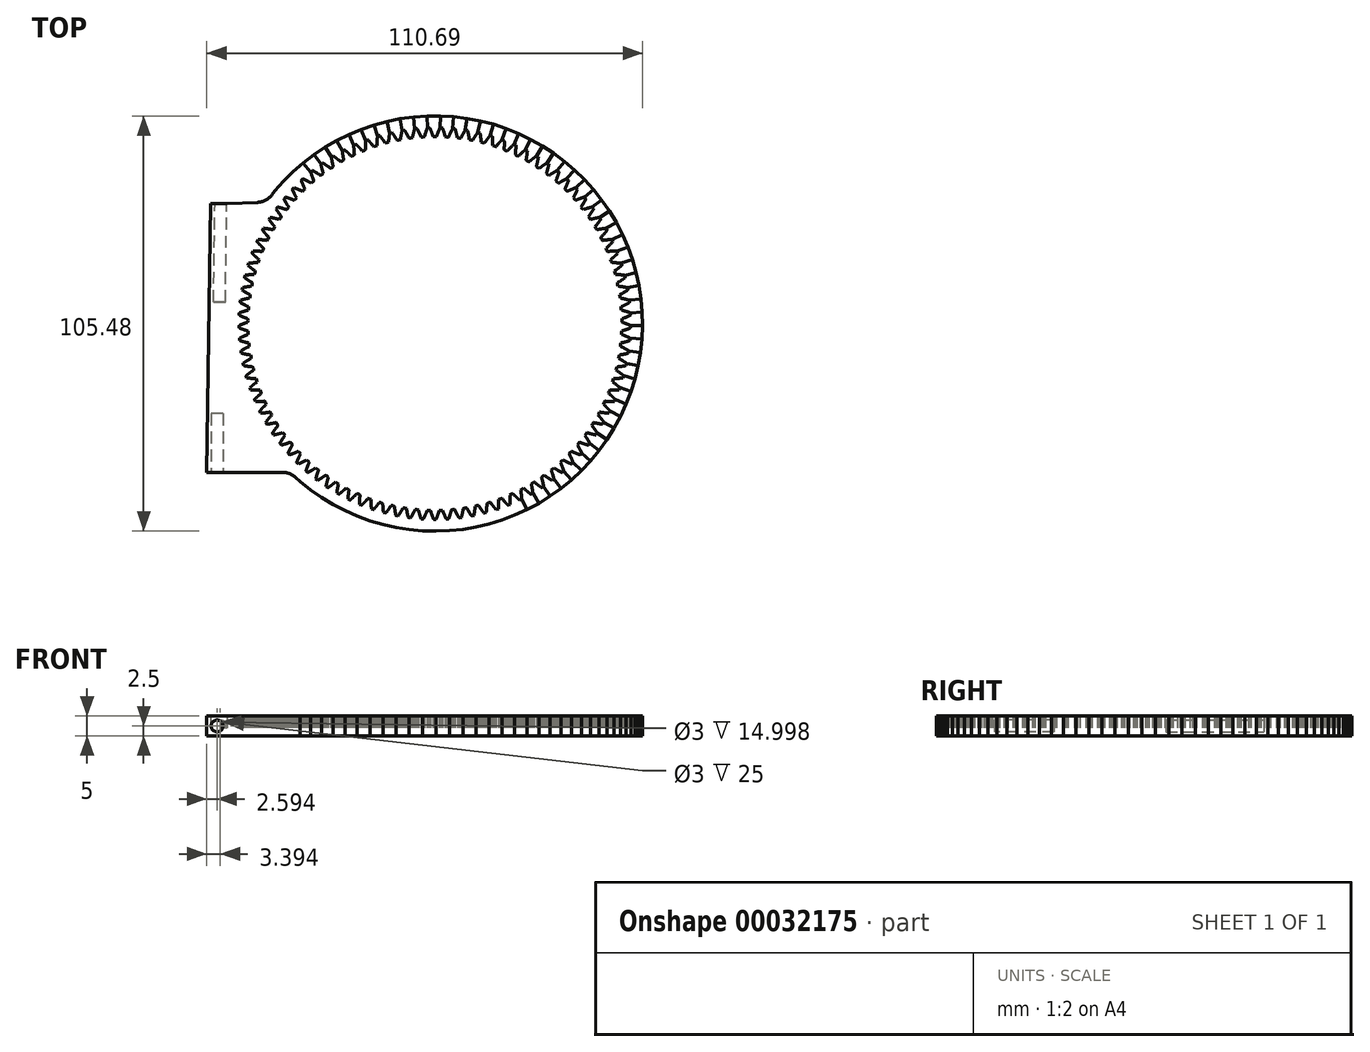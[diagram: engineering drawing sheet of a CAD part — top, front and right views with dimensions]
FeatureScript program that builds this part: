
annotation { "Feature Type Name" : "Feature", "Feature Type Description" : "" }
export const myFeature = defineFeature(function(context is Context, id is Id, definition is map)
    precondition{}
    {
        {
            var Q0;
            Q0=qCreatedBy(makeId("Top.planeOp"),FACE);
            var sketch = newSketch(context, id + "F0", { "sketchPlane" : qUnion([Q0])});
            skCircle(sketch, "E0", {"center": v(0, 0) * mm, "radius": 52.75 * mm});
            skLineSegment(sketch, "E1", {"start": v(1.31, 49.73) * mm, "end": v(1.3, 49.69) * mm});
            skLineSegment(sketch, "E2", {"start": v(1.3, 49.69) * mm, "end": v(1.27, 49.64) * mm});
            skLineSegment(sketch, "E3", {"start": v(1.27, 49.64) * mm, "end": v(1.25, 49.6) * mm});
            skLineSegment(sketch, "E4", {"start": v(1.25, 49.6) * mm, "end": v(1.23, 49.55) * mm});
            skLineSegment(sketch, "E5", {"start": v(1.23, 49.55) * mm, "end": v(1.21, 49.51) * mm});
            skLineSegment(sketch, "E6", {"start": v(1.21, 49.51) * mm, "end": v(1.2, 49.47) * mm});
            skLineSegment(sketch, "E7", {"start": v(1.2, 49.47) * mm, "end": v(1.17, 49.42) * mm});
            skLineSegment(sketch, "E8", {"start": v(1.17, 49.42) * mm, "end": v(1.15, 49.38) * mm});
            skLineSegment(sketch, "E9", {"start": v(1.15, 49.38) * mm, "end": v(1.13, 49.33) * mm});
            skLineSegment(sketch, "E10", {"start": v(1.13, 49.33) * mm, "end": v(1.11, 49.29) * mm});
            skLineSegment(sketch, "E11", {"start": v(1.11, 49.29) * mm, "end": v(1.1, 49.24) * mm});
            skLineSegment(sketch, "E12", {"start": v(1.1, 49.24) * mm, "end": v(1.07, 49.2) * mm});
            skLineSegment(sketch, "E13", {"start": v(1.07, 49.2) * mm, "end": v(1.05, 49.15) * mm});
            skLineSegment(sketch, "E14", {"start": v(1.05, 49.15) * mm, "end": v(1.03, 49.1) * mm});
            skLineSegment(sketch, "E15", {"start": v(1.03, 49.1) * mm, "end": v(1.02, 49.06) * mm});
            skLineSegment(sketch, "E16", {"start": v(1.02, 49.06) * mm, "end": v(1, 49.02) * mm});
            skLineSegment(sketch, "E17", {"start": v(1, 49.02) * mm, "end": v(0.98, 48.98) * mm});
            skLineSegment(sketch, "E18", {"start": v(0.98, 48.98) * mm, "end": v(0.96, 48.93) * mm});
            skLineSegment(sketch, "E19", {"start": v(0.96, 48.93) * mm, "end": v(0.94, 48.89) * mm});
            skLineSegment(sketch, "E20", {"start": v(0.94, 48.89) * mm, "end": v(0.92, 48.84) * mm});
            skLineSegment(sketch, "E21", {"start": v(0.92, 48.84) * mm, "end": v(0.9, 48.8) * mm});
            skLineSegment(sketch, "E22", {"start": v(0.9, 48.8) * mm, "end": v(0.89, 48.75) * mm});
            skLineSegment(sketch, "E23", {"start": v(0.89, 48.75) * mm, "end": v(0.87, 48.7) * mm});
            skLineSegment(sketch, "E24", {"start": v(0.87, 48.7) * mm, "end": v(0.85, 48.66) * mm});
            skLineSegment(sketch, "E25", {"start": v(0.85, 48.66) * mm, "end": v(0.83, 48.62) * mm});
            skLineSegment(sketch, "E26", {"start": v(0.83, 48.62) * mm, "end": v(0.82, 48.57) * mm});
            skLineSegment(sketch, "E27", {"start": v(0.82, 48.57) * mm, "end": v(0.8, 48.53) * mm});
            skLineSegment(sketch, "E28", {"start": v(0.8, 48.53) * mm, "end": v(0.78, 48.48) * mm});
            skLineSegment(sketch, "E29", {"start": v(0.78, 48.48) * mm, "end": v(0.76, 48.44) * mm});
            skLineSegment(sketch, "E30", {"start": v(0.76, 48.44) * mm, "end": v(0.75, 48.4) * mm});
            skLineSegment(sketch, "E31", {"start": v(0.75, 48.4) * mm, "end": v(0.73, 48.35) * mm});
            skLineSegment(sketch, "E32", {"start": v(0.73, 48.35) * mm, "end": v(0.71, 48.3) * mm});
            skLineSegment(sketch, "E33", {"start": v(0.71, 48.3) * mm, "end": v(0.7, 48.26) * mm});
            skLineSegment(sketch, "E34", {"start": v(0.7, 48.26) * mm, "end": v(0.68, 48.22) * mm});
            skLineSegment(sketch, "E35", {"start": v(0.68, 48.22) * mm, "end": v(0.67, 48.17) * mm});
            skLineSegment(sketch, "E36", {"start": v(0.67, 48.17) * mm, "end": v(0.65, 48.13) * mm});
            skLineSegment(sketch, "E37", {"start": v(0.65, 48.13) * mm, "end": v(0.63, 48.08) * mm});
            skLineSegment(sketch, "E38", {"start": v(0.63, 48.08) * mm, "end": v(0.62, 48.04) * mm});
            skLineSegment(sketch, "E39", {"start": v(0.62, 48.04) * mm, "end": v(0.6, 48) * mm});
            skLineSegment(sketch, "E40", {"start": v(0.6, 48) * mm, "end": v(0.58, 47.95) * mm});
            skLineSegment(sketch, "E41", {"start": v(0.58, 47.95) * mm, "end": v(0.57, 47.9) * mm});
            skLineSegment(sketch, "E42", {"start": v(0.57, 47.9) * mm, "end": v(0.55, 47.86) * mm});
            skLineSegment(sketch, "E43", {"start": v(0.55, 47.86) * mm, "end": v(0.53, 47.81) * mm});
            skLineSegment(sketch, "E44", {"start": v(0.53, 47.81) * mm, "end": v(0.52, 47.77) * mm});
            skLineSegment(sketch, "E45", {"start": v(0.52, 47.77) * mm, "end": v(0.5, 47.72) * mm});
            skLineSegment(sketch, "E46", {"start": v(0.5, 47.72) * mm, "end": v(0.49, 47.68) * mm});
            skLineSegment(sketch, "E47", {"start": v(0.49, 47.68) * mm, "end": v(0.47, 47.63) * mm});
            skLineSegment(sketch, "E48", {"start": v(0.47, 47.63) * mm, "end": v(0.45, 47.59) * mm});
            skLineSegment(sketch, "E49", {"start": v(0.45, 47.59) * mm, "end": v(0.44, 47.54) * mm});
            skLineSegment(sketch, "E50", {"start": v(0.44, 47.54) * mm, "end": v(0, 47.5) * mm});
            skLineSegment(sketch, "E51", {"start": v(0, 47.5) * mm, "end": v(-0.44, 47.54) * mm});
            skLineSegment(sketch, "E52", {"start": v(-0.44, 47.54) * mm, "end": v(-0.45, 47.59) * mm});
            skLineSegment(sketch, "E53", {"start": v(-0.45, 47.59) * mm, "end": v(-0.47, 47.63) * mm});
            skLineSegment(sketch, "E54", {"start": v(-0.47, 47.63) * mm, "end": v(-0.49, 47.68) * mm});
            skLineSegment(sketch, "E55", {"start": v(-0.49, 47.68) * mm, "end": v(-0.5, 47.72) * mm});
            skLineSegment(sketch, "E56", {"start": v(-0.5, 47.72) * mm, "end": v(-0.52, 47.77) * mm});
            skLineSegment(sketch, "E57", {"start": v(-0.52, 47.77) * mm, "end": v(-0.53, 47.81) * mm});
            skLineSegment(sketch, "E58", {"start": v(-0.53, 47.81) * mm, "end": v(-0.55, 47.86) * mm});
            skLineSegment(sketch, "E59", {"start": v(-0.55, 47.86) * mm, "end": v(-0.57, 47.9) * mm});
            skLineSegment(sketch, "E60", {"start": v(-0.57, 47.9) * mm, "end": v(-0.58, 47.95) * mm});
            skLineSegment(sketch, "E61", {"start": v(-0.58, 47.95) * mm, "end": v(-0.6, 48) * mm});
            skLineSegment(sketch, "E62", {"start": v(-0.6, 48) * mm, "end": v(-0.62, 48.04) * mm});
            skLineSegment(sketch, "E63", {"start": v(-0.62, 48.04) * mm, "end": v(-0.63, 48.08) * mm});
            skLineSegment(sketch, "E64", {"start": v(-0.63, 48.08) * mm, "end": v(-0.65, 48.13) * mm});
            skLineSegment(sketch, "E65", {"start": v(-0.65, 48.13) * mm, "end": v(-0.67, 48.17) * mm});
            skLineSegment(sketch, "E66", {"start": v(-0.67, 48.17) * mm, "end": v(-0.68, 48.22) * mm});
            skLineSegment(sketch, "E67", {"start": v(-0.68, 48.22) * mm, "end": v(-0.7, 48.26) * mm});
            skLineSegment(sketch, "E68", {"start": v(-0.7, 48.26) * mm, "end": v(-0.71, 48.3) * mm});
            skLineSegment(sketch, "E69", {"start": v(-0.71, 48.3) * mm, "end": v(-0.73, 48.35) * mm});
            skLineSegment(sketch, "E70", {"start": v(-0.73, 48.35) * mm, "end": v(-0.75, 48.4) * mm});
            skLineSegment(sketch, "E71", {"start": v(-0.75, 48.4) * mm, "end": v(-0.76, 48.44) * mm});
            skLineSegment(sketch, "E72", {"start": v(-0.76, 48.44) * mm, "end": v(-0.78, 48.48) * mm});
            skLineSegment(sketch, "E73", {"start": v(-0.78, 48.48) * mm, "end": v(-0.8, 48.53) * mm});
            skLineSegment(sketch, "E74", {"start": v(-0.8, 48.53) * mm, "end": v(-0.82, 48.57) * mm});
            skLineSegment(sketch, "E75", {"start": v(-0.82, 48.57) * mm, "end": v(-0.83, 48.62) * mm});
            skLineSegment(sketch, "E76", {"start": v(-0.83, 48.62) * mm, "end": v(-0.85, 48.66) * mm});
            skLineSegment(sketch, "E77", {"start": v(-0.85, 48.66) * mm, "end": v(-0.87, 48.7) * mm});
            skLineSegment(sketch, "E78", {"start": v(-0.87, 48.7) * mm, "end": v(-0.89, 48.75) * mm});
            skLineSegment(sketch, "E79", {"start": v(-0.89, 48.75) * mm, "end": v(-0.9, 48.8) * mm});
            skLineSegment(sketch, "E80", {"start": v(-0.9, 48.8) * mm, "end": v(-0.92, 48.84) * mm});
            skLineSegment(sketch, "E81", {"start": v(-0.92, 48.84) * mm, "end": v(-0.94, 48.89) * mm});
            skLineSegment(sketch, "E82", {"start": v(-0.94, 48.89) * mm, "end": v(-0.96, 48.93) * mm});
            skLineSegment(sketch, "E83", {"start": v(-0.96, 48.93) * mm, "end": v(-0.98, 48.98) * mm});
            skLineSegment(sketch, "E84", {"start": v(-0.98, 48.98) * mm, "end": v(-1, 49.02) * mm});
            skLineSegment(sketch, "E85", {"start": v(-1, 49.02) * mm, "end": v(-1.02, 49.06) * mm});
            skLineSegment(sketch, "E86", {"start": v(-1.02, 49.06) * mm, "end": v(-1.03, 49.1) * mm});
            skLineSegment(sketch, "E87", {"start": v(-1.03, 49.1) * mm, "end": v(-1.05, 49.15) * mm});
            skLineSegment(sketch, "E88", {"start": v(-1.05, 49.15) * mm, "end": v(-1.07, 49.2) * mm});
            skLineSegment(sketch, "E89", {"start": v(-1.07, 49.2) * mm, "end": v(-1.1, 49.24) * mm});
            skLineSegment(sketch, "E90", {"start": v(-1.1, 49.24) * mm, "end": v(-1.11, 49.29) * mm});
            skLineSegment(sketch, "E91", {"start": v(-1.11, 49.29) * mm, "end": v(-1.13, 49.33) * mm});
            skLineSegment(sketch, "E92", {"start": v(-1.13, 49.33) * mm, "end": v(-1.15, 49.38) * mm});
            skLineSegment(sketch, "E93", {"start": v(-1.15, 49.38) * mm, "end": v(-1.17, 49.42) * mm});
            skLineSegment(sketch, "E94", {"start": v(-1.17, 49.42) * mm, "end": v(-1.2, 49.47) * mm});
            skLineSegment(sketch, "E95", {"start": v(-1.2, 49.47) * mm, "end": v(-1.21, 49.51) * mm});
            skLineSegment(sketch, "E96", {"start": v(-1.21, 49.51) * mm, "end": v(-1.23, 49.55) * mm});
            skLineSegment(sketch, "E97", {"start": v(-1.23, 49.55) * mm, "end": v(-1.25, 49.6) * mm});
            skLineSegment(sketch, "E98", {"start": v(-1.25, 49.6) * mm, "end": v(-1.27, 49.64) * mm});
            skLineSegment(sketch, "E99", {"start": v(-1.27, 49.64) * mm, "end": v(-1.3, 49.69) * mm});
            skLineSegment(sketch, "E100", {"start": v(-1.3, 49.69) * mm, "end": v(-1.31, 49.73) * mm});
            skLineSegment(sketch, "E101", {"start": v(-1.31, 49.73) * mm, "end": v(-1.9, 49.71) * mm});
            skLineSegment(sketch, "E102", {"start": v(0, 0) * mm, "end": v(-2.02, 52.71) * mm});
            skLineSegment(sketch, "E103", {"start": v(0, 0) * mm, "end": v(1.4, 52.73) * mm});
            skLineSegment(sketch, "E104", {"start": v(-2.02, 52.71) * mm, "end": v(1.4, 52.73) * mm});
            skCircle(sketch, "E105", {"center": v(0, 0) * mm, "radius": 0.44 * mm});
            skSolve(sketch);
        }
        {
            var Q0;
            {var subQ3=sQuery(id+"F0.wireOp",EDGE,"E1");Q0=makeQuery(id+"F0.imprint","IMPRINT",FACE,{"disambiguationData":[TD([[makeQuery(id+"F0.imprint","IMPRINT",EDGE,{"derivedFrom":subQ3}),-1.0]])]});}
            var Q1;
            {var subQ1=sQuery(id+"F0.wireOp",EDGE,"E103");var subQ3=sQuery(id+"F0.wireOp",EDGE,"E102");var subQ5=makeQuery(id+"F0.imprint","INTERSECT",VERTEX,{"derivedFrom":[subQ3,subQ1]});Q1=makeQuery(id+"F0.imprint","IMPRINT",FACE,{"disambiguationData":[TD([[makeQuery(id+"F0.imprint","IMPRINT",EDGE,{"disambiguationData":[TD([[subQ5,-1.0]])],"derivedFrom":subQ3}),1.0]])]});}
            var Q2;
            {var subQ0=sQuery(id+"F0.wireOp",EDGE,"E103");var subQ3=sQuery(id+"F0.wireOp",EDGE,"E102");var subQ4=makeQuery(id+"F0.imprint","INTERSECT",VERTEX,{"derivedFrom":[subQ3,subQ0]});Q2=makeQuery(id+"F0.imprint","IMPRINT",FACE,{"disambiguationData":[TD([[makeQuery(id+"F0.imprint","IMPRINT",EDGE,{"disambiguationData":[TD([[subQ4,-1.0]])],"derivedFrom":subQ3}),-1.0]])]});}
            extrude(context, id + "F1", {"entities" : qUnion([Q0, Q1, Q2]), "depth" : 5 * mm});
        }
        {
            var Q0;
            Q0=makeQuery(id+"F1.opExtrude","SWEPT_BODY",BODY,{"disambiguationData":[OSD([sQuery(id+"F0.wireOp",EDGE,"E1"),sQuery(id+"F0.wireOp",EDGE,"E2"),sQuery(id+"F0.wireOp",EDGE,"E3"),sQuery(id+"F0.wireOp",EDGE,"E4"),sQuery(id+"F0.wireOp",EDGE,"E5"),sQuery(id+"F0.wireOp",EDGE,"E6"),sQuery(id+"F0.wireOp",EDGE,"E7"),sQuery(id+"F0.wireOp",EDGE,"E8"),sQuery(id+"F0.wireOp",EDGE,"E9"),sQuery(id+"F0.wireOp",EDGE,"E10"),sQuery(id+"F0.wireOp",EDGE,"E11"),sQuery(id+"F0.wireOp",EDGE,"E12"),sQuery(id+"F0.wireOp",EDGE,"E13"),sQuery(id+"F0.wireOp",EDGE,"E14"),sQuery(id+"F0.wireOp",EDGE,"E15"),sQuery(id+"F0.wireOp",EDGE,"E16"),sQuery(id+"F0.wireOp",EDGE,"E17"),sQuery(id+"F0.wireOp",EDGE,"E18"),sQuery(id+"F0.wireOp",EDGE,"E19"),sQuery(id+"F0.wireOp",EDGE,"E20"),sQuery(id+"F0.wireOp",EDGE,"E21"),sQuery(id+"F0.wireOp",EDGE,"E22"),sQuery(id+"F0.wireOp",EDGE,"E23"),sQuery(id+"F0.wireOp",EDGE,"E24"),sQuery(id+"F0.wireOp",EDGE,"E25"),sQuery(id+"F0.wireOp",EDGE,"E26"),sQuery(id+"F0.wireOp",EDGE,"E27"),sQuery(id+"F0.wireOp",EDGE,"E28"),sQuery(id+"F0.wireOp",EDGE,"E29"),sQuery(id+"F0.wireOp",EDGE,"E30"),sQuery(id+"F0.wireOp",EDGE,"E31"),sQuery(id+"F0.wireOp",EDGE,"E32"),sQuery(id+"F0.wireOp",EDGE,"E33"),sQuery(id+"F0.wireOp",EDGE,"E34"),sQuery(id+"F0.wireOp",EDGE,"E35"),sQuery(id+"F0.wireOp",EDGE,"E36"),sQuery(id+"F0.wireOp",EDGE,"E37"),sQuery(id+"F0.wireOp",EDGE,"E38"),sQuery(id+"F0.wireOp",EDGE,"E39"),sQuery(id+"F0.wireOp",EDGE,"E40"),sQuery(id+"F0.wireOp",EDGE,"E41"),sQuery(id+"F0.wireOp",EDGE,"E42"),sQuery(id+"F0.wireOp",EDGE,"E43"),sQuery(id+"F0.wireOp",EDGE,"E44"),sQuery(id+"F0.wireOp",EDGE,"E45"),sQuery(id+"F0.wireOp",EDGE,"E46"),sQuery(id+"F0.wireOp",EDGE,"E47"),sQuery(id+"F0.wireOp",EDGE,"E48"),sQuery(id+"F0.wireOp",EDGE,"E49"),sQuery(id+"F0.wireOp",EDGE,"E50"),sQuery(id+"F0.wireOp",EDGE,"E51"),sQuery(id+"F0.wireOp",EDGE,"E52"),sQuery(id+"F0.wireOp",EDGE,"E53"),sQuery(id+"F0.wireOp",EDGE,"E54"),sQuery(id+"F0.wireOp",EDGE,"E55"),sQuery(id+"F0.wireOp",EDGE,"E56"),sQuery(id+"F0.wireOp",EDGE,"E57"),sQuery(id+"F0.wireOp",EDGE,"E58"),sQuery(id+"F0.wireOp",EDGE,"E59"),sQuery(id+"F0.wireOp",EDGE,"E60"),sQuery(id+"F0.wireOp",EDGE,"E61"),sQuery(id+"F0.wireOp",EDGE,"E62"),sQuery(id+"F0.wireOp",EDGE,"E63"),sQuery(id+"F0.wireOp",EDGE,"E64"),sQuery(id+"F0.wireOp",EDGE,"E65"),sQuery(id+"F0.wireOp",EDGE,"E66"),sQuery(id+"F0.wireOp",EDGE,"E67"),sQuery(id+"F0.wireOp",EDGE,"E68"),sQuery(id+"F0.wireOp",EDGE,"E69"),sQuery(id+"F0.wireOp",EDGE,"E70"),sQuery(id+"F0.wireOp",EDGE,"E71"),sQuery(id+"F0.wireOp",EDGE,"E72"),sQuery(id+"F0.wireOp",EDGE,"E73"),sQuery(id+"F0.wireOp",EDGE,"E74"),sQuery(id+"F0.wireOp",EDGE,"E75"),sQuery(id+"F0.wireOp",EDGE,"E76"),sQuery(id+"F0.wireOp",EDGE,"E77"),sQuery(id+"F0.wireOp",EDGE,"E78"),sQuery(id+"F0.wireOp",EDGE,"E79"),sQuery(id+"F0.wireOp",EDGE,"E80"),sQuery(id+"F0.wireOp",EDGE,"E81"),sQuery(id+"F0.wireOp",EDGE,"E82"),sQuery(id+"F0.wireOp",EDGE,"E83"),sQuery(id+"F0.wireOp",EDGE,"E84"),sQuery(id+"F0.wireOp",EDGE,"E85"),sQuery(id+"F0.wireOp",EDGE,"E86"),sQuery(id+"F0.wireOp",EDGE,"E87"),sQuery(id+"F0.wireOp",EDGE,"E88"),sQuery(id+"F0.wireOp",EDGE,"E89"),sQuery(id+"F0.wireOp",EDGE,"E90"),sQuery(id+"F0.wireOp",EDGE,"E91"),sQuery(id+"F0.wireOp",EDGE,"E92"),sQuery(id+"F0.wireOp",EDGE,"E93"),sQuery(id+"F0.wireOp",EDGE,"E94"),sQuery(id+"F0.wireOp",EDGE,"E95"),sQuery(id+"F0.wireOp",EDGE,"E96"),sQuery(id+"F0.wireOp",EDGE,"E97"),sQuery(id+"F0.wireOp",EDGE,"E98"),sQuery(id+"F0.wireOp",EDGE,"E99"),sQuery(id+"F0.wireOp",EDGE,"E100"),sQuery(id+"F0.wireOp",EDGE,"E101"),sQuery(id+"F0.wireOp",EDGE,"E102"),sQuery(id+"F0.wireOp",EDGE,"E103"),sQuery(id+"F0.wireOp",EDGE,"E104")])]});
            var Q1;
            Q1=makeQuery(id+"F1.opExtrude","CAP_EDGE",EDGE,{"disambiguationData":[OSD([sQuery(id+"F0.wireOp",EDGE,"E105")])],"isStart":false});
            circularPattern(context, id + "F2", {"entities" : qUnion([Q0]), "axis" : qUnion([Q1]), "angle" : 3.7 * degree, "instanceCount" : 97});
        }
        {
            var Q0;
            Q0=makeQuery(id+"F1.opExtrude","SWEPT_BODY",BODY,{"disambiguationData":[OSD([sQuery(id+"F0.wireOp",EDGE,"E105")])]});
            var Q1;
            Q1=makeQuery(id+"F2.opPattern","COPY",BODY,{"derivedFrom":makeQuery(id+"F1.opExtrude","SWEPT_BODY",BODY,{"disambiguationData":[OSD([sQuery(id+"F0.wireOp",EDGE,"E1"),sQuery(id+"F0.wireOp",EDGE,"E2"),sQuery(id+"F0.wireOp",EDGE,"E3"),sQuery(id+"F0.wireOp",EDGE,"E4"),sQuery(id+"F0.wireOp",EDGE,"E5"),sQuery(id+"F0.wireOp",EDGE,"E6"),sQuery(id+"F0.wireOp",EDGE,"E7"),sQuery(id+"F0.wireOp",EDGE,"E8"),sQuery(id+"F0.wireOp",EDGE,"E9"),sQuery(id+"F0.wireOp",EDGE,"E10"),sQuery(id+"F0.wireOp",EDGE,"E11"),sQuery(id+"F0.wireOp",EDGE,"E12"),sQuery(id+"F0.wireOp",EDGE,"E13"),sQuery(id+"F0.wireOp",EDGE,"E14"),sQuery(id+"F0.wireOp",EDGE,"E15"),sQuery(id+"F0.wireOp",EDGE,"E16"),sQuery(id+"F0.wireOp",EDGE,"E17"),sQuery(id+"F0.wireOp",EDGE,"E18"),sQuery(id+"F0.wireOp",EDGE,"E19"),sQuery(id+"F0.wireOp",EDGE,"E20"),sQuery(id+"F0.wireOp",EDGE,"E21"),sQuery(id+"F0.wireOp",EDGE,"E22"),sQuery(id+"F0.wireOp",EDGE,"E23"),sQuery(id+"F0.wireOp",EDGE,"E24"),sQuery(id+"F0.wireOp",EDGE,"E25"),sQuery(id+"F0.wireOp",EDGE,"E26"),sQuery(id+"F0.wireOp",EDGE,"E27"),sQuery(id+"F0.wireOp",EDGE,"E28"),sQuery(id+"F0.wireOp",EDGE,"E29"),sQuery(id+"F0.wireOp",EDGE,"E30"),sQuery(id+"F0.wireOp",EDGE,"E31"),sQuery(id+"F0.wireOp",EDGE,"E32"),sQuery(id+"F0.wireOp",EDGE,"E33"),sQuery(id+"F0.wireOp",EDGE,"E34"),sQuery(id+"F0.wireOp",EDGE,"E35"),sQuery(id+"F0.wireOp",EDGE,"E36"),sQuery(id+"F0.wireOp",EDGE,"E37"),sQuery(id+"F0.wireOp",EDGE,"E38"),sQuery(id+"F0.wireOp",EDGE,"E39"),sQuery(id+"F0.wireOp",EDGE,"E40"),sQuery(id+"F0.wireOp",EDGE,"E41"),sQuery(id+"F0.wireOp",EDGE,"E42"),sQuery(id+"F0.wireOp",EDGE,"E43"),sQuery(id+"F0.wireOp",EDGE,"E44"),sQuery(id+"F0.wireOp",EDGE,"E45"),sQuery(id+"F0.wireOp",EDGE,"E46"),sQuery(id+"F0.wireOp",EDGE,"E47"),sQuery(id+"F0.wireOp",EDGE,"E48"),sQuery(id+"F0.wireOp",EDGE,"E49"),sQuery(id+"F0.wireOp",EDGE,"E50"),sQuery(id+"F0.wireOp",EDGE,"E51"),sQuery(id+"F0.wireOp",EDGE,"E52"),sQuery(id+"F0.wireOp",EDGE,"E53"),sQuery(id+"F0.wireOp",EDGE,"E54"),sQuery(id+"F0.wireOp",EDGE,"E55"),sQuery(id+"F0.wireOp",EDGE,"E56"),sQuery(id+"F0.wireOp",EDGE,"E57"),sQuery(id+"F0.wireOp",EDGE,"E58"),sQuery(id+"F0.wireOp",EDGE,"E59"),sQuery(id+"F0.wireOp",EDGE,"E60"),sQuery(id+"F0.wireOp",EDGE,"E61"),sQuery(id+"F0.wireOp",EDGE,"E62"),sQuery(id+"F0.wireOp",EDGE,"E63"),sQuery(id+"F0.wireOp",EDGE,"E64"),sQuery(id+"F0.wireOp",EDGE,"E65"),sQuery(id+"F0.wireOp",EDGE,"E66"),sQuery(id+"F0.wireOp",EDGE,"E67"),sQuery(id+"F0.wireOp",EDGE,"E68"),sQuery(id+"F0.wireOp",EDGE,"E69"),sQuery(id+"F0.wireOp",EDGE,"E70"),sQuery(id+"F0.wireOp",EDGE,"E71"),sQuery(id+"F0.wireOp",EDGE,"E72"),sQuery(id+"F0.wireOp",EDGE,"E73"),sQuery(id+"F0.wireOp",EDGE,"E74"),sQuery(id+"F0.wireOp",EDGE,"E75"),sQuery(id+"F0.wireOp",EDGE,"E76"),sQuery(id+"F0.wireOp",EDGE,"E77"),sQuery(id+"F0.wireOp",EDGE,"E78"),sQuery(id+"F0.wireOp",EDGE,"E79"),sQuery(id+"F0.wireOp",EDGE,"E80"),sQuery(id+"F0.wireOp",EDGE,"E81"),sQuery(id+"F0.wireOp",EDGE,"E82"),sQuery(id+"F0.wireOp",EDGE,"E83"),sQuery(id+"F0.wireOp",EDGE,"E84"),sQuery(id+"F0.wireOp",EDGE,"E85"),sQuery(id+"F0.wireOp",EDGE,"E86"),sQuery(id+"F0.wireOp",EDGE,"E87"),sQuery(id+"F0.wireOp",EDGE,"E88"),sQuery(id+"F0.wireOp",EDGE,"E89"),sQuery(id+"F0.wireOp",EDGE,"E90"),sQuery(id+"F0.wireOp",EDGE,"E91"),sQuery(id+"F0.wireOp",EDGE,"E92"),sQuery(id+"F0.wireOp",EDGE,"E93"),sQuery(id+"F0.wireOp",EDGE,"E94"),sQuery(id+"F0.wireOp",EDGE,"E95"),sQuery(id+"F0.wireOp",EDGE,"E96"),sQuery(id+"F0.wireOp",EDGE,"E97"),sQuery(id+"F0.wireOp",EDGE,"E98"),sQuery(id+"F0.wireOp",EDGE,"E99"),sQuery(id+"F0.wireOp",EDGE,"E100"),sQuery(id+"F0.wireOp",EDGE,"E101"),sQuery(id+"F0.wireOp",EDGE,"E102"),sQuery(id+"F0.wireOp",EDGE,"E103"),sQuery(id+"F0.wireOp",EDGE,"E104")])]}),"instanceName":"1"});
            var Q2;
            Q2=makeQuery(id+"F2.opPattern","COPY",BODY,{"derivedFrom":makeQuery(id+"F1.opExtrude","SWEPT_BODY",BODY,{"disambiguationData":[OSD([sQuery(id+"F0.wireOp",EDGE,"E1"),sQuery(id+"F0.wireOp",EDGE,"E2"),sQuery(id+"F0.wireOp",EDGE,"E3"),sQuery(id+"F0.wireOp",EDGE,"E4"),sQuery(id+"F0.wireOp",EDGE,"E5"),sQuery(id+"F0.wireOp",EDGE,"E6"),sQuery(id+"F0.wireOp",EDGE,"E7"),sQuery(id+"F0.wireOp",EDGE,"E8"),sQuery(id+"F0.wireOp",EDGE,"E9"),sQuery(id+"F0.wireOp",EDGE,"E10"),sQuery(id+"F0.wireOp",EDGE,"E11"),sQuery(id+"F0.wireOp",EDGE,"E12"),sQuery(id+"F0.wireOp",EDGE,"E13"),sQuery(id+"F0.wireOp",EDGE,"E14"),sQuery(id+"F0.wireOp",EDGE,"E15"),sQuery(id+"F0.wireOp",EDGE,"E16"),sQuery(id+"F0.wireOp",EDGE,"E17"),sQuery(id+"F0.wireOp",EDGE,"E18"),sQuery(id+"F0.wireOp",EDGE,"E19"),sQuery(id+"F0.wireOp",EDGE,"E20"),sQuery(id+"F0.wireOp",EDGE,"E21"),sQuery(id+"F0.wireOp",EDGE,"E22"),sQuery(id+"F0.wireOp",EDGE,"E23"),sQuery(id+"F0.wireOp",EDGE,"E24"),sQuery(id+"F0.wireOp",EDGE,"E25"),sQuery(id+"F0.wireOp",EDGE,"E26"),sQuery(id+"F0.wireOp",EDGE,"E27"),sQuery(id+"F0.wireOp",EDGE,"E28"),sQuery(id+"F0.wireOp",EDGE,"E29"),sQuery(id+"F0.wireOp",EDGE,"E30"),sQuery(id+"F0.wireOp",EDGE,"E31"),sQuery(id+"F0.wireOp",EDGE,"E32"),sQuery(id+"F0.wireOp",EDGE,"E33"),sQuery(id+"F0.wireOp",EDGE,"E34"),sQuery(id+"F0.wireOp",EDGE,"E35"),sQuery(id+"F0.wireOp",EDGE,"E36"),sQuery(id+"F0.wireOp",EDGE,"E37"),sQuery(id+"F0.wireOp",EDGE,"E38"),sQuery(id+"F0.wireOp",EDGE,"E39"),sQuery(id+"F0.wireOp",EDGE,"E40"),sQuery(id+"F0.wireOp",EDGE,"E41"),sQuery(id+"F0.wireOp",EDGE,"E42"),sQuery(id+"F0.wireOp",EDGE,"E43"),sQuery(id+"F0.wireOp",EDGE,"E44"),sQuery(id+"F0.wireOp",EDGE,"E45"),sQuery(id+"F0.wireOp",EDGE,"E46"),sQuery(id+"F0.wireOp",EDGE,"E47"),sQuery(id+"F0.wireOp",EDGE,"E48"),sQuery(id+"F0.wireOp",EDGE,"E49"),sQuery(id+"F0.wireOp",EDGE,"E50"),sQuery(id+"F0.wireOp",EDGE,"E51"),sQuery(id+"F0.wireOp",EDGE,"E52"),sQuery(id+"F0.wireOp",EDGE,"E53"),sQuery(id+"F0.wireOp",EDGE,"E54"),sQuery(id+"F0.wireOp",EDGE,"E55"),sQuery(id+"F0.wireOp",EDGE,"E56"),sQuery(id+"F0.wireOp",EDGE,"E57"),sQuery(id+"F0.wireOp",EDGE,"E58"),sQuery(id+"F0.wireOp",EDGE,"E59"),sQuery(id+"F0.wireOp",EDGE,"E60"),sQuery(id+"F0.wireOp",EDGE,"E61"),sQuery(id+"F0.wireOp",EDGE,"E62"),sQuery(id+"F0.wireOp",EDGE,"E63"),sQuery(id+"F0.wireOp",EDGE,"E64"),sQuery(id+"F0.wireOp",EDGE,"E65"),sQuery(id+"F0.wireOp",EDGE,"E66"),sQuery(id+"F0.wireOp",EDGE,"E67"),sQuery(id+"F0.wireOp",EDGE,"E68"),sQuery(id+"F0.wireOp",EDGE,"E69"),sQuery(id+"F0.wireOp",EDGE,"E70"),sQuery(id+"F0.wireOp",EDGE,"E71"),sQuery(id+"F0.wireOp",EDGE,"E72"),sQuery(id+"F0.wireOp",EDGE,"E73"),sQuery(id+"F0.wireOp",EDGE,"E74"),sQuery(id+"F0.wireOp",EDGE,"E75"),sQuery(id+"F0.wireOp",EDGE,"E76"),sQuery(id+"F0.wireOp",EDGE,"E77"),sQuery(id+"F0.wireOp",EDGE,"E78"),sQuery(id+"F0.wireOp",EDGE,"E79"),sQuery(id+"F0.wireOp",EDGE,"E80"),sQuery(id+"F0.wireOp",EDGE,"E81"),sQuery(id+"F0.wireOp",EDGE,"E82"),sQuery(id+"F0.wireOp",EDGE,"E83"),sQuery(id+"F0.wireOp",EDGE,"E84"),sQuery(id+"F0.wireOp",EDGE,"E85"),sQuery(id+"F0.wireOp",EDGE,"E86"),sQuery(id+"F0.wireOp",EDGE,"E87"),sQuery(id+"F0.wireOp",EDGE,"E88"),sQuery(id+"F0.wireOp",EDGE,"E89"),sQuery(id+"F0.wireOp",EDGE,"E90"),sQuery(id+"F0.wireOp",EDGE,"E91"),sQuery(id+"F0.wireOp",EDGE,"E92"),sQuery(id+"F0.wireOp",EDGE,"E93"),sQuery(id+"F0.wireOp",EDGE,"E94"),sQuery(id+"F0.wireOp",EDGE,"E95"),sQuery(id+"F0.wireOp",EDGE,"E96"),sQuery(id+"F0.wireOp",EDGE,"E97"),sQuery(id+"F0.wireOp",EDGE,"E98"),sQuery(id+"F0.wireOp",EDGE,"E99"),sQuery(id+"F0.wireOp",EDGE,"E100"),sQuery(id+"F0.wireOp",EDGE,"E101"),sQuery(id+"F0.wireOp",EDGE,"E102"),sQuery(id+"F0.wireOp",EDGE,"E103"),sQuery(id+"F0.wireOp",EDGE,"E104")])]}),"instanceName":"11"});
            var Q3;
            Q3=makeQuery(id+"F2.opPattern","COPY",BODY,{"derivedFrom":makeQuery(id+"F1.opExtrude","SWEPT_BODY",BODY,{"disambiguationData":[OSD([sQuery(id+"F0.wireOp",EDGE,"E1"),sQuery(id+"F0.wireOp",EDGE,"E2"),sQuery(id+"F0.wireOp",EDGE,"E3"),sQuery(id+"F0.wireOp",EDGE,"E4"),sQuery(id+"F0.wireOp",EDGE,"E5"),sQuery(id+"F0.wireOp",EDGE,"E6"),sQuery(id+"F0.wireOp",EDGE,"E7"),sQuery(id+"F0.wireOp",EDGE,"E8"),sQuery(id+"F0.wireOp",EDGE,"E9"),sQuery(id+"F0.wireOp",EDGE,"E10"),sQuery(id+"F0.wireOp",EDGE,"E11"),sQuery(id+"F0.wireOp",EDGE,"E12"),sQuery(id+"F0.wireOp",EDGE,"E13"),sQuery(id+"F0.wireOp",EDGE,"E14"),sQuery(id+"F0.wireOp",EDGE,"E15"),sQuery(id+"F0.wireOp",EDGE,"E16"),sQuery(id+"F0.wireOp",EDGE,"E17"),sQuery(id+"F0.wireOp",EDGE,"E18"),sQuery(id+"F0.wireOp",EDGE,"E19"),sQuery(id+"F0.wireOp",EDGE,"E20"),sQuery(id+"F0.wireOp",EDGE,"E21"),sQuery(id+"F0.wireOp",EDGE,"E22"),sQuery(id+"F0.wireOp",EDGE,"E23"),sQuery(id+"F0.wireOp",EDGE,"E24"),sQuery(id+"F0.wireOp",EDGE,"E25"),sQuery(id+"F0.wireOp",EDGE,"E26"),sQuery(id+"F0.wireOp",EDGE,"E27"),sQuery(id+"F0.wireOp",EDGE,"E28"),sQuery(id+"F0.wireOp",EDGE,"E29"),sQuery(id+"F0.wireOp",EDGE,"E30"),sQuery(id+"F0.wireOp",EDGE,"E31"),sQuery(id+"F0.wireOp",EDGE,"E32"),sQuery(id+"F0.wireOp",EDGE,"E33"),sQuery(id+"F0.wireOp",EDGE,"E34"),sQuery(id+"F0.wireOp",EDGE,"E35"),sQuery(id+"F0.wireOp",EDGE,"E36"),sQuery(id+"F0.wireOp",EDGE,"E37"),sQuery(id+"F0.wireOp",EDGE,"E38"),sQuery(id+"F0.wireOp",EDGE,"E39"),sQuery(id+"F0.wireOp",EDGE,"E40"),sQuery(id+"F0.wireOp",EDGE,"E41"),sQuery(id+"F0.wireOp",EDGE,"E42"),sQuery(id+"F0.wireOp",EDGE,"E43"),sQuery(id+"F0.wireOp",EDGE,"E44"),sQuery(id+"F0.wireOp",EDGE,"E45"),sQuery(id+"F0.wireOp",EDGE,"E46"),sQuery(id+"F0.wireOp",EDGE,"E47"),sQuery(id+"F0.wireOp",EDGE,"E48"),sQuery(id+"F0.wireOp",EDGE,"E49"),sQuery(id+"F0.wireOp",EDGE,"E50"),sQuery(id+"F0.wireOp",EDGE,"E51"),sQuery(id+"F0.wireOp",EDGE,"E52"),sQuery(id+"F0.wireOp",EDGE,"E53"),sQuery(id+"F0.wireOp",EDGE,"E54"),sQuery(id+"F0.wireOp",EDGE,"E55"),sQuery(id+"F0.wireOp",EDGE,"E56"),sQuery(id+"F0.wireOp",EDGE,"E57"),sQuery(id+"F0.wireOp",EDGE,"E58"),sQuery(id+"F0.wireOp",EDGE,"E59"),sQuery(id+"F0.wireOp",EDGE,"E60"),sQuery(id+"F0.wireOp",EDGE,"E61"),sQuery(id+"F0.wireOp",EDGE,"E62"),sQuery(id+"F0.wireOp",EDGE,"E63"),sQuery(id+"F0.wireOp",EDGE,"E64"),sQuery(id+"F0.wireOp",EDGE,"E65"),sQuery(id+"F0.wireOp",EDGE,"E66"),sQuery(id+"F0.wireOp",EDGE,"E67"),sQuery(id+"F0.wireOp",EDGE,"E68"),sQuery(id+"F0.wireOp",EDGE,"E69"),sQuery(id+"F0.wireOp",EDGE,"E70"),sQuery(id+"F0.wireOp",EDGE,"E71"),sQuery(id+"F0.wireOp",EDGE,"E72"),sQuery(id+"F0.wireOp",EDGE,"E73"),sQuery(id+"F0.wireOp",EDGE,"E74"),sQuery(id+"F0.wireOp",EDGE,"E75"),sQuery(id+"F0.wireOp",EDGE,"E76"),sQuery(id+"F0.wireOp",EDGE,"E77"),sQuery(id+"F0.wireOp",EDGE,"E78"),sQuery(id+"F0.wireOp",EDGE,"E79"),sQuery(id+"F0.wireOp",EDGE,"E80"),sQuery(id+"F0.wireOp",EDGE,"E81"),sQuery(id+"F0.wireOp",EDGE,"E82"),sQuery(id+"F0.wireOp",EDGE,"E83"),sQuery(id+"F0.wireOp",EDGE,"E84"),sQuery(id+"F0.wireOp",EDGE,"E85"),sQuery(id+"F0.wireOp",EDGE,"E86"),sQuery(id+"F0.wireOp",EDGE,"E87"),sQuery(id+"F0.wireOp",EDGE,"E88"),sQuery(id+"F0.wireOp",EDGE,"E89"),sQuery(id+"F0.wireOp",EDGE,"E90"),sQuery(id+"F0.wireOp",EDGE,"E91"),sQuery(id+"F0.wireOp",EDGE,"E92"),sQuery(id+"F0.wireOp",EDGE,"E93"),sQuery(id+"F0.wireOp",EDGE,"E94"),sQuery(id+"F0.wireOp",EDGE,"E95"),sQuery(id+"F0.wireOp",EDGE,"E96"),sQuery(id+"F0.wireOp",EDGE,"E97"),sQuery(id+"F0.wireOp",EDGE,"E98"),sQuery(id+"F0.wireOp",EDGE,"E99"),sQuery(id+"F0.wireOp",EDGE,"E100"),sQuery(id+"F0.wireOp",EDGE,"E101"),sQuery(id+"F0.wireOp",EDGE,"E102"),sQuery(id+"F0.wireOp",EDGE,"E103"),sQuery(id+"F0.wireOp",EDGE,"E104")])]}),"instanceName":"12"});
            var Q4;
            Q4=makeQuery(id+"F2.opPattern","COPY",BODY,{"derivedFrom":makeQuery(id+"F1.opExtrude","SWEPT_BODY",BODY,{"disambiguationData":[OSD([sQuery(id+"F0.wireOp",EDGE,"E1"),sQuery(id+"F0.wireOp",EDGE,"E2"),sQuery(id+"F0.wireOp",EDGE,"E3"),sQuery(id+"F0.wireOp",EDGE,"E4"),sQuery(id+"F0.wireOp",EDGE,"E5"),sQuery(id+"F0.wireOp",EDGE,"E6"),sQuery(id+"F0.wireOp",EDGE,"E7"),sQuery(id+"F0.wireOp",EDGE,"E8"),sQuery(id+"F0.wireOp",EDGE,"E9"),sQuery(id+"F0.wireOp",EDGE,"E10"),sQuery(id+"F0.wireOp",EDGE,"E11"),sQuery(id+"F0.wireOp",EDGE,"E12"),sQuery(id+"F0.wireOp",EDGE,"E13"),sQuery(id+"F0.wireOp",EDGE,"E14"),sQuery(id+"F0.wireOp",EDGE,"E15"),sQuery(id+"F0.wireOp",EDGE,"E16"),sQuery(id+"F0.wireOp",EDGE,"E17"),sQuery(id+"F0.wireOp",EDGE,"E18"),sQuery(id+"F0.wireOp",EDGE,"E19"),sQuery(id+"F0.wireOp",EDGE,"E20"),sQuery(id+"F0.wireOp",EDGE,"E21"),sQuery(id+"F0.wireOp",EDGE,"E22"),sQuery(id+"F0.wireOp",EDGE,"E23"),sQuery(id+"F0.wireOp",EDGE,"E24"),sQuery(id+"F0.wireOp",EDGE,"E25"),sQuery(id+"F0.wireOp",EDGE,"E26"),sQuery(id+"F0.wireOp",EDGE,"E27"),sQuery(id+"F0.wireOp",EDGE,"E28"),sQuery(id+"F0.wireOp",EDGE,"E29"),sQuery(id+"F0.wireOp",EDGE,"E30"),sQuery(id+"F0.wireOp",EDGE,"E31"),sQuery(id+"F0.wireOp",EDGE,"E32"),sQuery(id+"F0.wireOp",EDGE,"E33"),sQuery(id+"F0.wireOp",EDGE,"E34"),sQuery(id+"F0.wireOp",EDGE,"E35"),sQuery(id+"F0.wireOp",EDGE,"E36"),sQuery(id+"F0.wireOp",EDGE,"E37"),sQuery(id+"F0.wireOp",EDGE,"E38"),sQuery(id+"F0.wireOp",EDGE,"E39"),sQuery(id+"F0.wireOp",EDGE,"E40"),sQuery(id+"F0.wireOp",EDGE,"E41"),sQuery(id+"F0.wireOp",EDGE,"E42"),sQuery(id+"F0.wireOp",EDGE,"E43"),sQuery(id+"F0.wireOp",EDGE,"E44"),sQuery(id+"F0.wireOp",EDGE,"E45"),sQuery(id+"F0.wireOp",EDGE,"E46"),sQuery(id+"F0.wireOp",EDGE,"E47"),sQuery(id+"F0.wireOp",EDGE,"E48"),sQuery(id+"F0.wireOp",EDGE,"E49"),sQuery(id+"F0.wireOp",EDGE,"E50"),sQuery(id+"F0.wireOp",EDGE,"E51"),sQuery(id+"F0.wireOp",EDGE,"E52"),sQuery(id+"F0.wireOp",EDGE,"E53"),sQuery(id+"F0.wireOp",EDGE,"E54"),sQuery(id+"F0.wireOp",EDGE,"E55"),sQuery(id+"F0.wireOp",EDGE,"E56"),sQuery(id+"F0.wireOp",EDGE,"E57"),sQuery(id+"F0.wireOp",EDGE,"E58"),sQuery(id+"F0.wireOp",EDGE,"E59"),sQuery(id+"F0.wireOp",EDGE,"E60"),sQuery(id+"F0.wireOp",EDGE,"E61"),sQuery(id+"F0.wireOp",EDGE,"E62"),sQuery(id+"F0.wireOp",EDGE,"E63"),sQuery(id+"F0.wireOp",EDGE,"E64"),sQuery(id+"F0.wireOp",EDGE,"E65"),sQuery(id+"F0.wireOp",EDGE,"E66"),sQuery(id+"F0.wireOp",EDGE,"E67"),sQuery(id+"F0.wireOp",EDGE,"E68"),sQuery(id+"F0.wireOp",EDGE,"E69"),sQuery(id+"F0.wireOp",EDGE,"E70"),sQuery(id+"F0.wireOp",EDGE,"E71"),sQuery(id+"F0.wireOp",EDGE,"E72"),sQuery(id+"F0.wireOp",EDGE,"E73"),sQuery(id+"F0.wireOp",EDGE,"E74"),sQuery(id+"F0.wireOp",EDGE,"E75"),sQuery(id+"F0.wireOp",EDGE,"E76"),sQuery(id+"F0.wireOp",EDGE,"E77"),sQuery(id+"F0.wireOp",EDGE,"E78"),sQuery(id+"F0.wireOp",EDGE,"E79"),sQuery(id+"F0.wireOp",EDGE,"E80"),sQuery(id+"F0.wireOp",EDGE,"E81"),sQuery(id+"F0.wireOp",EDGE,"E82"),sQuery(id+"F0.wireOp",EDGE,"E83"),sQuery(id+"F0.wireOp",EDGE,"E84"),sQuery(id+"F0.wireOp",EDGE,"E85"),sQuery(id+"F0.wireOp",EDGE,"E86"),sQuery(id+"F0.wireOp",EDGE,"E87"),sQuery(id+"F0.wireOp",EDGE,"E88"),sQuery(id+"F0.wireOp",EDGE,"E89"),sQuery(id+"F0.wireOp",EDGE,"E90"),sQuery(id+"F0.wireOp",EDGE,"E91"),sQuery(id+"F0.wireOp",EDGE,"E92"),sQuery(id+"F0.wireOp",EDGE,"E93"),sQuery(id+"F0.wireOp",EDGE,"E94"),sQuery(id+"F0.wireOp",EDGE,"E95"),sQuery(id+"F0.wireOp",EDGE,"E96"),sQuery(id+"F0.wireOp",EDGE,"E97"),sQuery(id+"F0.wireOp",EDGE,"E98"),sQuery(id+"F0.wireOp",EDGE,"E99"),sQuery(id+"F0.wireOp",EDGE,"E100"),sQuery(id+"F0.wireOp",EDGE,"E101"),sQuery(id+"F0.wireOp",EDGE,"E102"),sQuery(id+"F0.wireOp",EDGE,"E103"),sQuery(id+"F0.wireOp",EDGE,"E104")])]}),"instanceName":"13"});
            var Q5;
            Q5=makeQuery(id+"F2.opPattern","COPY",BODY,{"derivedFrom":makeQuery(id+"F1.opExtrude","SWEPT_BODY",BODY,{"disambiguationData":[OSD([sQuery(id+"F0.wireOp",EDGE,"E1"),sQuery(id+"F0.wireOp",EDGE,"E2"),sQuery(id+"F0.wireOp",EDGE,"E3"),sQuery(id+"F0.wireOp",EDGE,"E4"),sQuery(id+"F0.wireOp",EDGE,"E5"),sQuery(id+"F0.wireOp",EDGE,"E6"),sQuery(id+"F0.wireOp",EDGE,"E7"),sQuery(id+"F0.wireOp",EDGE,"E8"),sQuery(id+"F0.wireOp",EDGE,"E9"),sQuery(id+"F0.wireOp",EDGE,"E10"),sQuery(id+"F0.wireOp",EDGE,"E11"),sQuery(id+"F0.wireOp",EDGE,"E12"),sQuery(id+"F0.wireOp",EDGE,"E13"),sQuery(id+"F0.wireOp",EDGE,"E14"),sQuery(id+"F0.wireOp",EDGE,"E15"),sQuery(id+"F0.wireOp",EDGE,"E16"),sQuery(id+"F0.wireOp",EDGE,"E17"),sQuery(id+"F0.wireOp",EDGE,"E18"),sQuery(id+"F0.wireOp",EDGE,"E19"),sQuery(id+"F0.wireOp",EDGE,"E20"),sQuery(id+"F0.wireOp",EDGE,"E21"),sQuery(id+"F0.wireOp",EDGE,"E22"),sQuery(id+"F0.wireOp",EDGE,"E23"),sQuery(id+"F0.wireOp",EDGE,"E24"),sQuery(id+"F0.wireOp",EDGE,"E25"),sQuery(id+"F0.wireOp",EDGE,"E26"),sQuery(id+"F0.wireOp",EDGE,"E27"),sQuery(id+"F0.wireOp",EDGE,"E28"),sQuery(id+"F0.wireOp",EDGE,"E29"),sQuery(id+"F0.wireOp",EDGE,"E30"),sQuery(id+"F0.wireOp",EDGE,"E31"),sQuery(id+"F0.wireOp",EDGE,"E32"),sQuery(id+"F0.wireOp",EDGE,"E33"),sQuery(id+"F0.wireOp",EDGE,"E34"),sQuery(id+"F0.wireOp",EDGE,"E35"),sQuery(id+"F0.wireOp",EDGE,"E36"),sQuery(id+"F0.wireOp",EDGE,"E37"),sQuery(id+"F0.wireOp",EDGE,"E38"),sQuery(id+"F0.wireOp",EDGE,"E39"),sQuery(id+"F0.wireOp",EDGE,"E40"),sQuery(id+"F0.wireOp",EDGE,"E41"),sQuery(id+"F0.wireOp",EDGE,"E42"),sQuery(id+"F0.wireOp",EDGE,"E43"),sQuery(id+"F0.wireOp",EDGE,"E44"),sQuery(id+"F0.wireOp",EDGE,"E45"),sQuery(id+"F0.wireOp",EDGE,"E46"),sQuery(id+"F0.wireOp",EDGE,"E47"),sQuery(id+"F0.wireOp",EDGE,"E48"),sQuery(id+"F0.wireOp",EDGE,"E49"),sQuery(id+"F0.wireOp",EDGE,"E50"),sQuery(id+"F0.wireOp",EDGE,"E51"),sQuery(id+"F0.wireOp",EDGE,"E52"),sQuery(id+"F0.wireOp",EDGE,"E53"),sQuery(id+"F0.wireOp",EDGE,"E54"),sQuery(id+"F0.wireOp",EDGE,"E55"),sQuery(id+"F0.wireOp",EDGE,"E56"),sQuery(id+"F0.wireOp",EDGE,"E57"),sQuery(id+"F0.wireOp",EDGE,"E58"),sQuery(id+"F0.wireOp",EDGE,"E59"),sQuery(id+"F0.wireOp",EDGE,"E60"),sQuery(id+"F0.wireOp",EDGE,"E61"),sQuery(id+"F0.wireOp",EDGE,"E62"),sQuery(id+"F0.wireOp",EDGE,"E63"),sQuery(id+"F0.wireOp",EDGE,"E64"),sQuery(id+"F0.wireOp",EDGE,"E65"),sQuery(id+"F0.wireOp",EDGE,"E66"),sQuery(id+"F0.wireOp",EDGE,"E67"),sQuery(id+"F0.wireOp",EDGE,"E68"),sQuery(id+"F0.wireOp",EDGE,"E69"),sQuery(id+"F0.wireOp",EDGE,"E70"),sQuery(id+"F0.wireOp",EDGE,"E71"),sQuery(id+"F0.wireOp",EDGE,"E72"),sQuery(id+"F0.wireOp",EDGE,"E73"),sQuery(id+"F0.wireOp",EDGE,"E74"),sQuery(id+"F0.wireOp",EDGE,"E75"),sQuery(id+"F0.wireOp",EDGE,"E76"),sQuery(id+"F0.wireOp",EDGE,"E77"),sQuery(id+"F0.wireOp",EDGE,"E78"),sQuery(id+"F0.wireOp",EDGE,"E79"),sQuery(id+"F0.wireOp",EDGE,"E80"),sQuery(id+"F0.wireOp",EDGE,"E81"),sQuery(id+"F0.wireOp",EDGE,"E82"),sQuery(id+"F0.wireOp",EDGE,"E83"),sQuery(id+"F0.wireOp",EDGE,"E84"),sQuery(id+"F0.wireOp",EDGE,"E85"),sQuery(id+"F0.wireOp",EDGE,"E86"),sQuery(id+"F0.wireOp",EDGE,"E87"),sQuery(id+"F0.wireOp",EDGE,"E88"),sQuery(id+"F0.wireOp",EDGE,"E89"),sQuery(id+"F0.wireOp",EDGE,"E90"),sQuery(id+"F0.wireOp",EDGE,"E91"),sQuery(id+"F0.wireOp",EDGE,"E92"),sQuery(id+"F0.wireOp",EDGE,"E93"),sQuery(id+"F0.wireOp",EDGE,"E94"),sQuery(id+"F0.wireOp",EDGE,"E95"),sQuery(id+"F0.wireOp",EDGE,"E96"),sQuery(id+"F0.wireOp",EDGE,"E97"),sQuery(id+"F0.wireOp",EDGE,"E98"),sQuery(id+"F0.wireOp",EDGE,"E99"),sQuery(id+"F0.wireOp",EDGE,"E100"),sQuery(id+"F0.wireOp",EDGE,"E101"),sQuery(id+"F0.wireOp",EDGE,"E102"),sQuery(id+"F0.wireOp",EDGE,"E103"),sQuery(id+"F0.wireOp",EDGE,"E104")])]}),"instanceName":"14"});
            var Q6;
            Q6=makeQuery(id+"F2.opPattern","COPY",BODY,{"derivedFrom":makeQuery(id+"F1.opExtrude","SWEPT_BODY",BODY,{"disambiguationData":[OSD([sQuery(id+"F0.wireOp",EDGE,"E1"),sQuery(id+"F0.wireOp",EDGE,"E2"),sQuery(id+"F0.wireOp",EDGE,"E3"),sQuery(id+"F0.wireOp",EDGE,"E4"),sQuery(id+"F0.wireOp",EDGE,"E5"),sQuery(id+"F0.wireOp",EDGE,"E6"),sQuery(id+"F0.wireOp",EDGE,"E7"),sQuery(id+"F0.wireOp",EDGE,"E8"),sQuery(id+"F0.wireOp",EDGE,"E9"),sQuery(id+"F0.wireOp",EDGE,"E10"),sQuery(id+"F0.wireOp",EDGE,"E11"),sQuery(id+"F0.wireOp",EDGE,"E12"),sQuery(id+"F0.wireOp",EDGE,"E13"),sQuery(id+"F0.wireOp",EDGE,"E14"),sQuery(id+"F0.wireOp",EDGE,"E15"),sQuery(id+"F0.wireOp",EDGE,"E16"),sQuery(id+"F0.wireOp",EDGE,"E17"),sQuery(id+"F0.wireOp",EDGE,"E18"),sQuery(id+"F0.wireOp",EDGE,"E19"),sQuery(id+"F0.wireOp",EDGE,"E20"),sQuery(id+"F0.wireOp",EDGE,"E21"),sQuery(id+"F0.wireOp",EDGE,"E22"),sQuery(id+"F0.wireOp",EDGE,"E23"),sQuery(id+"F0.wireOp",EDGE,"E24"),sQuery(id+"F0.wireOp",EDGE,"E25"),sQuery(id+"F0.wireOp",EDGE,"E26"),sQuery(id+"F0.wireOp",EDGE,"E27"),sQuery(id+"F0.wireOp",EDGE,"E28"),sQuery(id+"F0.wireOp",EDGE,"E29"),sQuery(id+"F0.wireOp",EDGE,"E30"),sQuery(id+"F0.wireOp",EDGE,"E31"),sQuery(id+"F0.wireOp",EDGE,"E32"),sQuery(id+"F0.wireOp",EDGE,"E33"),sQuery(id+"F0.wireOp",EDGE,"E34"),sQuery(id+"F0.wireOp",EDGE,"E35"),sQuery(id+"F0.wireOp",EDGE,"E36"),sQuery(id+"F0.wireOp",EDGE,"E37"),sQuery(id+"F0.wireOp",EDGE,"E38"),sQuery(id+"F0.wireOp",EDGE,"E39"),sQuery(id+"F0.wireOp",EDGE,"E40"),sQuery(id+"F0.wireOp",EDGE,"E41"),sQuery(id+"F0.wireOp",EDGE,"E42"),sQuery(id+"F0.wireOp",EDGE,"E43"),sQuery(id+"F0.wireOp",EDGE,"E44"),sQuery(id+"F0.wireOp",EDGE,"E45"),sQuery(id+"F0.wireOp",EDGE,"E46"),sQuery(id+"F0.wireOp",EDGE,"E47"),sQuery(id+"F0.wireOp",EDGE,"E48"),sQuery(id+"F0.wireOp",EDGE,"E49"),sQuery(id+"F0.wireOp",EDGE,"E50"),sQuery(id+"F0.wireOp",EDGE,"E51"),sQuery(id+"F0.wireOp",EDGE,"E52"),sQuery(id+"F0.wireOp",EDGE,"E53"),sQuery(id+"F0.wireOp",EDGE,"E54"),sQuery(id+"F0.wireOp",EDGE,"E55"),sQuery(id+"F0.wireOp",EDGE,"E56"),sQuery(id+"F0.wireOp",EDGE,"E57"),sQuery(id+"F0.wireOp",EDGE,"E58"),sQuery(id+"F0.wireOp",EDGE,"E59"),sQuery(id+"F0.wireOp",EDGE,"E60"),sQuery(id+"F0.wireOp",EDGE,"E61"),sQuery(id+"F0.wireOp",EDGE,"E62"),sQuery(id+"F0.wireOp",EDGE,"E63"),sQuery(id+"F0.wireOp",EDGE,"E64"),sQuery(id+"F0.wireOp",EDGE,"E65"),sQuery(id+"F0.wireOp",EDGE,"E66"),sQuery(id+"F0.wireOp",EDGE,"E67"),sQuery(id+"F0.wireOp",EDGE,"E68"),sQuery(id+"F0.wireOp",EDGE,"E69"),sQuery(id+"F0.wireOp",EDGE,"E70"),sQuery(id+"F0.wireOp",EDGE,"E71"),sQuery(id+"F0.wireOp",EDGE,"E72"),sQuery(id+"F0.wireOp",EDGE,"E73"),sQuery(id+"F0.wireOp",EDGE,"E74"),sQuery(id+"F0.wireOp",EDGE,"E75"),sQuery(id+"F0.wireOp",EDGE,"E76"),sQuery(id+"F0.wireOp",EDGE,"E77"),sQuery(id+"F0.wireOp",EDGE,"E78"),sQuery(id+"F0.wireOp",EDGE,"E79"),sQuery(id+"F0.wireOp",EDGE,"E80"),sQuery(id+"F0.wireOp",EDGE,"E81"),sQuery(id+"F0.wireOp",EDGE,"E82"),sQuery(id+"F0.wireOp",EDGE,"E83"),sQuery(id+"F0.wireOp",EDGE,"E84"),sQuery(id+"F0.wireOp",EDGE,"E85"),sQuery(id+"F0.wireOp",EDGE,"E86"),sQuery(id+"F0.wireOp",EDGE,"E87"),sQuery(id+"F0.wireOp",EDGE,"E88"),sQuery(id+"F0.wireOp",EDGE,"E89"),sQuery(id+"F0.wireOp",EDGE,"E90"),sQuery(id+"F0.wireOp",EDGE,"E91"),sQuery(id+"F0.wireOp",EDGE,"E92"),sQuery(id+"F0.wireOp",EDGE,"E93"),sQuery(id+"F0.wireOp",EDGE,"E94"),sQuery(id+"F0.wireOp",EDGE,"E95"),sQuery(id+"F0.wireOp",EDGE,"E96"),sQuery(id+"F0.wireOp",EDGE,"E97"),sQuery(id+"F0.wireOp",EDGE,"E98"),sQuery(id+"F0.wireOp",EDGE,"E99"),sQuery(id+"F0.wireOp",EDGE,"E100"),sQuery(id+"F0.wireOp",EDGE,"E101"),sQuery(id+"F0.wireOp",EDGE,"E102"),sQuery(id+"F0.wireOp",EDGE,"E103"),sQuery(id+"F0.wireOp",EDGE,"E104")])]}),"instanceName":"15"});
            var Q7;
            Q7=makeQuery(id+"F2.opPattern","COPY",BODY,{"derivedFrom":makeQuery(id+"F1.opExtrude","SWEPT_BODY",BODY,{"disambiguationData":[OSD([sQuery(id+"F0.wireOp",EDGE,"E1"),sQuery(id+"F0.wireOp",EDGE,"E2"),sQuery(id+"F0.wireOp",EDGE,"E3"),sQuery(id+"F0.wireOp",EDGE,"E4"),sQuery(id+"F0.wireOp",EDGE,"E5"),sQuery(id+"F0.wireOp",EDGE,"E6"),sQuery(id+"F0.wireOp",EDGE,"E7"),sQuery(id+"F0.wireOp",EDGE,"E8"),sQuery(id+"F0.wireOp",EDGE,"E9"),sQuery(id+"F0.wireOp",EDGE,"E10"),sQuery(id+"F0.wireOp",EDGE,"E11"),sQuery(id+"F0.wireOp",EDGE,"E12"),sQuery(id+"F0.wireOp",EDGE,"E13"),sQuery(id+"F0.wireOp",EDGE,"E14"),sQuery(id+"F0.wireOp",EDGE,"E15"),sQuery(id+"F0.wireOp",EDGE,"E16"),sQuery(id+"F0.wireOp",EDGE,"E17"),sQuery(id+"F0.wireOp",EDGE,"E18"),sQuery(id+"F0.wireOp",EDGE,"E19"),sQuery(id+"F0.wireOp",EDGE,"E20"),sQuery(id+"F0.wireOp",EDGE,"E21"),sQuery(id+"F0.wireOp",EDGE,"E22"),sQuery(id+"F0.wireOp",EDGE,"E23"),sQuery(id+"F0.wireOp",EDGE,"E24"),sQuery(id+"F0.wireOp",EDGE,"E25"),sQuery(id+"F0.wireOp",EDGE,"E26"),sQuery(id+"F0.wireOp",EDGE,"E27"),sQuery(id+"F0.wireOp",EDGE,"E28"),sQuery(id+"F0.wireOp",EDGE,"E29"),sQuery(id+"F0.wireOp",EDGE,"E30"),sQuery(id+"F0.wireOp",EDGE,"E31"),sQuery(id+"F0.wireOp",EDGE,"E32"),sQuery(id+"F0.wireOp",EDGE,"E33"),sQuery(id+"F0.wireOp",EDGE,"E34"),sQuery(id+"F0.wireOp",EDGE,"E35"),sQuery(id+"F0.wireOp",EDGE,"E36"),sQuery(id+"F0.wireOp",EDGE,"E37"),sQuery(id+"F0.wireOp",EDGE,"E38"),sQuery(id+"F0.wireOp",EDGE,"E39"),sQuery(id+"F0.wireOp",EDGE,"E40"),sQuery(id+"F0.wireOp",EDGE,"E41"),sQuery(id+"F0.wireOp",EDGE,"E42"),sQuery(id+"F0.wireOp",EDGE,"E43"),sQuery(id+"F0.wireOp",EDGE,"E44"),sQuery(id+"F0.wireOp",EDGE,"E45"),sQuery(id+"F0.wireOp",EDGE,"E46"),sQuery(id+"F0.wireOp",EDGE,"E47"),sQuery(id+"F0.wireOp",EDGE,"E48"),sQuery(id+"F0.wireOp",EDGE,"E49"),sQuery(id+"F0.wireOp",EDGE,"E50"),sQuery(id+"F0.wireOp",EDGE,"E51"),sQuery(id+"F0.wireOp",EDGE,"E52"),sQuery(id+"F0.wireOp",EDGE,"E53"),sQuery(id+"F0.wireOp",EDGE,"E54"),sQuery(id+"F0.wireOp",EDGE,"E55"),sQuery(id+"F0.wireOp",EDGE,"E56"),sQuery(id+"F0.wireOp",EDGE,"E57"),sQuery(id+"F0.wireOp",EDGE,"E58"),sQuery(id+"F0.wireOp",EDGE,"E59"),sQuery(id+"F0.wireOp",EDGE,"E60"),sQuery(id+"F0.wireOp",EDGE,"E61"),sQuery(id+"F0.wireOp",EDGE,"E62"),sQuery(id+"F0.wireOp",EDGE,"E63"),sQuery(id+"F0.wireOp",EDGE,"E64"),sQuery(id+"F0.wireOp",EDGE,"E65"),sQuery(id+"F0.wireOp",EDGE,"E66"),sQuery(id+"F0.wireOp",EDGE,"E67"),sQuery(id+"F0.wireOp",EDGE,"E68"),sQuery(id+"F0.wireOp",EDGE,"E69"),sQuery(id+"F0.wireOp",EDGE,"E70"),sQuery(id+"F0.wireOp",EDGE,"E71"),sQuery(id+"F0.wireOp",EDGE,"E72"),sQuery(id+"F0.wireOp",EDGE,"E73"),sQuery(id+"F0.wireOp",EDGE,"E74"),sQuery(id+"F0.wireOp",EDGE,"E75"),sQuery(id+"F0.wireOp",EDGE,"E76"),sQuery(id+"F0.wireOp",EDGE,"E77"),sQuery(id+"F0.wireOp",EDGE,"E78"),sQuery(id+"F0.wireOp",EDGE,"E79"),sQuery(id+"F0.wireOp",EDGE,"E80"),sQuery(id+"F0.wireOp",EDGE,"E81"),sQuery(id+"F0.wireOp",EDGE,"E82"),sQuery(id+"F0.wireOp",EDGE,"E83"),sQuery(id+"F0.wireOp",EDGE,"E84"),sQuery(id+"F0.wireOp",EDGE,"E85"),sQuery(id+"F0.wireOp",EDGE,"E86"),sQuery(id+"F0.wireOp",EDGE,"E87"),sQuery(id+"F0.wireOp",EDGE,"E88"),sQuery(id+"F0.wireOp",EDGE,"E89"),sQuery(id+"F0.wireOp",EDGE,"E90"),sQuery(id+"F0.wireOp",EDGE,"E91"),sQuery(id+"F0.wireOp",EDGE,"E92"),sQuery(id+"F0.wireOp",EDGE,"E93"),sQuery(id+"F0.wireOp",EDGE,"E94"),sQuery(id+"F0.wireOp",EDGE,"E95"),sQuery(id+"F0.wireOp",EDGE,"E96"),sQuery(id+"F0.wireOp",EDGE,"E97"),sQuery(id+"F0.wireOp",EDGE,"E98"),sQuery(id+"F0.wireOp",EDGE,"E99"),sQuery(id+"F0.wireOp",EDGE,"E100"),sQuery(id+"F0.wireOp",EDGE,"E101"),sQuery(id+"F0.wireOp",EDGE,"E102"),sQuery(id+"F0.wireOp",EDGE,"E103"),sQuery(id+"F0.wireOp",EDGE,"E104")])]}),"instanceName":"16"});
            var Q8;
            Q8=makeQuery(id+"F2.opPattern","COPY",BODY,{"derivedFrom":makeQuery(id+"F1.opExtrude","SWEPT_BODY",BODY,{"disambiguationData":[OSD([sQuery(id+"F0.wireOp",EDGE,"E1"),sQuery(id+"F0.wireOp",EDGE,"E2"),sQuery(id+"F0.wireOp",EDGE,"E3"),sQuery(id+"F0.wireOp",EDGE,"E4"),sQuery(id+"F0.wireOp",EDGE,"E5"),sQuery(id+"F0.wireOp",EDGE,"E6"),sQuery(id+"F0.wireOp",EDGE,"E7"),sQuery(id+"F0.wireOp",EDGE,"E8"),sQuery(id+"F0.wireOp",EDGE,"E9"),sQuery(id+"F0.wireOp",EDGE,"E10"),sQuery(id+"F0.wireOp",EDGE,"E11"),sQuery(id+"F0.wireOp",EDGE,"E12"),sQuery(id+"F0.wireOp",EDGE,"E13"),sQuery(id+"F0.wireOp",EDGE,"E14"),sQuery(id+"F0.wireOp",EDGE,"E15"),sQuery(id+"F0.wireOp",EDGE,"E16"),sQuery(id+"F0.wireOp",EDGE,"E17"),sQuery(id+"F0.wireOp",EDGE,"E18"),sQuery(id+"F0.wireOp",EDGE,"E19"),sQuery(id+"F0.wireOp",EDGE,"E20"),sQuery(id+"F0.wireOp",EDGE,"E21"),sQuery(id+"F0.wireOp",EDGE,"E22"),sQuery(id+"F0.wireOp",EDGE,"E23"),sQuery(id+"F0.wireOp",EDGE,"E24"),sQuery(id+"F0.wireOp",EDGE,"E25"),sQuery(id+"F0.wireOp",EDGE,"E26"),sQuery(id+"F0.wireOp",EDGE,"E27"),sQuery(id+"F0.wireOp",EDGE,"E28"),sQuery(id+"F0.wireOp",EDGE,"E29"),sQuery(id+"F0.wireOp",EDGE,"E30"),sQuery(id+"F0.wireOp",EDGE,"E31"),sQuery(id+"F0.wireOp",EDGE,"E32"),sQuery(id+"F0.wireOp",EDGE,"E33"),sQuery(id+"F0.wireOp",EDGE,"E34"),sQuery(id+"F0.wireOp",EDGE,"E35"),sQuery(id+"F0.wireOp",EDGE,"E36"),sQuery(id+"F0.wireOp",EDGE,"E37"),sQuery(id+"F0.wireOp",EDGE,"E38"),sQuery(id+"F0.wireOp",EDGE,"E39"),sQuery(id+"F0.wireOp",EDGE,"E40"),sQuery(id+"F0.wireOp",EDGE,"E41"),sQuery(id+"F0.wireOp",EDGE,"E42"),sQuery(id+"F0.wireOp",EDGE,"E43"),sQuery(id+"F0.wireOp",EDGE,"E44"),sQuery(id+"F0.wireOp",EDGE,"E45"),sQuery(id+"F0.wireOp",EDGE,"E46"),sQuery(id+"F0.wireOp",EDGE,"E47"),sQuery(id+"F0.wireOp",EDGE,"E48"),sQuery(id+"F0.wireOp",EDGE,"E49"),sQuery(id+"F0.wireOp",EDGE,"E50"),sQuery(id+"F0.wireOp",EDGE,"E51"),sQuery(id+"F0.wireOp",EDGE,"E52"),sQuery(id+"F0.wireOp",EDGE,"E53"),sQuery(id+"F0.wireOp",EDGE,"E54"),sQuery(id+"F0.wireOp",EDGE,"E55"),sQuery(id+"F0.wireOp",EDGE,"E56"),sQuery(id+"F0.wireOp",EDGE,"E57"),sQuery(id+"F0.wireOp",EDGE,"E58"),sQuery(id+"F0.wireOp",EDGE,"E59"),sQuery(id+"F0.wireOp",EDGE,"E60"),sQuery(id+"F0.wireOp",EDGE,"E61"),sQuery(id+"F0.wireOp",EDGE,"E62"),sQuery(id+"F0.wireOp",EDGE,"E63"),sQuery(id+"F0.wireOp",EDGE,"E64"),sQuery(id+"F0.wireOp",EDGE,"E65"),sQuery(id+"F0.wireOp",EDGE,"E66"),sQuery(id+"F0.wireOp",EDGE,"E67"),sQuery(id+"F0.wireOp",EDGE,"E68"),sQuery(id+"F0.wireOp",EDGE,"E69"),sQuery(id+"F0.wireOp",EDGE,"E70"),sQuery(id+"F0.wireOp",EDGE,"E71"),sQuery(id+"F0.wireOp",EDGE,"E72"),sQuery(id+"F0.wireOp",EDGE,"E73"),sQuery(id+"F0.wireOp",EDGE,"E74"),sQuery(id+"F0.wireOp",EDGE,"E75"),sQuery(id+"F0.wireOp",EDGE,"E76"),sQuery(id+"F0.wireOp",EDGE,"E77"),sQuery(id+"F0.wireOp",EDGE,"E78"),sQuery(id+"F0.wireOp",EDGE,"E79"),sQuery(id+"F0.wireOp",EDGE,"E80"),sQuery(id+"F0.wireOp",EDGE,"E81"),sQuery(id+"F0.wireOp",EDGE,"E82"),sQuery(id+"F0.wireOp",EDGE,"E83"),sQuery(id+"F0.wireOp",EDGE,"E84"),sQuery(id+"F0.wireOp",EDGE,"E85"),sQuery(id+"F0.wireOp",EDGE,"E86"),sQuery(id+"F0.wireOp",EDGE,"E87"),sQuery(id+"F0.wireOp",EDGE,"E88"),sQuery(id+"F0.wireOp",EDGE,"E89"),sQuery(id+"F0.wireOp",EDGE,"E90"),sQuery(id+"F0.wireOp",EDGE,"E91"),sQuery(id+"F0.wireOp",EDGE,"E92"),sQuery(id+"F0.wireOp",EDGE,"E93"),sQuery(id+"F0.wireOp",EDGE,"E94"),sQuery(id+"F0.wireOp",EDGE,"E95"),sQuery(id+"F0.wireOp",EDGE,"E96"),sQuery(id+"F0.wireOp",EDGE,"E97"),sQuery(id+"F0.wireOp",EDGE,"E98"),sQuery(id+"F0.wireOp",EDGE,"E99"),sQuery(id+"F0.wireOp",EDGE,"E100"),sQuery(id+"F0.wireOp",EDGE,"E101"),sQuery(id+"F0.wireOp",EDGE,"E102"),sQuery(id+"F0.wireOp",EDGE,"E103"),sQuery(id+"F0.wireOp",EDGE,"E104")])]}),"instanceName":"17"});
            var Q9;
            Q9=makeQuery(id+"F2.opPattern","COPY",BODY,{"derivedFrom":makeQuery(id+"F1.opExtrude","SWEPT_BODY",BODY,{"disambiguationData":[OSD([sQuery(id+"F0.wireOp",EDGE,"E1"),sQuery(id+"F0.wireOp",EDGE,"E2"),sQuery(id+"F0.wireOp",EDGE,"E3"),sQuery(id+"F0.wireOp",EDGE,"E4"),sQuery(id+"F0.wireOp",EDGE,"E5"),sQuery(id+"F0.wireOp",EDGE,"E6"),sQuery(id+"F0.wireOp",EDGE,"E7"),sQuery(id+"F0.wireOp",EDGE,"E8"),sQuery(id+"F0.wireOp",EDGE,"E9"),sQuery(id+"F0.wireOp",EDGE,"E10"),sQuery(id+"F0.wireOp",EDGE,"E11"),sQuery(id+"F0.wireOp",EDGE,"E12"),sQuery(id+"F0.wireOp",EDGE,"E13"),sQuery(id+"F0.wireOp",EDGE,"E14"),sQuery(id+"F0.wireOp",EDGE,"E15"),sQuery(id+"F0.wireOp",EDGE,"E16"),sQuery(id+"F0.wireOp",EDGE,"E17"),sQuery(id+"F0.wireOp",EDGE,"E18"),sQuery(id+"F0.wireOp",EDGE,"E19"),sQuery(id+"F0.wireOp",EDGE,"E20"),sQuery(id+"F0.wireOp",EDGE,"E21"),sQuery(id+"F0.wireOp",EDGE,"E22"),sQuery(id+"F0.wireOp",EDGE,"E23"),sQuery(id+"F0.wireOp",EDGE,"E24"),sQuery(id+"F0.wireOp",EDGE,"E25"),sQuery(id+"F0.wireOp",EDGE,"E26"),sQuery(id+"F0.wireOp",EDGE,"E27"),sQuery(id+"F0.wireOp",EDGE,"E28"),sQuery(id+"F0.wireOp",EDGE,"E29"),sQuery(id+"F0.wireOp",EDGE,"E30"),sQuery(id+"F0.wireOp",EDGE,"E31"),sQuery(id+"F0.wireOp",EDGE,"E32"),sQuery(id+"F0.wireOp",EDGE,"E33"),sQuery(id+"F0.wireOp",EDGE,"E34"),sQuery(id+"F0.wireOp",EDGE,"E35"),sQuery(id+"F0.wireOp",EDGE,"E36"),sQuery(id+"F0.wireOp",EDGE,"E37"),sQuery(id+"F0.wireOp",EDGE,"E38"),sQuery(id+"F0.wireOp",EDGE,"E39"),sQuery(id+"F0.wireOp",EDGE,"E40"),sQuery(id+"F0.wireOp",EDGE,"E41"),sQuery(id+"F0.wireOp",EDGE,"E42"),sQuery(id+"F0.wireOp",EDGE,"E43"),sQuery(id+"F0.wireOp",EDGE,"E44"),sQuery(id+"F0.wireOp",EDGE,"E45"),sQuery(id+"F0.wireOp",EDGE,"E46"),sQuery(id+"F0.wireOp",EDGE,"E47"),sQuery(id+"F0.wireOp",EDGE,"E48"),sQuery(id+"F0.wireOp",EDGE,"E49"),sQuery(id+"F0.wireOp",EDGE,"E50"),sQuery(id+"F0.wireOp",EDGE,"E51"),sQuery(id+"F0.wireOp",EDGE,"E52"),sQuery(id+"F0.wireOp",EDGE,"E53"),sQuery(id+"F0.wireOp",EDGE,"E54"),sQuery(id+"F0.wireOp",EDGE,"E55"),sQuery(id+"F0.wireOp",EDGE,"E56"),sQuery(id+"F0.wireOp",EDGE,"E57"),sQuery(id+"F0.wireOp",EDGE,"E58"),sQuery(id+"F0.wireOp",EDGE,"E59"),sQuery(id+"F0.wireOp",EDGE,"E60"),sQuery(id+"F0.wireOp",EDGE,"E61"),sQuery(id+"F0.wireOp",EDGE,"E62"),sQuery(id+"F0.wireOp",EDGE,"E63"),sQuery(id+"F0.wireOp",EDGE,"E64"),sQuery(id+"F0.wireOp",EDGE,"E65"),sQuery(id+"F0.wireOp",EDGE,"E66"),sQuery(id+"F0.wireOp",EDGE,"E67"),sQuery(id+"F0.wireOp",EDGE,"E68"),sQuery(id+"F0.wireOp",EDGE,"E69"),sQuery(id+"F0.wireOp",EDGE,"E70"),sQuery(id+"F0.wireOp",EDGE,"E71"),sQuery(id+"F0.wireOp",EDGE,"E72"),sQuery(id+"F0.wireOp",EDGE,"E73"),sQuery(id+"F0.wireOp",EDGE,"E74"),sQuery(id+"F0.wireOp",EDGE,"E75"),sQuery(id+"F0.wireOp",EDGE,"E76"),sQuery(id+"F0.wireOp",EDGE,"E77"),sQuery(id+"F0.wireOp",EDGE,"E78"),sQuery(id+"F0.wireOp",EDGE,"E79"),sQuery(id+"F0.wireOp",EDGE,"E80"),sQuery(id+"F0.wireOp",EDGE,"E81"),sQuery(id+"F0.wireOp",EDGE,"E82"),sQuery(id+"F0.wireOp",EDGE,"E83"),sQuery(id+"F0.wireOp",EDGE,"E84"),sQuery(id+"F0.wireOp",EDGE,"E85"),sQuery(id+"F0.wireOp",EDGE,"E86"),sQuery(id+"F0.wireOp",EDGE,"E87"),sQuery(id+"F0.wireOp",EDGE,"E88"),sQuery(id+"F0.wireOp",EDGE,"E89"),sQuery(id+"F0.wireOp",EDGE,"E90"),sQuery(id+"F0.wireOp",EDGE,"E91"),sQuery(id+"F0.wireOp",EDGE,"E92"),sQuery(id+"F0.wireOp",EDGE,"E93"),sQuery(id+"F0.wireOp",EDGE,"E94"),sQuery(id+"F0.wireOp",EDGE,"E95"),sQuery(id+"F0.wireOp",EDGE,"E96"),sQuery(id+"F0.wireOp",EDGE,"E97"),sQuery(id+"F0.wireOp",EDGE,"E98"),sQuery(id+"F0.wireOp",EDGE,"E99"),sQuery(id+"F0.wireOp",EDGE,"E100"),sQuery(id+"F0.wireOp",EDGE,"E101"),sQuery(id+"F0.wireOp",EDGE,"E102"),sQuery(id+"F0.wireOp",EDGE,"E103"),sQuery(id+"F0.wireOp",EDGE,"E104")])]}),"instanceName":"18"});
            var Q10;
            Q10=makeQuery(id+"F2.opPattern","COPY",BODY,{"derivedFrom":makeQuery(id+"F1.opExtrude","SWEPT_BODY",BODY,{"disambiguationData":[OSD([sQuery(id+"F0.wireOp",EDGE,"E1"),sQuery(id+"F0.wireOp",EDGE,"E2"),sQuery(id+"F0.wireOp",EDGE,"E3"),sQuery(id+"F0.wireOp",EDGE,"E4"),sQuery(id+"F0.wireOp",EDGE,"E5"),sQuery(id+"F0.wireOp",EDGE,"E6"),sQuery(id+"F0.wireOp",EDGE,"E7"),sQuery(id+"F0.wireOp",EDGE,"E8"),sQuery(id+"F0.wireOp",EDGE,"E9"),sQuery(id+"F0.wireOp",EDGE,"E10"),sQuery(id+"F0.wireOp",EDGE,"E11"),sQuery(id+"F0.wireOp",EDGE,"E12"),sQuery(id+"F0.wireOp",EDGE,"E13"),sQuery(id+"F0.wireOp",EDGE,"E14"),sQuery(id+"F0.wireOp",EDGE,"E15"),sQuery(id+"F0.wireOp",EDGE,"E16"),sQuery(id+"F0.wireOp",EDGE,"E17"),sQuery(id+"F0.wireOp",EDGE,"E18"),sQuery(id+"F0.wireOp",EDGE,"E19"),sQuery(id+"F0.wireOp",EDGE,"E20"),sQuery(id+"F0.wireOp",EDGE,"E21"),sQuery(id+"F0.wireOp",EDGE,"E22"),sQuery(id+"F0.wireOp",EDGE,"E23"),sQuery(id+"F0.wireOp",EDGE,"E24"),sQuery(id+"F0.wireOp",EDGE,"E25"),sQuery(id+"F0.wireOp",EDGE,"E26"),sQuery(id+"F0.wireOp",EDGE,"E27"),sQuery(id+"F0.wireOp",EDGE,"E28"),sQuery(id+"F0.wireOp",EDGE,"E29"),sQuery(id+"F0.wireOp",EDGE,"E30"),sQuery(id+"F0.wireOp",EDGE,"E31"),sQuery(id+"F0.wireOp",EDGE,"E32"),sQuery(id+"F0.wireOp",EDGE,"E33"),sQuery(id+"F0.wireOp",EDGE,"E34"),sQuery(id+"F0.wireOp",EDGE,"E35"),sQuery(id+"F0.wireOp",EDGE,"E36"),sQuery(id+"F0.wireOp",EDGE,"E37"),sQuery(id+"F0.wireOp",EDGE,"E38"),sQuery(id+"F0.wireOp",EDGE,"E39"),sQuery(id+"F0.wireOp",EDGE,"E40"),sQuery(id+"F0.wireOp",EDGE,"E41"),sQuery(id+"F0.wireOp",EDGE,"E42"),sQuery(id+"F0.wireOp",EDGE,"E43"),sQuery(id+"F0.wireOp",EDGE,"E44"),sQuery(id+"F0.wireOp",EDGE,"E45"),sQuery(id+"F0.wireOp",EDGE,"E46"),sQuery(id+"F0.wireOp",EDGE,"E47"),sQuery(id+"F0.wireOp",EDGE,"E48"),sQuery(id+"F0.wireOp",EDGE,"E49"),sQuery(id+"F0.wireOp",EDGE,"E50"),sQuery(id+"F0.wireOp",EDGE,"E51"),sQuery(id+"F0.wireOp",EDGE,"E52"),sQuery(id+"F0.wireOp",EDGE,"E53"),sQuery(id+"F0.wireOp",EDGE,"E54"),sQuery(id+"F0.wireOp",EDGE,"E55"),sQuery(id+"F0.wireOp",EDGE,"E56"),sQuery(id+"F0.wireOp",EDGE,"E57"),sQuery(id+"F0.wireOp",EDGE,"E58"),sQuery(id+"F0.wireOp",EDGE,"E59"),sQuery(id+"F0.wireOp",EDGE,"E60"),sQuery(id+"F0.wireOp",EDGE,"E61"),sQuery(id+"F0.wireOp",EDGE,"E62"),sQuery(id+"F0.wireOp",EDGE,"E63"),sQuery(id+"F0.wireOp",EDGE,"E64"),sQuery(id+"F0.wireOp",EDGE,"E65"),sQuery(id+"F0.wireOp",EDGE,"E66"),sQuery(id+"F0.wireOp",EDGE,"E67"),sQuery(id+"F0.wireOp",EDGE,"E68"),sQuery(id+"F0.wireOp",EDGE,"E69"),sQuery(id+"F0.wireOp",EDGE,"E70"),sQuery(id+"F0.wireOp",EDGE,"E71"),sQuery(id+"F0.wireOp",EDGE,"E72"),sQuery(id+"F0.wireOp",EDGE,"E73"),sQuery(id+"F0.wireOp",EDGE,"E74"),sQuery(id+"F0.wireOp",EDGE,"E75"),sQuery(id+"F0.wireOp",EDGE,"E76"),sQuery(id+"F0.wireOp",EDGE,"E77"),sQuery(id+"F0.wireOp",EDGE,"E78"),sQuery(id+"F0.wireOp",EDGE,"E79"),sQuery(id+"F0.wireOp",EDGE,"E80"),sQuery(id+"F0.wireOp",EDGE,"E81"),sQuery(id+"F0.wireOp",EDGE,"E82"),sQuery(id+"F0.wireOp",EDGE,"E83"),sQuery(id+"F0.wireOp",EDGE,"E84"),sQuery(id+"F0.wireOp",EDGE,"E85"),sQuery(id+"F0.wireOp",EDGE,"E86"),sQuery(id+"F0.wireOp",EDGE,"E87"),sQuery(id+"F0.wireOp",EDGE,"E88"),sQuery(id+"F0.wireOp",EDGE,"E89"),sQuery(id+"F0.wireOp",EDGE,"E90"),sQuery(id+"F0.wireOp",EDGE,"E91"),sQuery(id+"F0.wireOp",EDGE,"E92"),sQuery(id+"F0.wireOp",EDGE,"E93"),sQuery(id+"F0.wireOp",EDGE,"E94"),sQuery(id+"F0.wireOp",EDGE,"E95"),sQuery(id+"F0.wireOp",EDGE,"E96"),sQuery(id+"F0.wireOp",EDGE,"E97"),sQuery(id+"F0.wireOp",EDGE,"E98"),sQuery(id+"F0.wireOp",EDGE,"E99"),sQuery(id+"F0.wireOp",EDGE,"E100"),sQuery(id+"F0.wireOp",EDGE,"E101"),sQuery(id+"F0.wireOp",EDGE,"E102"),sQuery(id+"F0.wireOp",EDGE,"E103"),sQuery(id+"F0.wireOp",EDGE,"E104")])]}),"instanceName":"19"});
            var Q11;
            Q11=makeQuery(id+"F2.opPattern","COPY",BODY,{"derivedFrom":makeQuery(id+"F1.opExtrude","SWEPT_BODY",BODY,{"disambiguationData":[OSD([sQuery(id+"F0.wireOp",EDGE,"E1"),sQuery(id+"F0.wireOp",EDGE,"E2"),sQuery(id+"F0.wireOp",EDGE,"E3"),sQuery(id+"F0.wireOp",EDGE,"E4"),sQuery(id+"F0.wireOp",EDGE,"E5"),sQuery(id+"F0.wireOp",EDGE,"E6"),sQuery(id+"F0.wireOp",EDGE,"E7"),sQuery(id+"F0.wireOp",EDGE,"E8"),sQuery(id+"F0.wireOp",EDGE,"E9"),sQuery(id+"F0.wireOp",EDGE,"E10"),sQuery(id+"F0.wireOp",EDGE,"E11"),sQuery(id+"F0.wireOp",EDGE,"E12"),sQuery(id+"F0.wireOp",EDGE,"E13"),sQuery(id+"F0.wireOp",EDGE,"E14"),sQuery(id+"F0.wireOp",EDGE,"E15"),sQuery(id+"F0.wireOp",EDGE,"E16"),sQuery(id+"F0.wireOp",EDGE,"E17"),sQuery(id+"F0.wireOp",EDGE,"E18"),sQuery(id+"F0.wireOp",EDGE,"E19"),sQuery(id+"F0.wireOp",EDGE,"E20"),sQuery(id+"F0.wireOp",EDGE,"E21"),sQuery(id+"F0.wireOp",EDGE,"E22"),sQuery(id+"F0.wireOp",EDGE,"E23"),sQuery(id+"F0.wireOp",EDGE,"E24"),sQuery(id+"F0.wireOp",EDGE,"E25"),sQuery(id+"F0.wireOp",EDGE,"E26"),sQuery(id+"F0.wireOp",EDGE,"E27"),sQuery(id+"F0.wireOp",EDGE,"E28"),sQuery(id+"F0.wireOp",EDGE,"E29"),sQuery(id+"F0.wireOp",EDGE,"E30"),sQuery(id+"F0.wireOp",EDGE,"E31"),sQuery(id+"F0.wireOp",EDGE,"E32"),sQuery(id+"F0.wireOp",EDGE,"E33"),sQuery(id+"F0.wireOp",EDGE,"E34"),sQuery(id+"F0.wireOp",EDGE,"E35"),sQuery(id+"F0.wireOp",EDGE,"E36"),sQuery(id+"F0.wireOp",EDGE,"E37"),sQuery(id+"F0.wireOp",EDGE,"E38"),sQuery(id+"F0.wireOp",EDGE,"E39"),sQuery(id+"F0.wireOp",EDGE,"E40"),sQuery(id+"F0.wireOp",EDGE,"E41"),sQuery(id+"F0.wireOp",EDGE,"E42"),sQuery(id+"F0.wireOp",EDGE,"E43"),sQuery(id+"F0.wireOp",EDGE,"E44"),sQuery(id+"F0.wireOp",EDGE,"E45"),sQuery(id+"F0.wireOp",EDGE,"E46"),sQuery(id+"F0.wireOp",EDGE,"E47"),sQuery(id+"F0.wireOp",EDGE,"E48"),sQuery(id+"F0.wireOp",EDGE,"E49"),sQuery(id+"F0.wireOp",EDGE,"E50"),sQuery(id+"F0.wireOp",EDGE,"E51"),sQuery(id+"F0.wireOp",EDGE,"E52"),sQuery(id+"F0.wireOp",EDGE,"E53"),sQuery(id+"F0.wireOp",EDGE,"E54"),sQuery(id+"F0.wireOp",EDGE,"E55"),sQuery(id+"F0.wireOp",EDGE,"E56"),sQuery(id+"F0.wireOp",EDGE,"E57"),sQuery(id+"F0.wireOp",EDGE,"E58"),sQuery(id+"F0.wireOp",EDGE,"E59"),sQuery(id+"F0.wireOp",EDGE,"E60"),sQuery(id+"F0.wireOp",EDGE,"E61"),sQuery(id+"F0.wireOp",EDGE,"E62"),sQuery(id+"F0.wireOp",EDGE,"E63"),sQuery(id+"F0.wireOp",EDGE,"E64"),sQuery(id+"F0.wireOp",EDGE,"E65"),sQuery(id+"F0.wireOp",EDGE,"E66"),sQuery(id+"F0.wireOp",EDGE,"E67"),sQuery(id+"F0.wireOp",EDGE,"E68"),sQuery(id+"F0.wireOp",EDGE,"E69"),sQuery(id+"F0.wireOp",EDGE,"E70"),sQuery(id+"F0.wireOp",EDGE,"E71"),sQuery(id+"F0.wireOp",EDGE,"E72"),sQuery(id+"F0.wireOp",EDGE,"E73"),sQuery(id+"F0.wireOp",EDGE,"E74"),sQuery(id+"F0.wireOp",EDGE,"E75"),sQuery(id+"F0.wireOp",EDGE,"E76"),sQuery(id+"F0.wireOp",EDGE,"E77"),sQuery(id+"F0.wireOp",EDGE,"E78"),sQuery(id+"F0.wireOp",EDGE,"E79"),sQuery(id+"F0.wireOp",EDGE,"E80"),sQuery(id+"F0.wireOp",EDGE,"E81"),sQuery(id+"F0.wireOp",EDGE,"E82"),sQuery(id+"F0.wireOp",EDGE,"E83"),sQuery(id+"F0.wireOp",EDGE,"E84"),sQuery(id+"F0.wireOp",EDGE,"E85"),sQuery(id+"F0.wireOp",EDGE,"E86"),sQuery(id+"F0.wireOp",EDGE,"E87"),sQuery(id+"F0.wireOp",EDGE,"E88"),sQuery(id+"F0.wireOp",EDGE,"E89"),sQuery(id+"F0.wireOp",EDGE,"E90"),sQuery(id+"F0.wireOp",EDGE,"E91"),sQuery(id+"F0.wireOp",EDGE,"E92"),sQuery(id+"F0.wireOp",EDGE,"E93"),sQuery(id+"F0.wireOp",EDGE,"E94"),sQuery(id+"F0.wireOp",EDGE,"E95"),sQuery(id+"F0.wireOp",EDGE,"E96"),sQuery(id+"F0.wireOp",EDGE,"E97"),sQuery(id+"F0.wireOp",EDGE,"E98"),sQuery(id+"F0.wireOp",EDGE,"E99"),sQuery(id+"F0.wireOp",EDGE,"E100"),sQuery(id+"F0.wireOp",EDGE,"E101"),sQuery(id+"F0.wireOp",EDGE,"E102"),sQuery(id+"F0.wireOp",EDGE,"E103"),sQuery(id+"F0.wireOp",EDGE,"E104")])]}),"instanceName":"20"});
            var Q12;
            Q12=makeQuery(id+"F2.opPattern","COPY",BODY,{"derivedFrom":makeQuery(id+"F1.opExtrude","SWEPT_BODY",BODY,{"disambiguationData":[OSD([sQuery(id+"F0.wireOp",EDGE,"E1"),sQuery(id+"F0.wireOp",EDGE,"E2"),sQuery(id+"F0.wireOp",EDGE,"E3"),sQuery(id+"F0.wireOp",EDGE,"E4"),sQuery(id+"F0.wireOp",EDGE,"E5"),sQuery(id+"F0.wireOp",EDGE,"E6"),sQuery(id+"F0.wireOp",EDGE,"E7"),sQuery(id+"F0.wireOp",EDGE,"E8"),sQuery(id+"F0.wireOp",EDGE,"E9"),sQuery(id+"F0.wireOp",EDGE,"E10"),sQuery(id+"F0.wireOp",EDGE,"E11"),sQuery(id+"F0.wireOp",EDGE,"E12"),sQuery(id+"F0.wireOp",EDGE,"E13"),sQuery(id+"F0.wireOp",EDGE,"E14"),sQuery(id+"F0.wireOp",EDGE,"E15"),sQuery(id+"F0.wireOp",EDGE,"E16"),sQuery(id+"F0.wireOp",EDGE,"E17"),sQuery(id+"F0.wireOp",EDGE,"E18"),sQuery(id+"F0.wireOp",EDGE,"E19"),sQuery(id+"F0.wireOp",EDGE,"E20"),sQuery(id+"F0.wireOp",EDGE,"E21"),sQuery(id+"F0.wireOp",EDGE,"E22"),sQuery(id+"F0.wireOp",EDGE,"E23"),sQuery(id+"F0.wireOp",EDGE,"E24"),sQuery(id+"F0.wireOp",EDGE,"E25"),sQuery(id+"F0.wireOp",EDGE,"E26"),sQuery(id+"F0.wireOp",EDGE,"E27"),sQuery(id+"F0.wireOp",EDGE,"E28"),sQuery(id+"F0.wireOp",EDGE,"E29"),sQuery(id+"F0.wireOp",EDGE,"E30"),sQuery(id+"F0.wireOp",EDGE,"E31"),sQuery(id+"F0.wireOp",EDGE,"E32"),sQuery(id+"F0.wireOp",EDGE,"E33"),sQuery(id+"F0.wireOp",EDGE,"E34"),sQuery(id+"F0.wireOp",EDGE,"E35"),sQuery(id+"F0.wireOp",EDGE,"E36"),sQuery(id+"F0.wireOp",EDGE,"E37"),sQuery(id+"F0.wireOp",EDGE,"E38"),sQuery(id+"F0.wireOp",EDGE,"E39"),sQuery(id+"F0.wireOp",EDGE,"E40"),sQuery(id+"F0.wireOp",EDGE,"E41"),sQuery(id+"F0.wireOp",EDGE,"E42"),sQuery(id+"F0.wireOp",EDGE,"E43"),sQuery(id+"F0.wireOp",EDGE,"E44"),sQuery(id+"F0.wireOp",EDGE,"E45"),sQuery(id+"F0.wireOp",EDGE,"E46"),sQuery(id+"F0.wireOp",EDGE,"E47"),sQuery(id+"F0.wireOp",EDGE,"E48"),sQuery(id+"F0.wireOp",EDGE,"E49"),sQuery(id+"F0.wireOp",EDGE,"E50"),sQuery(id+"F0.wireOp",EDGE,"E51"),sQuery(id+"F0.wireOp",EDGE,"E52"),sQuery(id+"F0.wireOp",EDGE,"E53"),sQuery(id+"F0.wireOp",EDGE,"E54"),sQuery(id+"F0.wireOp",EDGE,"E55"),sQuery(id+"F0.wireOp",EDGE,"E56"),sQuery(id+"F0.wireOp",EDGE,"E57"),sQuery(id+"F0.wireOp",EDGE,"E58"),sQuery(id+"F0.wireOp",EDGE,"E59"),sQuery(id+"F0.wireOp",EDGE,"E60"),sQuery(id+"F0.wireOp",EDGE,"E61"),sQuery(id+"F0.wireOp",EDGE,"E62"),sQuery(id+"F0.wireOp",EDGE,"E63"),sQuery(id+"F0.wireOp",EDGE,"E64"),sQuery(id+"F0.wireOp",EDGE,"E65"),sQuery(id+"F0.wireOp",EDGE,"E66"),sQuery(id+"F0.wireOp",EDGE,"E67"),sQuery(id+"F0.wireOp",EDGE,"E68"),sQuery(id+"F0.wireOp",EDGE,"E69"),sQuery(id+"F0.wireOp",EDGE,"E70"),sQuery(id+"F0.wireOp",EDGE,"E71"),sQuery(id+"F0.wireOp",EDGE,"E72"),sQuery(id+"F0.wireOp",EDGE,"E73"),sQuery(id+"F0.wireOp",EDGE,"E74"),sQuery(id+"F0.wireOp",EDGE,"E75"),sQuery(id+"F0.wireOp",EDGE,"E76"),sQuery(id+"F0.wireOp",EDGE,"E77"),sQuery(id+"F0.wireOp",EDGE,"E78"),sQuery(id+"F0.wireOp",EDGE,"E79"),sQuery(id+"F0.wireOp",EDGE,"E80"),sQuery(id+"F0.wireOp",EDGE,"E81"),sQuery(id+"F0.wireOp",EDGE,"E82"),sQuery(id+"F0.wireOp",EDGE,"E83"),sQuery(id+"F0.wireOp",EDGE,"E84"),sQuery(id+"F0.wireOp",EDGE,"E85"),sQuery(id+"F0.wireOp",EDGE,"E86"),sQuery(id+"F0.wireOp",EDGE,"E87"),sQuery(id+"F0.wireOp",EDGE,"E88"),sQuery(id+"F0.wireOp",EDGE,"E89"),sQuery(id+"F0.wireOp",EDGE,"E90"),sQuery(id+"F0.wireOp",EDGE,"E91"),sQuery(id+"F0.wireOp",EDGE,"E92"),sQuery(id+"F0.wireOp",EDGE,"E93"),sQuery(id+"F0.wireOp",EDGE,"E94"),sQuery(id+"F0.wireOp",EDGE,"E95"),sQuery(id+"F0.wireOp",EDGE,"E96"),sQuery(id+"F0.wireOp",EDGE,"E97"),sQuery(id+"F0.wireOp",EDGE,"E98"),sQuery(id+"F0.wireOp",EDGE,"E99"),sQuery(id+"F0.wireOp",EDGE,"E100"),sQuery(id+"F0.wireOp",EDGE,"E101"),sQuery(id+"F0.wireOp",EDGE,"E102"),sQuery(id+"F0.wireOp",EDGE,"E103"),sQuery(id+"F0.wireOp",EDGE,"E104")])]}),"instanceName":"21"});
            var Q13;
            Q13=makeQuery(id+"F2.opPattern","COPY",BODY,{"derivedFrom":makeQuery(id+"F1.opExtrude","SWEPT_BODY",BODY,{"disambiguationData":[OSD([sQuery(id+"F0.wireOp",EDGE,"E1"),sQuery(id+"F0.wireOp",EDGE,"E2"),sQuery(id+"F0.wireOp",EDGE,"E3"),sQuery(id+"F0.wireOp",EDGE,"E4"),sQuery(id+"F0.wireOp",EDGE,"E5"),sQuery(id+"F0.wireOp",EDGE,"E6"),sQuery(id+"F0.wireOp",EDGE,"E7"),sQuery(id+"F0.wireOp",EDGE,"E8"),sQuery(id+"F0.wireOp",EDGE,"E9"),sQuery(id+"F0.wireOp",EDGE,"E10"),sQuery(id+"F0.wireOp",EDGE,"E11"),sQuery(id+"F0.wireOp",EDGE,"E12"),sQuery(id+"F0.wireOp",EDGE,"E13"),sQuery(id+"F0.wireOp",EDGE,"E14"),sQuery(id+"F0.wireOp",EDGE,"E15"),sQuery(id+"F0.wireOp",EDGE,"E16"),sQuery(id+"F0.wireOp",EDGE,"E17"),sQuery(id+"F0.wireOp",EDGE,"E18"),sQuery(id+"F0.wireOp",EDGE,"E19"),sQuery(id+"F0.wireOp",EDGE,"E20"),sQuery(id+"F0.wireOp",EDGE,"E21"),sQuery(id+"F0.wireOp",EDGE,"E22"),sQuery(id+"F0.wireOp",EDGE,"E23"),sQuery(id+"F0.wireOp",EDGE,"E24"),sQuery(id+"F0.wireOp",EDGE,"E25"),sQuery(id+"F0.wireOp",EDGE,"E26"),sQuery(id+"F0.wireOp",EDGE,"E27"),sQuery(id+"F0.wireOp",EDGE,"E28"),sQuery(id+"F0.wireOp",EDGE,"E29"),sQuery(id+"F0.wireOp",EDGE,"E30"),sQuery(id+"F0.wireOp",EDGE,"E31"),sQuery(id+"F0.wireOp",EDGE,"E32"),sQuery(id+"F0.wireOp",EDGE,"E33"),sQuery(id+"F0.wireOp",EDGE,"E34"),sQuery(id+"F0.wireOp",EDGE,"E35"),sQuery(id+"F0.wireOp",EDGE,"E36"),sQuery(id+"F0.wireOp",EDGE,"E37"),sQuery(id+"F0.wireOp",EDGE,"E38"),sQuery(id+"F0.wireOp",EDGE,"E39"),sQuery(id+"F0.wireOp",EDGE,"E40"),sQuery(id+"F0.wireOp",EDGE,"E41"),sQuery(id+"F0.wireOp",EDGE,"E42"),sQuery(id+"F0.wireOp",EDGE,"E43"),sQuery(id+"F0.wireOp",EDGE,"E44"),sQuery(id+"F0.wireOp",EDGE,"E45"),sQuery(id+"F0.wireOp",EDGE,"E46"),sQuery(id+"F0.wireOp",EDGE,"E47"),sQuery(id+"F0.wireOp",EDGE,"E48"),sQuery(id+"F0.wireOp",EDGE,"E49"),sQuery(id+"F0.wireOp",EDGE,"E50"),sQuery(id+"F0.wireOp",EDGE,"E51"),sQuery(id+"F0.wireOp",EDGE,"E52"),sQuery(id+"F0.wireOp",EDGE,"E53"),sQuery(id+"F0.wireOp",EDGE,"E54"),sQuery(id+"F0.wireOp",EDGE,"E55"),sQuery(id+"F0.wireOp",EDGE,"E56"),sQuery(id+"F0.wireOp",EDGE,"E57"),sQuery(id+"F0.wireOp",EDGE,"E58"),sQuery(id+"F0.wireOp",EDGE,"E59"),sQuery(id+"F0.wireOp",EDGE,"E60"),sQuery(id+"F0.wireOp",EDGE,"E61"),sQuery(id+"F0.wireOp",EDGE,"E62"),sQuery(id+"F0.wireOp",EDGE,"E63"),sQuery(id+"F0.wireOp",EDGE,"E64"),sQuery(id+"F0.wireOp",EDGE,"E65"),sQuery(id+"F0.wireOp",EDGE,"E66"),sQuery(id+"F0.wireOp",EDGE,"E67"),sQuery(id+"F0.wireOp",EDGE,"E68"),sQuery(id+"F0.wireOp",EDGE,"E69"),sQuery(id+"F0.wireOp",EDGE,"E70"),sQuery(id+"F0.wireOp",EDGE,"E71"),sQuery(id+"F0.wireOp",EDGE,"E72"),sQuery(id+"F0.wireOp",EDGE,"E73"),sQuery(id+"F0.wireOp",EDGE,"E74"),sQuery(id+"F0.wireOp",EDGE,"E75"),sQuery(id+"F0.wireOp",EDGE,"E76"),sQuery(id+"F0.wireOp",EDGE,"E77"),sQuery(id+"F0.wireOp",EDGE,"E78"),sQuery(id+"F0.wireOp",EDGE,"E79"),sQuery(id+"F0.wireOp",EDGE,"E80"),sQuery(id+"F0.wireOp",EDGE,"E81"),sQuery(id+"F0.wireOp",EDGE,"E82"),sQuery(id+"F0.wireOp",EDGE,"E83"),sQuery(id+"F0.wireOp",EDGE,"E84"),sQuery(id+"F0.wireOp",EDGE,"E85"),sQuery(id+"F0.wireOp",EDGE,"E86"),sQuery(id+"F0.wireOp",EDGE,"E87"),sQuery(id+"F0.wireOp",EDGE,"E88"),sQuery(id+"F0.wireOp",EDGE,"E89"),sQuery(id+"F0.wireOp",EDGE,"E90"),sQuery(id+"F0.wireOp",EDGE,"E91"),sQuery(id+"F0.wireOp",EDGE,"E92"),sQuery(id+"F0.wireOp",EDGE,"E93"),sQuery(id+"F0.wireOp",EDGE,"E94"),sQuery(id+"F0.wireOp",EDGE,"E95"),sQuery(id+"F0.wireOp",EDGE,"E96"),sQuery(id+"F0.wireOp",EDGE,"E97"),sQuery(id+"F0.wireOp",EDGE,"E98"),sQuery(id+"F0.wireOp",EDGE,"E99"),sQuery(id+"F0.wireOp",EDGE,"E100"),sQuery(id+"F0.wireOp",EDGE,"E101"),sQuery(id+"F0.wireOp",EDGE,"E102"),sQuery(id+"F0.wireOp",EDGE,"E103"),sQuery(id+"F0.wireOp",EDGE,"E104")])]}),"instanceName":"22"});
            booleanBodies(context, id + "F3", {"operationType" : BooleanOperationType.UNION, "tools" : qUnion([Q0, Q1, Q2, Q3, Q4, Q5, Q6, Q7, Q8, Q9, Q10, Q11, Q12, Q13])});
        }
        {
            var Q0;
            Q0=makeQuery(id+"F1.opExtrude","SWEPT_BODY",BODY,{"disambiguationData":[OSD([sQuery(id+"F0.wireOp",EDGE,"E105")])]});
            var Q1;
            Q1=makeQuery(id+"F2.opPattern","COPY",BODY,{"derivedFrom":makeQuery(id+"F1.opExtrude","SWEPT_BODY",BODY,{"disambiguationData":[OSD([sQuery(id+"F0.wireOp",EDGE,"E1"),sQuery(id+"F0.wireOp",EDGE,"E2"),sQuery(id+"F0.wireOp",EDGE,"E3"),sQuery(id+"F0.wireOp",EDGE,"E4"),sQuery(id+"F0.wireOp",EDGE,"E5"),sQuery(id+"F0.wireOp",EDGE,"E6"),sQuery(id+"F0.wireOp",EDGE,"E7"),sQuery(id+"F0.wireOp",EDGE,"E8"),sQuery(id+"F0.wireOp",EDGE,"E9"),sQuery(id+"F0.wireOp",EDGE,"E10"),sQuery(id+"F0.wireOp",EDGE,"E11"),sQuery(id+"F0.wireOp",EDGE,"E12"),sQuery(id+"F0.wireOp",EDGE,"E13"),sQuery(id+"F0.wireOp",EDGE,"E14"),sQuery(id+"F0.wireOp",EDGE,"E15"),sQuery(id+"F0.wireOp",EDGE,"E16"),sQuery(id+"F0.wireOp",EDGE,"E17"),sQuery(id+"F0.wireOp",EDGE,"E18"),sQuery(id+"F0.wireOp",EDGE,"E19"),sQuery(id+"F0.wireOp",EDGE,"E20"),sQuery(id+"F0.wireOp",EDGE,"E21"),sQuery(id+"F0.wireOp",EDGE,"E22"),sQuery(id+"F0.wireOp",EDGE,"E23"),sQuery(id+"F0.wireOp",EDGE,"E24"),sQuery(id+"F0.wireOp",EDGE,"E25"),sQuery(id+"F0.wireOp",EDGE,"E26"),sQuery(id+"F0.wireOp",EDGE,"E27"),sQuery(id+"F0.wireOp",EDGE,"E28"),sQuery(id+"F0.wireOp",EDGE,"E29"),sQuery(id+"F0.wireOp",EDGE,"E30"),sQuery(id+"F0.wireOp",EDGE,"E31"),sQuery(id+"F0.wireOp",EDGE,"E32"),sQuery(id+"F0.wireOp",EDGE,"E33"),sQuery(id+"F0.wireOp",EDGE,"E34"),sQuery(id+"F0.wireOp",EDGE,"E35"),sQuery(id+"F0.wireOp",EDGE,"E36"),sQuery(id+"F0.wireOp",EDGE,"E37"),sQuery(id+"F0.wireOp",EDGE,"E38"),sQuery(id+"F0.wireOp",EDGE,"E39"),sQuery(id+"F0.wireOp",EDGE,"E40"),sQuery(id+"F0.wireOp",EDGE,"E41"),sQuery(id+"F0.wireOp",EDGE,"E42"),sQuery(id+"F0.wireOp",EDGE,"E43"),sQuery(id+"F0.wireOp",EDGE,"E44"),sQuery(id+"F0.wireOp",EDGE,"E45"),sQuery(id+"F0.wireOp",EDGE,"E46"),sQuery(id+"F0.wireOp",EDGE,"E47"),sQuery(id+"F0.wireOp",EDGE,"E48"),sQuery(id+"F0.wireOp",EDGE,"E49"),sQuery(id+"F0.wireOp",EDGE,"E50"),sQuery(id+"F0.wireOp",EDGE,"E51"),sQuery(id+"F0.wireOp",EDGE,"E52"),sQuery(id+"F0.wireOp",EDGE,"E53"),sQuery(id+"F0.wireOp",EDGE,"E54"),sQuery(id+"F0.wireOp",EDGE,"E55"),sQuery(id+"F0.wireOp",EDGE,"E56"),sQuery(id+"F0.wireOp",EDGE,"E57"),sQuery(id+"F0.wireOp",EDGE,"E58"),sQuery(id+"F0.wireOp",EDGE,"E59"),sQuery(id+"F0.wireOp",EDGE,"E60"),sQuery(id+"F0.wireOp",EDGE,"E61"),sQuery(id+"F0.wireOp",EDGE,"E62"),sQuery(id+"F0.wireOp",EDGE,"E63"),sQuery(id+"F0.wireOp",EDGE,"E64"),sQuery(id+"F0.wireOp",EDGE,"E65"),sQuery(id+"F0.wireOp",EDGE,"E66"),sQuery(id+"F0.wireOp",EDGE,"E67"),sQuery(id+"F0.wireOp",EDGE,"E68"),sQuery(id+"F0.wireOp",EDGE,"E69"),sQuery(id+"F0.wireOp",EDGE,"E70"),sQuery(id+"F0.wireOp",EDGE,"E71"),sQuery(id+"F0.wireOp",EDGE,"E72"),sQuery(id+"F0.wireOp",EDGE,"E73"),sQuery(id+"F0.wireOp",EDGE,"E74"),sQuery(id+"F0.wireOp",EDGE,"E75"),sQuery(id+"F0.wireOp",EDGE,"E76"),sQuery(id+"F0.wireOp",EDGE,"E77"),sQuery(id+"F0.wireOp",EDGE,"E78"),sQuery(id+"F0.wireOp",EDGE,"E79"),sQuery(id+"F0.wireOp",EDGE,"E80"),sQuery(id+"F0.wireOp",EDGE,"E81"),sQuery(id+"F0.wireOp",EDGE,"E82"),sQuery(id+"F0.wireOp",EDGE,"E83"),sQuery(id+"F0.wireOp",EDGE,"E84"),sQuery(id+"F0.wireOp",EDGE,"E85"),sQuery(id+"F0.wireOp",EDGE,"E86"),sQuery(id+"F0.wireOp",EDGE,"E87"),sQuery(id+"F0.wireOp",EDGE,"E88"),sQuery(id+"F0.wireOp",EDGE,"E89"),sQuery(id+"F0.wireOp",EDGE,"E90"),sQuery(id+"F0.wireOp",EDGE,"E91"),sQuery(id+"F0.wireOp",EDGE,"E92"),sQuery(id+"F0.wireOp",EDGE,"E93"),sQuery(id+"F0.wireOp",EDGE,"E94"),sQuery(id+"F0.wireOp",EDGE,"E95"),sQuery(id+"F0.wireOp",EDGE,"E96"),sQuery(id+"F0.wireOp",EDGE,"E97"),sQuery(id+"F0.wireOp",EDGE,"E98"),sQuery(id+"F0.wireOp",EDGE,"E99"),sQuery(id+"F0.wireOp",EDGE,"E100"),sQuery(id+"F0.wireOp",EDGE,"E101"),sQuery(id+"F0.wireOp",EDGE,"E102"),sQuery(id+"F0.wireOp",EDGE,"E103"),sQuery(id+"F0.wireOp",EDGE,"E104")])]}),"instanceName":"1"});
            var Q2;
            Q2=makeQuery(id+"F2.opPattern","COPY",BODY,{"derivedFrom":makeQuery(id+"F1.opExtrude","SWEPT_BODY",BODY,{"disambiguationData":[OSD([sQuery(id+"F0.wireOp",EDGE,"E1"),sQuery(id+"F0.wireOp",EDGE,"E2"),sQuery(id+"F0.wireOp",EDGE,"E3"),sQuery(id+"F0.wireOp",EDGE,"E4"),sQuery(id+"F0.wireOp",EDGE,"E5"),sQuery(id+"F0.wireOp",EDGE,"E6"),sQuery(id+"F0.wireOp",EDGE,"E7"),sQuery(id+"F0.wireOp",EDGE,"E8"),sQuery(id+"F0.wireOp",EDGE,"E9"),sQuery(id+"F0.wireOp",EDGE,"E10"),sQuery(id+"F0.wireOp",EDGE,"E11"),sQuery(id+"F0.wireOp",EDGE,"E12"),sQuery(id+"F0.wireOp",EDGE,"E13"),sQuery(id+"F0.wireOp",EDGE,"E14"),sQuery(id+"F0.wireOp",EDGE,"E15"),sQuery(id+"F0.wireOp",EDGE,"E16"),sQuery(id+"F0.wireOp",EDGE,"E17"),sQuery(id+"F0.wireOp",EDGE,"E18"),sQuery(id+"F0.wireOp",EDGE,"E19"),sQuery(id+"F0.wireOp",EDGE,"E20"),sQuery(id+"F0.wireOp",EDGE,"E21"),sQuery(id+"F0.wireOp",EDGE,"E22"),sQuery(id+"F0.wireOp",EDGE,"E23"),sQuery(id+"F0.wireOp",EDGE,"E24"),sQuery(id+"F0.wireOp",EDGE,"E25"),sQuery(id+"F0.wireOp",EDGE,"E26"),sQuery(id+"F0.wireOp",EDGE,"E27"),sQuery(id+"F0.wireOp",EDGE,"E28"),sQuery(id+"F0.wireOp",EDGE,"E29"),sQuery(id+"F0.wireOp",EDGE,"E30"),sQuery(id+"F0.wireOp",EDGE,"E31"),sQuery(id+"F0.wireOp",EDGE,"E32"),sQuery(id+"F0.wireOp",EDGE,"E33"),sQuery(id+"F0.wireOp",EDGE,"E34"),sQuery(id+"F0.wireOp",EDGE,"E35"),sQuery(id+"F0.wireOp",EDGE,"E36"),sQuery(id+"F0.wireOp",EDGE,"E37"),sQuery(id+"F0.wireOp",EDGE,"E38"),sQuery(id+"F0.wireOp",EDGE,"E39"),sQuery(id+"F0.wireOp",EDGE,"E40"),sQuery(id+"F0.wireOp",EDGE,"E41"),sQuery(id+"F0.wireOp",EDGE,"E42"),sQuery(id+"F0.wireOp",EDGE,"E43"),sQuery(id+"F0.wireOp",EDGE,"E44"),sQuery(id+"F0.wireOp",EDGE,"E45"),sQuery(id+"F0.wireOp",EDGE,"E46"),sQuery(id+"F0.wireOp",EDGE,"E47"),sQuery(id+"F0.wireOp",EDGE,"E48"),sQuery(id+"F0.wireOp",EDGE,"E49"),sQuery(id+"F0.wireOp",EDGE,"E50"),sQuery(id+"F0.wireOp",EDGE,"E51"),sQuery(id+"F0.wireOp",EDGE,"E52"),sQuery(id+"F0.wireOp",EDGE,"E53"),sQuery(id+"F0.wireOp",EDGE,"E54"),sQuery(id+"F0.wireOp",EDGE,"E55"),sQuery(id+"F0.wireOp",EDGE,"E56"),sQuery(id+"F0.wireOp",EDGE,"E57"),sQuery(id+"F0.wireOp",EDGE,"E58"),sQuery(id+"F0.wireOp",EDGE,"E59"),sQuery(id+"F0.wireOp",EDGE,"E60"),sQuery(id+"F0.wireOp",EDGE,"E61"),sQuery(id+"F0.wireOp",EDGE,"E62"),sQuery(id+"F0.wireOp",EDGE,"E63"),sQuery(id+"F0.wireOp",EDGE,"E64"),sQuery(id+"F0.wireOp",EDGE,"E65"),sQuery(id+"F0.wireOp",EDGE,"E66"),sQuery(id+"F0.wireOp",EDGE,"E67"),sQuery(id+"F0.wireOp",EDGE,"E68"),sQuery(id+"F0.wireOp",EDGE,"E69"),sQuery(id+"F0.wireOp",EDGE,"E70"),sQuery(id+"F0.wireOp",EDGE,"E71"),sQuery(id+"F0.wireOp",EDGE,"E72"),sQuery(id+"F0.wireOp",EDGE,"E73"),sQuery(id+"F0.wireOp",EDGE,"E74"),sQuery(id+"F0.wireOp",EDGE,"E75"),sQuery(id+"F0.wireOp",EDGE,"E76"),sQuery(id+"F0.wireOp",EDGE,"E77"),sQuery(id+"F0.wireOp",EDGE,"E78"),sQuery(id+"F0.wireOp",EDGE,"E79"),sQuery(id+"F0.wireOp",EDGE,"E80"),sQuery(id+"F0.wireOp",EDGE,"E81"),sQuery(id+"F0.wireOp",EDGE,"E82"),sQuery(id+"F0.wireOp",EDGE,"E83"),sQuery(id+"F0.wireOp",EDGE,"E84"),sQuery(id+"F0.wireOp",EDGE,"E85"),sQuery(id+"F0.wireOp",EDGE,"E86"),sQuery(id+"F0.wireOp",EDGE,"E87"),sQuery(id+"F0.wireOp",EDGE,"E88"),sQuery(id+"F0.wireOp",EDGE,"E89"),sQuery(id+"F0.wireOp",EDGE,"E90"),sQuery(id+"F0.wireOp",EDGE,"E91"),sQuery(id+"F0.wireOp",EDGE,"E92"),sQuery(id+"F0.wireOp",EDGE,"E93"),sQuery(id+"F0.wireOp",EDGE,"E94"),sQuery(id+"F0.wireOp",EDGE,"E95"),sQuery(id+"F0.wireOp",EDGE,"E96"),sQuery(id+"F0.wireOp",EDGE,"E97"),sQuery(id+"F0.wireOp",EDGE,"E98"),sQuery(id+"F0.wireOp",EDGE,"E99"),sQuery(id+"F0.wireOp",EDGE,"E100"),sQuery(id+"F0.wireOp",EDGE,"E101"),sQuery(id+"F0.wireOp",EDGE,"E102"),sQuery(id+"F0.wireOp",EDGE,"E103"),sQuery(id+"F0.wireOp",EDGE,"E104")])]}),"instanceName":"23"});
            var Q3;
            Q3=makeQuery(id+"F2.opPattern","COPY",BODY,{"derivedFrom":makeQuery(id+"F1.opExtrude","SWEPT_BODY",BODY,{"disambiguationData":[OSD([sQuery(id+"F0.wireOp",EDGE,"E1"),sQuery(id+"F0.wireOp",EDGE,"E2"),sQuery(id+"F0.wireOp",EDGE,"E3"),sQuery(id+"F0.wireOp",EDGE,"E4"),sQuery(id+"F0.wireOp",EDGE,"E5"),sQuery(id+"F0.wireOp",EDGE,"E6"),sQuery(id+"F0.wireOp",EDGE,"E7"),sQuery(id+"F0.wireOp",EDGE,"E8"),sQuery(id+"F0.wireOp",EDGE,"E9"),sQuery(id+"F0.wireOp",EDGE,"E10"),sQuery(id+"F0.wireOp",EDGE,"E11"),sQuery(id+"F0.wireOp",EDGE,"E12"),sQuery(id+"F0.wireOp",EDGE,"E13"),sQuery(id+"F0.wireOp",EDGE,"E14"),sQuery(id+"F0.wireOp",EDGE,"E15"),sQuery(id+"F0.wireOp",EDGE,"E16"),sQuery(id+"F0.wireOp",EDGE,"E17"),sQuery(id+"F0.wireOp",EDGE,"E18"),sQuery(id+"F0.wireOp",EDGE,"E19"),sQuery(id+"F0.wireOp",EDGE,"E20"),sQuery(id+"F0.wireOp",EDGE,"E21"),sQuery(id+"F0.wireOp",EDGE,"E22"),sQuery(id+"F0.wireOp",EDGE,"E23"),sQuery(id+"F0.wireOp",EDGE,"E24"),sQuery(id+"F0.wireOp",EDGE,"E25"),sQuery(id+"F0.wireOp",EDGE,"E26"),sQuery(id+"F0.wireOp",EDGE,"E27"),sQuery(id+"F0.wireOp",EDGE,"E28"),sQuery(id+"F0.wireOp",EDGE,"E29"),sQuery(id+"F0.wireOp",EDGE,"E30"),sQuery(id+"F0.wireOp",EDGE,"E31"),sQuery(id+"F0.wireOp",EDGE,"E32"),sQuery(id+"F0.wireOp",EDGE,"E33"),sQuery(id+"F0.wireOp",EDGE,"E34"),sQuery(id+"F0.wireOp",EDGE,"E35"),sQuery(id+"F0.wireOp",EDGE,"E36"),sQuery(id+"F0.wireOp",EDGE,"E37"),sQuery(id+"F0.wireOp",EDGE,"E38"),sQuery(id+"F0.wireOp",EDGE,"E39"),sQuery(id+"F0.wireOp",EDGE,"E40"),sQuery(id+"F0.wireOp",EDGE,"E41"),sQuery(id+"F0.wireOp",EDGE,"E42"),sQuery(id+"F0.wireOp",EDGE,"E43"),sQuery(id+"F0.wireOp",EDGE,"E44"),sQuery(id+"F0.wireOp",EDGE,"E45"),sQuery(id+"F0.wireOp",EDGE,"E46"),sQuery(id+"F0.wireOp",EDGE,"E47"),sQuery(id+"F0.wireOp",EDGE,"E48"),sQuery(id+"F0.wireOp",EDGE,"E49"),sQuery(id+"F0.wireOp",EDGE,"E50"),sQuery(id+"F0.wireOp",EDGE,"E51"),sQuery(id+"F0.wireOp",EDGE,"E52"),sQuery(id+"F0.wireOp",EDGE,"E53"),sQuery(id+"F0.wireOp",EDGE,"E54"),sQuery(id+"F0.wireOp",EDGE,"E55"),sQuery(id+"F0.wireOp",EDGE,"E56"),sQuery(id+"F0.wireOp",EDGE,"E57"),sQuery(id+"F0.wireOp",EDGE,"E58"),sQuery(id+"F0.wireOp",EDGE,"E59"),sQuery(id+"F0.wireOp",EDGE,"E60"),sQuery(id+"F0.wireOp",EDGE,"E61"),sQuery(id+"F0.wireOp",EDGE,"E62"),sQuery(id+"F0.wireOp",EDGE,"E63"),sQuery(id+"F0.wireOp",EDGE,"E64"),sQuery(id+"F0.wireOp",EDGE,"E65"),sQuery(id+"F0.wireOp",EDGE,"E66"),sQuery(id+"F0.wireOp",EDGE,"E67"),sQuery(id+"F0.wireOp",EDGE,"E68"),sQuery(id+"F0.wireOp",EDGE,"E69"),sQuery(id+"F0.wireOp",EDGE,"E70"),sQuery(id+"F0.wireOp",EDGE,"E71"),sQuery(id+"F0.wireOp",EDGE,"E72"),sQuery(id+"F0.wireOp",EDGE,"E73"),sQuery(id+"F0.wireOp",EDGE,"E74"),sQuery(id+"F0.wireOp",EDGE,"E75"),sQuery(id+"F0.wireOp",EDGE,"E76"),sQuery(id+"F0.wireOp",EDGE,"E77"),sQuery(id+"F0.wireOp",EDGE,"E78"),sQuery(id+"F0.wireOp",EDGE,"E79"),sQuery(id+"F0.wireOp",EDGE,"E80"),sQuery(id+"F0.wireOp",EDGE,"E81"),sQuery(id+"F0.wireOp",EDGE,"E82"),sQuery(id+"F0.wireOp",EDGE,"E83"),sQuery(id+"F0.wireOp",EDGE,"E84"),sQuery(id+"F0.wireOp",EDGE,"E85"),sQuery(id+"F0.wireOp",EDGE,"E86"),sQuery(id+"F0.wireOp",EDGE,"E87"),sQuery(id+"F0.wireOp",EDGE,"E88"),sQuery(id+"F0.wireOp",EDGE,"E89"),sQuery(id+"F0.wireOp",EDGE,"E90"),sQuery(id+"F0.wireOp",EDGE,"E91"),sQuery(id+"F0.wireOp",EDGE,"E92"),sQuery(id+"F0.wireOp",EDGE,"E93"),sQuery(id+"F0.wireOp",EDGE,"E94"),sQuery(id+"F0.wireOp",EDGE,"E95"),sQuery(id+"F0.wireOp",EDGE,"E96"),sQuery(id+"F0.wireOp",EDGE,"E97"),sQuery(id+"F0.wireOp",EDGE,"E98"),sQuery(id+"F0.wireOp",EDGE,"E99"),sQuery(id+"F0.wireOp",EDGE,"E100"),sQuery(id+"F0.wireOp",EDGE,"E101"),sQuery(id+"F0.wireOp",EDGE,"E102"),sQuery(id+"F0.wireOp",EDGE,"E103"),sQuery(id+"F0.wireOp",EDGE,"E104")])]}),"instanceName":"24"});
            var Q4;
            Q4=makeQuery(id+"F2.opPattern","COPY",BODY,{"derivedFrom":makeQuery(id+"F1.opExtrude","SWEPT_BODY",BODY,{"disambiguationData":[OSD([sQuery(id+"F0.wireOp",EDGE,"E1"),sQuery(id+"F0.wireOp",EDGE,"E2"),sQuery(id+"F0.wireOp",EDGE,"E3"),sQuery(id+"F0.wireOp",EDGE,"E4"),sQuery(id+"F0.wireOp",EDGE,"E5"),sQuery(id+"F0.wireOp",EDGE,"E6"),sQuery(id+"F0.wireOp",EDGE,"E7"),sQuery(id+"F0.wireOp",EDGE,"E8"),sQuery(id+"F0.wireOp",EDGE,"E9"),sQuery(id+"F0.wireOp",EDGE,"E10"),sQuery(id+"F0.wireOp",EDGE,"E11"),sQuery(id+"F0.wireOp",EDGE,"E12"),sQuery(id+"F0.wireOp",EDGE,"E13"),sQuery(id+"F0.wireOp",EDGE,"E14"),sQuery(id+"F0.wireOp",EDGE,"E15"),sQuery(id+"F0.wireOp",EDGE,"E16"),sQuery(id+"F0.wireOp",EDGE,"E17"),sQuery(id+"F0.wireOp",EDGE,"E18"),sQuery(id+"F0.wireOp",EDGE,"E19"),sQuery(id+"F0.wireOp",EDGE,"E20"),sQuery(id+"F0.wireOp",EDGE,"E21"),sQuery(id+"F0.wireOp",EDGE,"E22"),sQuery(id+"F0.wireOp",EDGE,"E23"),sQuery(id+"F0.wireOp",EDGE,"E24"),sQuery(id+"F0.wireOp",EDGE,"E25"),sQuery(id+"F0.wireOp",EDGE,"E26"),sQuery(id+"F0.wireOp",EDGE,"E27"),sQuery(id+"F0.wireOp",EDGE,"E28"),sQuery(id+"F0.wireOp",EDGE,"E29"),sQuery(id+"F0.wireOp",EDGE,"E30"),sQuery(id+"F0.wireOp",EDGE,"E31"),sQuery(id+"F0.wireOp",EDGE,"E32"),sQuery(id+"F0.wireOp",EDGE,"E33"),sQuery(id+"F0.wireOp",EDGE,"E34"),sQuery(id+"F0.wireOp",EDGE,"E35"),sQuery(id+"F0.wireOp",EDGE,"E36"),sQuery(id+"F0.wireOp",EDGE,"E37"),sQuery(id+"F0.wireOp",EDGE,"E38"),sQuery(id+"F0.wireOp",EDGE,"E39"),sQuery(id+"F0.wireOp",EDGE,"E40"),sQuery(id+"F0.wireOp",EDGE,"E41"),sQuery(id+"F0.wireOp",EDGE,"E42"),sQuery(id+"F0.wireOp",EDGE,"E43"),sQuery(id+"F0.wireOp",EDGE,"E44"),sQuery(id+"F0.wireOp",EDGE,"E45"),sQuery(id+"F0.wireOp",EDGE,"E46"),sQuery(id+"F0.wireOp",EDGE,"E47"),sQuery(id+"F0.wireOp",EDGE,"E48"),sQuery(id+"F0.wireOp",EDGE,"E49"),sQuery(id+"F0.wireOp",EDGE,"E50"),sQuery(id+"F0.wireOp",EDGE,"E51"),sQuery(id+"F0.wireOp",EDGE,"E52"),sQuery(id+"F0.wireOp",EDGE,"E53"),sQuery(id+"F0.wireOp",EDGE,"E54"),sQuery(id+"F0.wireOp",EDGE,"E55"),sQuery(id+"F0.wireOp",EDGE,"E56"),sQuery(id+"F0.wireOp",EDGE,"E57"),sQuery(id+"F0.wireOp",EDGE,"E58"),sQuery(id+"F0.wireOp",EDGE,"E59"),sQuery(id+"F0.wireOp",EDGE,"E60"),sQuery(id+"F0.wireOp",EDGE,"E61"),sQuery(id+"F0.wireOp",EDGE,"E62"),sQuery(id+"F0.wireOp",EDGE,"E63"),sQuery(id+"F0.wireOp",EDGE,"E64"),sQuery(id+"F0.wireOp",EDGE,"E65"),sQuery(id+"F0.wireOp",EDGE,"E66"),sQuery(id+"F0.wireOp",EDGE,"E67"),sQuery(id+"F0.wireOp",EDGE,"E68"),sQuery(id+"F0.wireOp",EDGE,"E69"),sQuery(id+"F0.wireOp",EDGE,"E70"),sQuery(id+"F0.wireOp",EDGE,"E71"),sQuery(id+"F0.wireOp",EDGE,"E72"),sQuery(id+"F0.wireOp",EDGE,"E73"),sQuery(id+"F0.wireOp",EDGE,"E74"),sQuery(id+"F0.wireOp",EDGE,"E75"),sQuery(id+"F0.wireOp",EDGE,"E76"),sQuery(id+"F0.wireOp",EDGE,"E77"),sQuery(id+"F0.wireOp",EDGE,"E78"),sQuery(id+"F0.wireOp",EDGE,"E79"),sQuery(id+"F0.wireOp",EDGE,"E80"),sQuery(id+"F0.wireOp",EDGE,"E81"),sQuery(id+"F0.wireOp",EDGE,"E82"),sQuery(id+"F0.wireOp",EDGE,"E83"),sQuery(id+"F0.wireOp",EDGE,"E84"),sQuery(id+"F0.wireOp",EDGE,"E85"),sQuery(id+"F0.wireOp",EDGE,"E86"),sQuery(id+"F0.wireOp",EDGE,"E87"),sQuery(id+"F0.wireOp",EDGE,"E88"),sQuery(id+"F0.wireOp",EDGE,"E89"),sQuery(id+"F0.wireOp",EDGE,"E90"),sQuery(id+"F0.wireOp",EDGE,"E91"),sQuery(id+"F0.wireOp",EDGE,"E92"),sQuery(id+"F0.wireOp",EDGE,"E93"),sQuery(id+"F0.wireOp",EDGE,"E94"),sQuery(id+"F0.wireOp",EDGE,"E95"),sQuery(id+"F0.wireOp",EDGE,"E96"),sQuery(id+"F0.wireOp",EDGE,"E97"),sQuery(id+"F0.wireOp",EDGE,"E98"),sQuery(id+"F0.wireOp",EDGE,"E99"),sQuery(id+"F0.wireOp",EDGE,"E100"),sQuery(id+"F0.wireOp",EDGE,"E101"),sQuery(id+"F0.wireOp",EDGE,"E102"),sQuery(id+"F0.wireOp",EDGE,"E103"),sQuery(id+"F0.wireOp",EDGE,"E104")])]}),"instanceName":"25"});
            var Q5;
            Q5=makeQuery(id+"F2.opPattern","COPY",BODY,{"derivedFrom":makeQuery(id+"F1.opExtrude","SWEPT_BODY",BODY,{"disambiguationData":[OSD([sQuery(id+"F0.wireOp",EDGE,"E1"),sQuery(id+"F0.wireOp",EDGE,"E2"),sQuery(id+"F0.wireOp",EDGE,"E3"),sQuery(id+"F0.wireOp",EDGE,"E4"),sQuery(id+"F0.wireOp",EDGE,"E5"),sQuery(id+"F0.wireOp",EDGE,"E6"),sQuery(id+"F0.wireOp",EDGE,"E7"),sQuery(id+"F0.wireOp",EDGE,"E8"),sQuery(id+"F0.wireOp",EDGE,"E9"),sQuery(id+"F0.wireOp",EDGE,"E10"),sQuery(id+"F0.wireOp",EDGE,"E11"),sQuery(id+"F0.wireOp",EDGE,"E12"),sQuery(id+"F0.wireOp",EDGE,"E13"),sQuery(id+"F0.wireOp",EDGE,"E14"),sQuery(id+"F0.wireOp",EDGE,"E15"),sQuery(id+"F0.wireOp",EDGE,"E16"),sQuery(id+"F0.wireOp",EDGE,"E17"),sQuery(id+"F0.wireOp",EDGE,"E18"),sQuery(id+"F0.wireOp",EDGE,"E19"),sQuery(id+"F0.wireOp",EDGE,"E20"),sQuery(id+"F0.wireOp",EDGE,"E21"),sQuery(id+"F0.wireOp",EDGE,"E22"),sQuery(id+"F0.wireOp",EDGE,"E23"),sQuery(id+"F0.wireOp",EDGE,"E24"),sQuery(id+"F0.wireOp",EDGE,"E25"),sQuery(id+"F0.wireOp",EDGE,"E26"),sQuery(id+"F0.wireOp",EDGE,"E27"),sQuery(id+"F0.wireOp",EDGE,"E28"),sQuery(id+"F0.wireOp",EDGE,"E29"),sQuery(id+"F0.wireOp",EDGE,"E30"),sQuery(id+"F0.wireOp",EDGE,"E31"),sQuery(id+"F0.wireOp",EDGE,"E32"),sQuery(id+"F0.wireOp",EDGE,"E33"),sQuery(id+"F0.wireOp",EDGE,"E34"),sQuery(id+"F0.wireOp",EDGE,"E35"),sQuery(id+"F0.wireOp",EDGE,"E36"),sQuery(id+"F0.wireOp",EDGE,"E37"),sQuery(id+"F0.wireOp",EDGE,"E38"),sQuery(id+"F0.wireOp",EDGE,"E39"),sQuery(id+"F0.wireOp",EDGE,"E40"),sQuery(id+"F0.wireOp",EDGE,"E41"),sQuery(id+"F0.wireOp",EDGE,"E42"),sQuery(id+"F0.wireOp",EDGE,"E43"),sQuery(id+"F0.wireOp",EDGE,"E44"),sQuery(id+"F0.wireOp",EDGE,"E45"),sQuery(id+"F0.wireOp",EDGE,"E46"),sQuery(id+"F0.wireOp",EDGE,"E47"),sQuery(id+"F0.wireOp",EDGE,"E48"),sQuery(id+"F0.wireOp",EDGE,"E49"),sQuery(id+"F0.wireOp",EDGE,"E50"),sQuery(id+"F0.wireOp",EDGE,"E51"),sQuery(id+"F0.wireOp",EDGE,"E52"),sQuery(id+"F0.wireOp",EDGE,"E53"),sQuery(id+"F0.wireOp",EDGE,"E54"),sQuery(id+"F0.wireOp",EDGE,"E55"),sQuery(id+"F0.wireOp",EDGE,"E56"),sQuery(id+"F0.wireOp",EDGE,"E57"),sQuery(id+"F0.wireOp",EDGE,"E58"),sQuery(id+"F0.wireOp",EDGE,"E59"),sQuery(id+"F0.wireOp",EDGE,"E60"),sQuery(id+"F0.wireOp",EDGE,"E61"),sQuery(id+"F0.wireOp",EDGE,"E62"),sQuery(id+"F0.wireOp",EDGE,"E63"),sQuery(id+"F0.wireOp",EDGE,"E64"),sQuery(id+"F0.wireOp",EDGE,"E65"),sQuery(id+"F0.wireOp",EDGE,"E66"),sQuery(id+"F0.wireOp",EDGE,"E67"),sQuery(id+"F0.wireOp",EDGE,"E68"),sQuery(id+"F0.wireOp",EDGE,"E69"),sQuery(id+"F0.wireOp",EDGE,"E70"),sQuery(id+"F0.wireOp",EDGE,"E71"),sQuery(id+"F0.wireOp",EDGE,"E72"),sQuery(id+"F0.wireOp",EDGE,"E73"),sQuery(id+"F0.wireOp",EDGE,"E74"),sQuery(id+"F0.wireOp",EDGE,"E75"),sQuery(id+"F0.wireOp",EDGE,"E76"),sQuery(id+"F0.wireOp",EDGE,"E77"),sQuery(id+"F0.wireOp",EDGE,"E78"),sQuery(id+"F0.wireOp",EDGE,"E79"),sQuery(id+"F0.wireOp",EDGE,"E80"),sQuery(id+"F0.wireOp",EDGE,"E81"),sQuery(id+"F0.wireOp",EDGE,"E82"),sQuery(id+"F0.wireOp",EDGE,"E83"),sQuery(id+"F0.wireOp",EDGE,"E84"),sQuery(id+"F0.wireOp",EDGE,"E85"),sQuery(id+"F0.wireOp",EDGE,"E86"),sQuery(id+"F0.wireOp",EDGE,"E87"),sQuery(id+"F0.wireOp",EDGE,"E88"),sQuery(id+"F0.wireOp",EDGE,"E89"),sQuery(id+"F0.wireOp",EDGE,"E90"),sQuery(id+"F0.wireOp",EDGE,"E91"),sQuery(id+"F0.wireOp",EDGE,"E92"),sQuery(id+"F0.wireOp",EDGE,"E93"),sQuery(id+"F0.wireOp",EDGE,"E94"),sQuery(id+"F0.wireOp",EDGE,"E95"),sQuery(id+"F0.wireOp",EDGE,"E96"),sQuery(id+"F0.wireOp",EDGE,"E97"),sQuery(id+"F0.wireOp",EDGE,"E98"),sQuery(id+"F0.wireOp",EDGE,"E99"),sQuery(id+"F0.wireOp",EDGE,"E100"),sQuery(id+"F0.wireOp",EDGE,"E101"),sQuery(id+"F0.wireOp",EDGE,"E102"),sQuery(id+"F0.wireOp",EDGE,"E103"),sQuery(id+"F0.wireOp",EDGE,"E104")])]}),"instanceName":"26"});
            var Q6;
            Q6=makeQuery(id+"F2.opPattern","COPY",BODY,{"derivedFrom":makeQuery(id+"F1.opExtrude","SWEPT_BODY",BODY,{"disambiguationData":[OSD([sQuery(id+"F0.wireOp",EDGE,"E1"),sQuery(id+"F0.wireOp",EDGE,"E2"),sQuery(id+"F0.wireOp",EDGE,"E3"),sQuery(id+"F0.wireOp",EDGE,"E4"),sQuery(id+"F0.wireOp",EDGE,"E5"),sQuery(id+"F0.wireOp",EDGE,"E6"),sQuery(id+"F0.wireOp",EDGE,"E7"),sQuery(id+"F0.wireOp",EDGE,"E8"),sQuery(id+"F0.wireOp",EDGE,"E9"),sQuery(id+"F0.wireOp",EDGE,"E10"),sQuery(id+"F0.wireOp",EDGE,"E11"),sQuery(id+"F0.wireOp",EDGE,"E12"),sQuery(id+"F0.wireOp",EDGE,"E13"),sQuery(id+"F0.wireOp",EDGE,"E14"),sQuery(id+"F0.wireOp",EDGE,"E15"),sQuery(id+"F0.wireOp",EDGE,"E16"),sQuery(id+"F0.wireOp",EDGE,"E17"),sQuery(id+"F0.wireOp",EDGE,"E18"),sQuery(id+"F0.wireOp",EDGE,"E19"),sQuery(id+"F0.wireOp",EDGE,"E20"),sQuery(id+"F0.wireOp",EDGE,"E21"),sQuery(id+"F0.wireOp",EDGE,"E22"),sQuery(id+"F0.wireOp",EDGE,"E23"),sQuery(id+"F0.wireOp",EDGE,"E24"),sQuery(id+"F0.wireOp",EDGE,"E25"),sQuery(id+"F0.wireOp",EDGE,"E26"),sQuery(id+"F0.wireOp",EDGE,"E27"),sQuery(id+"F0.wireOp",EDGE,"E28"),sQuery(id+"F0.wireOp",EDGE,"E29"),sQuery(id+"F0.wireOp",EDGE,"E30"),sQuery(id+"F0.wireOp",EDGE,"E31"),sQuery(id+"F0.wireOp",EDGE,"E32"),sQuery(id+"F0.wireOp",EDGE,"E33"),sQuery(id+"F0.wireOp",EDGE,"E34"),sQuery(id+"F0.wireOp",EDGE,"E35"),sQuery(id+"F0.wireOp",EDGE,"E36"),sQuery(id+"F0.wireOp",EDGE,"E37"),sQuery(id+"F0.wireOp",EDGE,"E38"),sQuery(id+"F0.wireOp",EDGE,"E39"),sQuery(id+"F0.wireOp",EDGE,"E40"),sQuery(id+"F0.wireOp",EDGE,"E41"),sQuery(id+"F0.wireOp",EDGE,"E42"),sQuery(id+"F0.wireOp",EDGE,"E43"),sQuery(id+"F0.wireOp",EDGE,"E44"),sQuery(id+"F0.wireOp",EDGE,"E45"),sQuery(id+"F0.wireOp",EDGE,"E46"),sQuery(id+"F0.wireOp",EDGE,"E47"),sQuery(id+"F0.wireOp",EDGE,"E48"),sQuery(id+"F0.wireOp",EDGE,"E49"),sQuery(id+"F0.wireOp",EDGE,"E50"),sQuery(id+"F0.wireOp",EDGE,"E51"),sQuery(id+"F0.wireOp",EDGE,"E52"),sQuery(id+"F0.wireOp",EDGE,"E53"),sQuery(id+"F0.wireOp",EDGE,"E54"),sQuery(id+"F0.wireOp",EDGE,"E55"),sQuery(id+"F0.wireOp",EDGE,"E56"),sQuery(id+"F0.wireOp",EDGE,"E57"),sQuery(id+"F0.wireOp",EDGE,"E58"),sQuery(id+"F0.wireOp",EDGE,"E59"),sQuery(id+"F0.wireOp",EDGE,"E60"),sQuery(id+"F0.wireOp",EDGE,"E61"),sQuery(id+"F0.wireOp",EDGE,"E62"),sQuery(id+"F0.wireOp",EDGE,"E63"),sQuery(id+"F0.wireOp",EDGE,"E64"),sQuery(id+"F0.wireOp",EDGE,"E65"),sQuery(id+"F0.wireOp",EDGE,"E66"),sQuery(id+"F0.wireOp",EDGE,"E67"),sQuery(id+"F0.wireOp",EDGE,"E68"),sQuery(id+"F0.wireOp",EDGE,"E69"),sQuery(id+"F0.wireOp",EDGE,"E70"),sQuery(id+"F0.wireOp",EDGE,"E71"),sQuery(id+"F0.wireOp",EDGE,"E72"),sQuery(id+"F0.wireOp",EDGE,"E73"),sQuery(id+"F0.wireOp",EDGE,"E74"),sQuery(id+"F0.wireOp",EDGE,"E75"),sQuery(id+"F0.wireOp",EDGE,"E76"),sQuery(id+"F0.wireOp",EDGE,"E77"),sQuery(id+"F0.wireOp",EDGE,"E78"),sQuery(id+"F0.wireOp",EDGE,"E79"),sQuery(id+"F0.wireOp",EDGE,"E80"),sQuery(id+"F0.wireOp",EDGE,"E81"),sQuery(id+"F0.wireOp",EDGE,"E82"),sQuery(id+"F0.wireOp",EDGE,"E83"),sQuery(id+"F0.wireOp",EDGE,"E84"),sQuery(id+"F0.wireOp",EDGE,"E85"),sQuery(id+"F0.wireOp",EDGE,"E86"),sQuery(id+"F0.wireOp",EDGE,"E87"),sQuery(id+"F0.wireOp",EDGE,"E88"),sQuery(id+"F0.wireOp",EDGE,"E89"),sQuery(id+"F0.wireOp",EDGE,"E90"),sQuery(id+"F0.wireOp",EDGE,"E91"),sQuery(id+"F0.wireOp",EDGE,"E92"),sQuery(id+"F0.wireOp",EDGE,"E93"),sQuery(id+"F0.wireOp",EDGE,"E94"),sQuery(id+"F0.wireOp",EDGE,"E95"),sQuery(id+"F0.wireOp",EDGE,"E96"),sQuery(id+"F0.wireOp",EDGE,"E97"),sQuery(id+"F0.wireOp",EDGE,"E98"),sQuery(id+"F0.wireOp",EDGE,"E99"),sQuery(id+"F0.wireOp",EDGE,"E100"),sQuery(id+"F0.wireOp",EDGE,"E101"),sQuery(id+"F0.wireOp",EDGE,"E102"),sQuery(id+"F0.wireOp",EDGE,"E103"),sQuery(id+"F0.wireOp",EDGE,"E104")])]}),"instanceName":"27"});
            var Q7;
            Q7=makeQuery(id+"F2.opPattern","COPY",BODY,{"derivedFrom":makeQuery(id+"F1.opExtrude","SWEPT_BODY",BODY,{"disambiguationData":[OSD([sQuery(id+"F0.wireOp",EDGE,"E1"),sQuery(id+"F0.wireOp",EDGE,"E2"),sQuery(id+"F0.wireOp",EDGE,"E3"),sQuery(id+"F0.wireOp",EDGE,"E4"),sQuery(id+"F0.wireOp",EDGE,"E5"),sQuery(id+"F0.wireOp",EDGE,"E6"),sQuery(id+"F0.wireOp",EDGE,"E7"),sQuery(id+"F0.wireOp",EDGE,"E8"),sQuery(id+"F0.wireOp",EDGE,"E9"),sQuery(id+"F0.wireOp",EDGE,"E10"),sQuery(id+"F0.wireOp",EDGE,"E11"),sQuery(id+"F0.wireOp",EDGE,"E12"),sQuery(id+"F0.wireOp",EDGE,"E13"),sQuery(id+"F0.wireOp",EDGE,"E14"),sQuery(id+"F0.wireOp",EDGE,"E15"),sQuery(id+"F0.wireOp",EDGE,"E16"),sQuery(id+"F0.wireOp",EDGE,"E17"),sQuery(id+"F0.wireOp",EDGE,"E18"),sQuery(id+"F0.wireOp",EDGE,"E19"),sQuery(id+"F0.wireOp",EDGE,"E20"),sQuery(id+"F0.wireOp",EDGE,"E21"),sQuery(id+"F0.wireOp",EDGE,"E22"),sQuery(id+"F0.wireOp",EDGE,"E23"),sQuery(id+"F0.wireOp",EDGE,"E24"),sQuery(id+"F0.wireOp",EDGE,"E25"),sQuery(id+"F0.wireOp",EDGE,"E26"),sQuery(id+"F0.wireOp",EDGE,"E27"),sQuery(id+"F0.wireOp",EDGE,"E28"),sQuery(id+"F0.wireOp",EDGE,"E29"),sQuery(id+"F0.wireOp",EDGE,"E30"),sQuery(id+"F0.wireOp",EDGE,"E31"),sQuery(id+"F0.wireOp",EDGE,"E32"),sQuery(id+"F0.wireOp",EDGE,"E33"),sQuery(id+"F0.wireOp",EDGE,"E34"),sQuery(id+"F0.wireOp",EDGE,"E35"),sQuery(id+"F0.wireOp",EDGE,"E36"),sQuery(id+"F0.wireOp",EDGE,"E37"),sQuery(id+"F0.wireOp",EDGE,"E38"),sQuery(id+"F0.wireOp",EDGE,"E39"),sQuery(id+"F0.wireOp",EDGE,"E40"),sQuery(id+"F0.wireOp",EDGE,"E41"),sQuery(id+"F0.wireOp",EDGE,"E42"),sQuery(id+"F0.wireOp",EDGE,"E43"),sQuery(id+"F0.wireOp",EDGE,"E44"),sQuery(id+"F0.wireOp",EDGE,"E45"),sQuery(id+"F0.wireOp",EDGE,"E46"),sQuery(id+"F0.wireOp",EDGE,"E47"),sQuery(id+"F0.wireOp",EDGE,"E48"),sQuery(id+"F0.wireOp",EDGE,"E49"),sQuery(id+"F0.wireOp",EDGE,"E50"),sQuery(id+"F0.wireOp",EDGE,"E51"),sQuery(id+"F0.wireOp",EDGE,"E52"),sQuery(id+"F0.wireOp",EDGE,"E53"),sQuery(id+"F0.wireOp",EDGE,"E54"),sQuery(id+"F0.wireOp",EDGE,"E55"),sQuery(id+"F0.wireOp",EDGE,"E56"),sQuery(id+"F0.wireOp",EDGE,"E57"),sQuery(id+"F0.wireOp",EDGE,"E58"),sQuery(id+"F0.wireOp",EDGE,"E59"),sQuery(id+"F0.wireOp",EDGE,"E60"),sQuery(id+"F0.wireOp",EDGE,"E61"),sQuery(id+"F0.wireOp",EDGE,"E62"),sQuery(id+"F0.wireOp",EDGE,"E63"),sQuery(id+"F0.wireOp",EDGE,"E64"),sQuery(id+"F0.wireOp",EDGE,"E65"),sQuery(id+"F0.wireOp",EDGE,"E66"),sQuery(id+"F0.wireOp",EDGE,"E67"),sQuery(id+"F0.wireOp",EDGE,"E68"),sQuery(id+"F0.wireOp",EDGE,"E69"),sQuery(id+"F0.wireOp",EDGE,"E70"),sQuery(id+"F0.wireOp",EDGE,"E71"),sQuery(id+"F0.wireOp",EDGE,"E72"),sQuery(id+"F0.wireOp",EDGE,"E73"),sQuery(id+"F0.wireOp",EDGE,"E74"),sQuery(id+"F0.wireOp",EDGE,"E75"),sQuery(id+"F0.wireOp",EDGE,"E76"),sQuery(id+"F0.wireOp",EDGE,"E77"),sQuery(id+"F0.wireOp",EDGE,"E78"),sQuery(id+"F0.wireOp",EDGE,"E79"),sQuery(id+"F0.wireOp",EDGE,"E80"),sQuery(id+"F0.wireOp",EDGE,"E81"),sQuery(id+"F0.wireOp",EDGE,"E82"),sQuery(id+"F0.wireOp",EDGE,"E83"),sQuery(id+"F0.wireOp",EDGE,"E84"),sQuery(id+"F0.wireOp",EDGE,"E85"),sQuery(id+"F0.wireOp",EDGE,"E86"),sQuery(id+"F0.wireOp",EDGE,"E87"),sQuery(id+"F0.wireOp",EDGE,"E88"),sQuery(id+"F0.wireOp",EDGE,"E89"),sQuery(id+"F0.wireOp",EDGE,"E90"),sQuery(id+"F0.wireOp",EDGE,"E91"),sQuery(id+"F0.wireOp",EDGE,"E92"),sQuery(id+"F0.wireOp",EDGE,"E93"),sQuery(id+"F0.wireOp",EDGE,"E94"),sQuery(id+"F0.wireOp",EDGE,"E95"),sQuery(id+"F0.wireOp",EDGE,"E96"),sQuery(id+"F0.wireOp",EDGE,"E97"),sQuery(id+"F0.wireOp",EDGE,"E98"),sQuery(id+"F0.wireOp",EDGE,"E99"),sQuery(id+"F0.wireOp",EDGE,"E100"),sQuery(id+"F0.wireOp",EDGE,"E101"),sQuery(id+"F0.wireOp",EDGE,"E102"),sQuery(id+"F0.wireOp",EDGE,"E103"),sQuery(id+"F0.wireOp",EDGE,"E104")])]}),"instanceName":"28"});
            var Q8;
            Q8=makeQuery(id+"F2.opPattern","COPY",BODY,{"derivedFrom":makeQuery(id+"F1.opExtrude","SWEPT_BODY",BODY,{"disambiguationData":[OSD([sQuery(id+"F0.wireOp",EDGE,"E1"),sQuery(id+"F0.wireOp",EDGE,"E2"),sQuery(id+"F0.wireOp",EDGE,"E3"),sQuery(id+"F0.wireOp",EDGE,"E4"),sQuery(id+"F0.wireOp",EDGE,"E5"),sQuery(id+"F0.wireOp",EDGE,"E6"),sQuery(id+"F0.wireOp",EDGE,"E7"),sQuery(id+"F0.wireOp",EDGE,"E8"),sQuery(id+"F0.wireOp",EDGE,"E9"),sQuery(id+"F0.wireOp",EDGE,"E10"),sQuery(id+"F0.wireOp",EDGE,"E11"),sQuery(id+"F0.wireOp",EDGE,"E12"),sQuery(id+"F0.wireOp",EDGE,"E13"),sQuery(id+"F0.wireOp",EDGE,"E14"),sQuery(id+"F0.wireOp",EDGE,"E15"),sQuery(id+"F0.wireOp",EDGE,"E16"),sQuery(id+"F0.wireOp",EDGE,"E17"),sQuery(id+"F0.wireOp",EDGE,"E18"),sQuery(id+"F0.wireOp",EDGE,"E19"),sQuery(id+"F0.wireOp",EDGE,"E20"),sQuery(id+"F0.wireOp",EDGE,"E21"),sQuery(id+"F0.wireOp",EDGE,"E22"),sQuery(id+"F0.wireOp",EDGE,"E23"),sQuery(id+"F0.wireOp",EDGE,"E24"),sQuery(id+"F0.wireOp",EDGE,"E25"),sQuery(id+"F0.wireOp",EDGE,"E26"),sQuery(id+"F0.wireOp",EDGE,"E27"),sQuery(id+"F0.wireOp",EDGE,"E28"),sQuery(id+"F0.wireOp",EDGE,"E29"),sQuery(id+"F0.wireOp",EDGE,"E30"),sQuery(id+"F0.wireOp",EDGE,"E31"),sQuery(id+"F0.wireOp",EDGE,"E32"),sQuery(id+"F0.wireOp",EDGE,"E33"),sQuery(id+"F0.wireOp",EDGE,"E34"),sQuery(id+"F0.wireOp",EDGE,"E35"),sQuery(id+"F0.wireOp",EDGE,"E36"),sQuery(id+"F0.wireOp",EDGE,"E37"),sQuery(id+"F0.wireOp",EDGE,"E38"),sQuery(id+"F0.wireOp",EDGE,"E39"),sQuery(id+"F0.wireOp",EDGE,"E40"),sQuery(id+"F0.wireOp",EDGE,"E41"),sQuery(id+"F0.wireOp",EDGE,"E42"),sQuery(id+"F0.wireOp",EDGE,"E43"),sQuery(id+"F0.wireOp",EDGE,"E44"),sQuery(id+"F0.wireOp",EDGE,"E45"),sQuery(id+"F0.wireOp",EDGE,"E46"),sQuery(id+"F0.wireOp",EDGE,"E47"),sQuery(id+"F0.wireOp",EDGE,"E48"),sQuery(id+"F0.wireOp",EDGE,"E49"),sQuery(id+"F0.wireOp",EDGE,"E50"),sQuery(id+"F0.wireOp",EDGE,"E51"),sQuery(id+"F0.wireOp",EDGE,"E52"),sQuery(id+"F0.wireOp",EDGE,"E53"),sQuery(id+"F0.wireOp",EDGE,"E54"),sQuery(id+"F0.wireOp",EDGE,"E55"),sQuery(id+"F0.wireOp",EDGE,"E56"),sQuery(id+"F0.wireOp",EDGE,"E57"),sQuery(id+"F0.wireOp",EDGE,"E58"),sQuery(id+"F0.wireOp",EDGE,"E59"),sQuery(id+"F0.wireOp",EDGE,"E60"),sQuery(id+"F0.wireOp",EDGE,"E61"),sQuery(id+"F0.wireOp",EDGE,"E62"),sQuery(id+"F0.wireOp",EDGE,"E63"),sQuery(id+"F0.wireOp",EDGE,"E64"),sQuery(id+"F0.wireOp",EDGE,"E65"),sQuery(id+"F0.wireOp",EDGE,"E66"),sQuery(id+"F0.wireOp",EDGE,"E67"),sQuery(id+"F0.wireOp",EDGE,"E68"),sQuery(id+"F0.wireOp",EDGE,"E69"),sQuery(id+"F0.wireOp",EDGE,"E70"),sQuery(id+"F0.wireOp",EDGE,"E71"),sQuery(id+"F0.wireOp",EDGE,"E72"),sQuery(id+"F0.wireOp",EDGE,"E73"),sQuery(id+"F0.wireOp",EDGE,"E74"),sQuery(id+"F0.wireOp",EDGE,"E75"),sQuery(id+"F0.wireOp",EDGE,"E76"),sQuery(id+"F0.wireOp",EDGE,"E77"),sQuery(id+"F0.wireOp",EDGE,"E78"),sQuery(id+"F0.wireOp",EDGE,"E79"),sQuery(id+"F0.wireOp",EDGE,"E80"),sQuery(id+"F0.wireOp",EDGE,"E81"),sQuery(id+"F0.wireOp",EDGE,"E82"),sQuery(id+"F0.wireOp",EDGE,"E83"),sQuery(id+"F0.wireOp",EDGE,"E84"),sQuery(id+"F0.wireOp",EDGE,"E85"),sQuery(id+"F0.wireOp",EDGE,"E86"),sQuery(id+"F0.wireOp",EDGE,"E87"),sQuery(id+"F0.wireOp",EDGE,"E88"),sQuery(id+"F0.wireOp",EDGE,"E89"),sQuery(id+"F0.wireOp",EDGE,"E90"),sQuery(id+"F0.wireOp",EDGE,"E91"),sQuery(id+"F0.wireOp",EDGE,"E92"),sQuery(id+"F0.wireOp",EDGE,"E93"),sQuery(id+"F0.wireOp",EDGE,"E94"),sQuery(id+"F0.wireOp",EDGE,"E95"),sQuery(id+"F0.wireOp",EDGE,"E96"),sQuery(id+"F0.wireOp",EDGE,"E97"),sQuery(id+"F0.wireOp",EDGE,"E98"),sQuery(id+"F0.wireOp",EDGE,"E99"),sQuery(id+"F0.wireOp",EDGE,"E100"),sQuery(id+"F0.wireOp",EDGE,"E101"),sQuery(id+"F0.wireOp",EDGE,"E102"),sQuery(id+"F0.wireOp",EDGE,"E103"),sQuery(id+"F0.wireOp",EDGE,"E104")])]}),"instanceName":"29"});
            var Q9;
            Q9=makeQuery(id+"F2.opPattern","COPY",BODY,{"derivedFrom":makeQuery(id+"F1.opExtrude","SWEPT_BODY",BODY,{"disambiguationData":[OSD([sQuery(id+"F0.wireOp",EDGE,"E1"),sQuery(id+"F0.wireOp",EDGE,"E2"),sQuery(id+"F0.wireOp",EDGE,"E3"),sQuery(id+"F0.wireOp",EDGE,"E4"),sQuery(id+"F0.wireOp",EDGE,"E5"),sQuery(id+"F0.wireOp",EDGE,"E6"),sQuery(id+"F0.wireOp",EDGE,"E7"),sQuery(id+"F0.wireOp",EDGE,"E8"),sQuery(id+"F0.wireOp",EDGE,"E9"),sQuery(id+"F0.wireOp",EDGE,"E10"),sQuery(id+"F0.wireOp",EDGE,"E11"),sQuery(id+"F0.wireOp",EDGE,"E12"),sQuery(id+"F0.wireOp",EDGE,"E13"),sQuery(id+"F0.wireOp",EDGE,"E14"),sQuery(id+"F0.wireOp",EDGE,"E15"),sQuery(id+"F0.wireOp",EDGE,"E16"),sQuery(id+"F0.wireOp",EDGE,"E17"),sQuery(id+"F0.wireOp",EDGE,"E18"),sQuery(id+"F0.wireOp",EDGE,"E19"),sQuery(id+"F0.wireOp",EDGE,"E20"),sQuery(id+"F0.wireOp",EDGE,"E21"),sQuery(id+"F0.wireOp",EDGE,"E22"),sQuery(id+"F0.wireOp",EDGE,"E23"),sQuery(id+"F0.wireOp",EDGE,"E24"),sQuery(id+"F0.wireOp",EDGE,"E25"),sQuery(id+"F0.wireOp",EDGE,"E26"),sQuery(id+"F0.wireOp",EDGE,"E27"),sQuery(id+"F0.wireOp",EDGE,"E28"),sQuery(id+"F0.wireOp",EDGE,"E29"),sQuery(id+"F0.wireOp",EDGE,"E30"),sQuery(id+"F0.wireOp",EDGE,"E31"),sQuery(id+"F0.wireOp",EDGE,"E32"),sQuery(id+"F0.wireOp",EDGE,"E33"),sQuery(id+"F0.wireOp",EDGE,"E34"),sQuery(id+"F0.wireOp",EDGE,"E35"),sQuery(id+"F0.wireOp",EDGE,"E36"),sQuery(id+"F0.wireOp",EDGE,"E37"),sQuery(id+"F0.wireOp",EDGE,"E38"),sQuery(id+"F0.wireOp",EDGE,"E39"),sQuery(id+"F0.wireOp",EDGE,"E40"),sQuery(id+"F0.wireOp",EDGE,"E41"),sQuery(id+"F0.wireOp",EDGE,"E42"),sQuery(id+"F0.wireOp",EDGE,"E43"),sQuery(id+"F0.wireOp",EDGE,"E44"),sQuery(id+"F0.wireOp",EDGE,"E45"),sQuery(id+"F0.wireOp",EDGE,"E46"),sQuery(id+"F0.wireOp",EDGE,"E47"),sQuery(id+"F0.wireOp",EDGE,"E48"),sQuery(id+"F0.wireOp",EDGE,"E49"),sQuery(id+"F0.wireOp",EDGE,"E50"),sQuery(id+"F0.wireOp",EDGE,"E51"),sQuery(id+"F0.wireOp",EDGE,"E52"),sQuery(id+"F0.wireOp",EDGE,"E53"),sQuery(id+"F0.wireOp",EDGE,"E54"),sQuery(id+"F0.wireOp",EDGE,"E55"),sQuery(id+"F0.wireOp",EDGE,"E56"),sQuery(id+"F0.wireOp",EDGE,"E57"),sQuery(id+"F0.wireOp",EDGE,"E58"),sQuery(id+"F0.wireOp",EDGE,"E59"),sQuery(id+"F0.wireOp",EDGE,"E60"),sQuery(id+"F0.wireOp",EDGE,"E61"),sQuery(id+"F0.wireOp",EDGE,"E62"),sQuery(id+"F0.wireOp",EDGE,"E63"),sQuery(id+"F0.wireOp",EDGE,"E64"),sQuery(id+"F0.wireOp",EDGE,"E65"),sQuery(id+"F0.wireOp",EDGE,"E66"),sQuery(id+"F0.wireOp",EDGE,"E67"),sQuery(id+"F0.wireOp",EDGE,"E68"),sQuery(id+"F0.wireOp",EDGE,"E69"),sQuery(id+"F0.wireOp",EDGE,"E70"),sQuery(id+"F0.wireOp",EDGE,"E71"),sQuery(id+"F0.wireOp",EDGE,"E72"),sQuery(id+"F0.wireOp",EDGE,"E73"),sQuery(id+"F0.wireOp",EDGE,"E74"),sQuery(id+"F0.wireOp",EDGE,"E75"),sQuery(id+"F0.wireOp",EDGE,"E76"),sQuery(id+"F0.wireOp",EDGE,"E77"),sQuery(id+"F0.wireOp",EDGE,"E78"),sQuery(id+"F0.wireOp",EDGE,"E79"),sQuery(id+"F0.wireOp",EDGE,"E80"),sQuery(id+"F0.wireOp",EDGE,"E81"),sQuery(id+"F0.wireOp",EDGE,"E82"),sQuery(id+"F0.wireOp",EDGE,"E83"),sQuery(id+"F0.wireOp",EDGE,"E84"),sQuery(id+"F0.wireOp",EDGE,"E85"),sQuery(id+"F0.wireOp",EDGE,"E86"),sQuery(id+"F0.wireOp",EDGE,"E87"),sQuery(id+"F0.wireOp",EDGE,"E88"),sQuery(id+"F0.wireOp",EDGE,"E89"),sQuery(id+"F0.wireOp",EDGE,"E90"),sQuery(id+"F0.wireOp",EDGE,"E91"),sQuery(id+"F0.wireOp",EDGE,"E92"),sQuery(id+"F0.wireOp",EDGE,"E93"),sQuery(id+"F0.wireOp",EDGE,"E94"),sQuery(id+"F0.wireOp",EDGE,"E95"),sQuery(id+"F0.wireOp",EDGE,"E96"),sQuery(id+"F0.wireOp",EDGE,"E97"),sQuery(id+"F0.wireOp",EDGE,"E98"),sQuery(id+"F0.wireOp",EDGE,"E99"),sQuery(id+"F0.wireOp",EDGE,"E100"),sQuery(id+"F0.wireOp",EDGE,"E101"),sQuery(id+"F0.wireOp",EDGE,"E102"),sQuery(id+"F0.wireOp",EDGE,"E103"),sQuery(id+"F0.wireOp",EDGE,"E104")])]}),"instanceName":"30"});
            var Q10;
            Q10=makeQuery(id+"F2.opPattern","COPY",BODY,{"derivedFrom":makeQuery(id+"F1.opExtrude","SWEPT_BODY",BODY,{"disambiguationData":[OSD([sQuery(id+"F0.wireOp",EDGE,"E1"),sQuery(id+"F0.wireOp",EDGE,"E2"),sQuery(id+"F0.wireOp",EDGE,"E3"),sQuery(id+"F0.wireOp",EDGE,"E4"),sQuery(id+"F0.wireOp",EDGE,"E5"),sQuery(id+"F0.wireOp",EDGE,"E6"),sQuery(id+"F0.wireOp",EDGE,"E7"),sQuery(id+"F0.wireOp",EDGE,"E8"),sQuery(id+"F0.wireOp",EDGE,"E9"),sQuery(id+"F0.wireOp",EDGE,"E10"),sQuery(id+"F0.wireOp",EDGE,"E11"),sQuery(id+"F0.wireOp",EDGE,"E12"),sQuery(id+"F0.wireOp",EDGE,"E13"),sQuery(id+"F0.wireOp",EDGE,"E14"),sQuery(id+"F0.wireOp",EDGE,"E15"),sQuery(id+"F0.wireOp",EDGE,"E16"),sQuery(id+"F0.wireOp",EDGE,"E17"),sQuery(id+"F0.wireOp",EDGE,"E18"),sQuery(id+"F0.wireOp",EDGE,"E19"),sQuery(id+"F0.wireOp",EDGE,"E20"),sQuery(id+"F0.wireOp",EDGE,"E21"),sQuery(id+"F0.wireOp",EDGE,"E22"),sQuery(id+"F0.wireOp",EDGE,"E23"),sQuery(id+"F0.wireOp",EDGE,"E24"),sQuery(id+"F0.wireOp",EDGE,"E25"),sQuery(id+"F0.wireOp",EDGE,"E26"),sQuery(id+"F0.wireOp",EDGE,"E27"),sQuery(id+"F0.wireOp",EDGE,"E28"),sQuery(id+"F0.wireOp",EDGE,"E29"),sQuery(id+"F0.wireOp",EDGE,"E30"),sQuery(id+"F0.wireOp",EDGE,"E31"),sQuery(id+"F0.wireOp",EDGE,"E32"),sQuery(id+"F0.wireOp",EDGE,"E33"),sQuery(id+"F0.wireOp",EDGE,"E34"),sQuery(id+"F0.wireOp",EDGE,"E35"),sQuery(id+"F0.wireOp",EDGE,"E36"),sQuery(id+"F0.wireOp",EDGE,"E37"),sQuery(id+"F0.wireOp",EDGE,"E38"),sQuery(id+"F0.wireOp",EDGE,"E39"),sQuery(id+"F0.wireOp",EDGE,"E40"),sQuery(id+"F0.wireOp",EDGE,"E41"),sQuery(id+"F0.wireOp",EDGE,"E42"),sQuery(id+"F0.wireOp",EDGE,"E43"),sQuery(id+"F0.wireOp",EDGE,"E44"),sQuery(id+"F0.wireOp",EDGE,"E45"),sQuery(id+"F0.wireOp",EDGE,"E46"),sQuery(id+"F0.wireOp",EDGE,"E47"),sQuery(id+"F0.wireOp",EDGE,"E48"),sQuery(id+"F0.wireOp",EDGE,"E49"),sQuery(id+"F0.wireOp",EDGE,"E50"),sQuery(id+"F0.wireOp",EDGE,"E51"),sQuery(id+"F0.wireOp",EDGE,"E52"),sQuery(id+"F0.wireOp",EDGE,"E53"),sQuery(id+"F0.wireOp",EDGE,"E54"),sQuery(id+"F0.wireOp",EDGE,"E55"),sQuery(id+"F0.wireOp",EDGE,"E56"),sQuery(id+"F0.wireOp",EDGE,"E57"),sQuery(id+"F0.wireOp",EDGE,"E58"),sQuery(id+"F0.wireOp",EDGE,"E59"),sQuery(id+"F0.wireOp",EDGE,"E60"),sQuery(id+"F0.wireOp",EDGE,"E61"),sQuery(id+"F0.wireOp",EDGE,"E62"),sQuery(id+"F0.wireOp",EDGE,"E63"),sQuery(id+"F0.wireOp",EDGE,"E64"),sQuery(id+"F0.wireOp",EDGE,"E65"),sQuery(id+"F0.wireOp",EDGE,"E66"),sQuery(id+"F0.wireOp",EDGE,"E67"),sQuery(id+"F0.wireOp",EDGE,"E68"),sQuery(id+"F0.wireOp",EDGE,"E69"),sQuery(id+"F0.wireOp",EDGE,"E70"),sQuery(id+"F0.wireOp",EDGE,"E71"),sQuery(id+"F0.wireOp",EDGE,"E72"),sQuery(id+"F0.wireOp",EDGE,"E73"),sQuery(id+"F0.wireOp",EDGE,"E74"),sQuery(id+"F0.wireOp",EDGE,"E75"),sQuery(id+"F0.wireOp",EDGE,"E76"),sQuery(id+"F0.wireOp",EDGE,"E77"),sQuery(id+"F0.wireOp",EDGE,"E78"),sQuery(id+"F0.wireOp",EDGE,"E79"),sQuery(id+"F0.wireOp",EDGE,"E80"),sQuery(id+"F0.wireOp",EDGE,"E81"),sQuery(id+"F0.wireOp",EDGE,"E82"),sQuery(id+"F0.wireOp",EDGE,"E83"),sQuery(id+"F0.wireOp",EDGE,"E84"),sQuery(id+"F0.wireOp",EDGE,"E85"),sQuery(id+"F0.wireOp",EDGE,"E86"),sQuery(id+"F0.wireOp",EDGE,"E87"),sQuery(id+"F0.wireOp",EDGE,"E88"),sQuery(id+"F0.wireOp",EDGE,"E89"),sQuery(id+"F0.wireOp",EDGE,"E90"),sQuery(id+"F0.wireOp",EDGE,"E91"),sQuery(id+"F0.wireOp",EDGE,"E92"),sQuery(id+"F0.wireOp",EDGE,"E93"),sQuery(id+"F0.wireOp",EDGE,"E94"),sQuery(id+"F0.wireOp",EDGE,"E95"),sQuery(id+"F0.wireOp",EDGE,"E96"),sQuery(id+"F0.wireOp",EDGE,"E97"),sQuery(id+"F0.wireOp",EDGE,"E98"),sQuery(id+"F0.wireOp",EDGE,"E99"),sQuery(id+"F0.wireOp",EDGE,"E100"),sQuery(id+"F0.wireOp",EDGE,"E101"),sQuery(id+"F0.wireOp",EDGE,"E102"),sQuery(id+"F0.wireOp",EDGE,"E103"),sQuery(id+"F0.wireOp",EDGE,"E104")])]}),"instanceName":"31"});
            var Q11;
            Q11=makeQuery(id+"F2.opPattern","COPY",BODY,{"derivedFrom":makeQuery(id+"F1.opExtrude","SWEPT_BODY",BODY,{"disambiguationData":[OSD([sQuery(id+"F0.wireOp",EDGE,"E1"),sQuery(id+"F0.wireOp",EDGE,"E2"),sQuery(id+"F0.wireOp",EDGE,"E3"),sQuery(id+"F0.wireOp",EDGE,"E4"),sQuery(id+"F0.wireOp",EDGE,"E5"),sQuery(id+"F0.wireOp",EDGE,"E6"),sQuery(id+"F0.wireOp",EDGE,"E7"),sQuery(id+"F0.wireOp",EDGE,"E8"),sQuery(id+"F0.wireOp",EDGE,"E9"),sQuery(id+"F0.wireOp",EDGE,"E10"),sQuery(id+"F0.wireOp",EDGE,"E11"),sQuery(id+"F0.wireOp",EDGE,"E12"),sQuery(id+"F0.wireOp",EDGE,"E13"),sQuery(id+"F0.wireOp",EDGE,"E14"),sQuery(id+"F0.wireOp",EDGE,"E15"),sQuery(id+"F0.wireOp",EDGE,"E16"),sQuery(id+"F0.wireOp",EDGE,"E17"),sQuery(id+"F0.wireOp",EDGE,"E18"),sQuery(id+"F0.wireOp",EDGE,"E19"),sQuery(id+"F0.wireOp",EDGE,"E20"),sQuery(id+"F0.wireOp",EDGE,"E21"),sQuery(id+"F0.wireOp",EDGE,"E22"),sQuery(id+"F0.wireOp",EDGE,"E23"),sQuery(id+"F0.wireOp",EDGE,"E24"),sQuery(id+"F0.wireOp",EDGE,"E25"),sQuery(id+"F0.wireOp",EDGE,"E26"),sQuery(id+"F0.wireOp",EDGE,"E27"),sQuery(id+"F0.wireOp",EDGE,"E28"),sQuery(id+"F0.wireOp",EDGE,"E29"),sQuery(id+"F0.wireOp",EDGE,"E30"),sQuery(id+"F0.wireOp",EDGE,"E31"),sQuery(id+"F0.wireOp",EDGE,"E32"),sQuery(id+"F0.wireOp",EDGE,"E33"),sQuery(id+"F0.wireOp",EDGE,"E34"),sQuery(id+"F0.wireOp",EDGE,"E35"),sQuery(id+"F0.wireOp",EDGE,"E36"),sQuery(id+"F0.wireOp",EDGE,"E37"),sQuery(id+"F0.wireOp",EDGE,"E38"),sQuery(id+"F0.wireOp",EDGE,"E39"),sQuery(id+"F0.wireOp",EDGE,"E40"),sQuery(id+"F0.wireOp",EDGE,"E41"),sQuery(id+"F0.wireOp",EDGE,"E42"),sQuery(id+"F0.wireOp",EDGE,"E43"),sQuery(id+"F0.wireOp",EDGE,"E44"),sQuery(id+"F0.wireOp",EDGE,"E45"),sQuery(id+"F0.wireOp",EDGE,"E46"),sQuery(id+"F0.wireOp",EDGE,"E47"),sQuery(id+"F0.wireOp",EDGE,"E48"),sQuery(id+"F0.wireOp",EDGE,"E49"),sQuery(id+"F0.wireOp",EDGE,"E50"),sQuery(id+"F0.wireOp",EDGE,"E51"),sQuery(id+"F0.wireOp",EDGE,"E52"),sQuery(id+"F0.wireOp",EDGE,"E53"),sQuery(id+"F0.wireOp",EDGE,"E54"),sQuery(id+"F0.wireOp",EDGE,"E55"),sQuery(id+"F0.wireOp",EDGE,"E56"),sQuery(id+"F0.wireOp",EDGE,"E57"),sQuery(id+"F0.wireOp",EDGE,"E58"),sQuery(id+"F0.wireOp",EDGE,"E59"),sQuery(id+"F0.wireOp",EDGE,"E60"),sQuery(id+"F0.wireOp",EDGE,"E61"),sQuery(id+"F0.wireOp",EDGE,"E62"),sQuery(id+"F0.wireOp",EDGE,"E63"),sQuery(id+"F0.wireOp",EDGE,"E64"),sQuery(id+"F0.wireOp",EDGE,"E65"),sQuery(id+"F0.wireOp",EDGE,"E66"),sQuery(id+"F0.wireOp",EDGE,"E67"),sQuery(id+"F0.wireOp",EDGE,"E68"),sQuery(id+"F0.wireOp",EDGE,"E69"),sQuery(id+"F0.wireOp",EDGE,"E70"),sQuery(id+"F0.wireOp",EDGE,"E71"),sQuery(id+"F0.wireOp",EDGE,"E72"),sQuery(id+"F0.wireOp",EDGE,"E73"),sQuery(id+"F0.wireOp",EDGE,"E74"),sQuery(id+"F0.wireOp",EDGE,"E75"),sQuery(id+"F0.wireOp",EDGE,"E76"),sQuery(id+"F0.wireOp",EDGE,"E77"),sQuery(id+"F0.wireOp",EDGE,"E78"),sQuery(id+"F0.wireOp",EDGE,"E79"),sQuery(id+"F0.wireOp",EDGE,"E80"),sQuery(id+"F0.wireOp",EDGE,"E81"),sQuery(id+"F0.wireOp",EDGE,"E82"),sQuery(id+"F0.wireOp",EDGE,"E83"),sQuery(id+"F0.wireOp",EDGE,"E84"),sQuery(id+"F0.wireOp",EDGE,"E85"),sQuery(id+"F0.wireOp",EDGE,"E86"),sQuery(id+"F0.wireOp",EDGE,"E87"),sQuery(id+"F0.wireOp",EDGE,"E88"),sQuery(id+"F0.wireOp",EDGE,"E89"),sQuery(id+"F0.wireOp",EDGE,"E90"),sQuery(id+"F0.wireOp",EDGE,"E91"),sQuery(id+"F0.wireOp",EDGE,"E92"),sQuery(id+"F0.wireOp",EDGE,"E93"),sQuery(id+"F0.wireOp",EDGE,"E94"),sQuery(id+"F0.wireOp",EDGE,"E95"),sQuery(id+"F0.wireOp",EDGE,"E96"),sQuery(id+"F0.wireOp",EDGE,"E97"),sQuery(id+"F0.wireOp",EDGE,"E98"),sQuery(id+"F0.wireOp",EDGE,"E99"),sQuery(id+"F0.wireOp",EDGE,"E100"),sQuery(id+"F0.wireOp",EDGE,"E101"),sQuery(id+"F0.wireOp",EDGE,"E102"),sQuery(id+"F0.wireOp",EDGE,"E103"),sQuery(id+"F0.wireOp",EDGE,"E104")])]}),"instanceName":"32"});
            var Q12;
            Q12=makeQuery(id+"F2.opPattern","COPY",BODY,{"derivedFrom":makeQuery(id+"F1.opExtrude","SWEPT_BODY",BODY,{"disambiguationData":[OSD([sQuery(id+"F0.wireOp",EDGE,"E1"),sQuery(id+"F0.wireOp",EDGE,"E2"),sQuery(id+"F0.wireOp",EDGE,"E3"),sQuery(id+"F0.wireOp",EDGE,"E4"),sQuery(id+"F0.wireOp",EDGE,"E5"),sQuery(id+"F0.wireOp",EDGE,"E6"),sQuery(id+"F0.wireOp",EDGE,"E7"),sQuery(id+"F0.wireOp",EDGE,"E8"),sQuery(id+"F0.wireOp",EDGE,"E9"),sQuery(id+"F0.wireOp",EDGE,"E10"),sQuery(id+"F0.wireOp",EDGE,"E11"),sQuery(id+"F0.wireOp",EDGE,"E12"),sQuery(id+"F0.wireOp",EDGE,"E13"),sQuery(id+"F0.wireOp",EDGE,"E14"),sQuery(id+"F0.wireOp",EDGE,"E15"),sQuery(id+"F0.wireOp",EDGE,"E16"),sQuery(id+"F0.wireOp",EDGE,"E17"),sQuery(id+"F0.wireOp",EDGE,"E18"),sQuery(id+"F0.wireOp",EDGE,"E19"),sQuery(id+"F0.wireOp",EDGE,"E20"),sQuery(id+"F0.wireOp",EDGE,"E21"),sQuery(id+"F0.wireOp",EDGE,"E22"),sQuery(id+"F0.wireOp",EDGE,"E23"),sQuery(id+"F0.wireOp",EDGE,"E24"),sQuery(id+"F0.wireOp",EDGE,"E25"),sQuery(id+"F0.wireOp",EDGE,"E26"),sQuery(id+"F0.wireOp",EDGE,"E27"),sQuery(id+"F0.wireOp",EDGE,"E28"),sQuery(id+"F0.wireOp",EDGE,"E29"),sQuery(id+"F0.wireOp",EDGE,"E30"),sQuery(id+"F0.wireOp",EDGE,"E31"),sQuery(id+"F0.wireOp",EDGE,"E32"),sQuery(id+"F0.wireOp",EDGE,"E33"),sQuery(id+"F0.wireOp",EDGE,"E34"),sQuery(id+"F0.wireOp",EDGE,"E35"),sQuery(id+"F0.wireOp",EDGE,"E36"),sQuery(id+"F0.wireOp",EDGE,"E37"),sQuery(id+"F0.wireOp",EDGE,"E38"),sQuery(id+"F0.wireOp",EDGE,"E39"),sQuery(id+"F0.wireOp",EDGE,"E40"),sQuery(id+"F0.wireOp",EDGE,"E41"),sQuery(id+"F0.wireOp",EDGE,"E42"),sQuery(id+"F0.wireOp",EDGE,"E43"),sQuery(id+"F0.wireOp",EDGE,"E44"),sQuery(id+"F0.wireOp",EDGE,"E45"),sQuery(id+"F0.wireOp",EDGE,"E46"),sQuery(id+"F0.wireOp",EDGE,"E47"),sQuery(id+"F0.wireOp",EDGE,"E48"),sQuery(id+"F0.wireOp",EDGE,"E49"),sQuery(id+"F0.wireOp",EDGE,"E50"),sQuery(id+"F0.wireOp",EDGE,"E51"),sQuery(id+"F0.wireOp",EDGE,"E52"),sQuery(id+"F0.wireOp",EDGE,"E53"),sQuery(id+"F0.wireOp",EDGE,"E54"),sQuery(id+"F0.wireOp",EDGE,"E55"),sQuery(id+"F0.wireOp",EDGE,"E56"),sQuery(id+"F0.wireOp",EDGE,"E57"),sQuery(id+"F0.wireOp",EDGE,"E58"),sQuery(id+"F0.wireOp",EDGE,"E59"),sQuery(id+"F0.wireOp",EDGE,"E60"),sQuery(id+"F0.wireOp",EDGE,"E61"),sQuery(id+"F0.wireOp",EDGE,"E62"),sQuery(id+"F0.wireOp",EDGE,"E63"),sQuery(id+"F0.wireOp",EDGE,"E64"),sQuery(id+"F0.wireOp",EDGE,"E65"),sQuery(id+"F0.wireOp",EDGE,"E66"),sQuery(id+"F0.wireOp",EDGE,"E67"),sQuery(id+"F0.wireOp",EDGE,"E68"),sQuery(id+"F0.wireOp",EDGE,"E69"),sQuery(id+"F0.wireOp",EDGE,"E70"),sQuery(id+"F0.wireOp",EDGE,"E71"),sQuery(id+"F0.wireOp",EDGE,"E72"),sQuery(id+"F0.wireOp",EDGE,"E73"),sQuery(id+"F0.wireOp",EDGE,"E74"),sQuery(id+"F0.wireOp",EDGE,"E75"),sQuery(id+"F0.wireOp",EDGE,"E76"),sQuery(id+"F0.wireOp",EDGE,"E77"),sQuery(id+"F0.wireOp",EDGE,"E78"),sQuery(id+"F0.wireOp",EDGE,"E79"),sQuery(id+"F0.wireOp",EDGE,"E80"),sQuery(id+"F0.wireOp",EDGE,"E81"),sQuery(id+"F0.wireOp",EDGE,"E82"),sQuery(id+"F0.wireOp",EDGE,"E83"),sQuery(id+"F0.wireOp",EDGE,"E84"),sQuery(id+"F0.wireOp",EDGE,"E85"),sQuery(id+"F0.wireOp",EDGE,"E86"),sQuery(id+"F0.wireOp",EDGE,"E87"),sQuery(id+"F0.wireOp",EDGE,"E88"),sQuery(id+"F0.wireOp",EDGE,"E89"),sQuery(id+"F0.wireOp",EDGE,"E90"),sQuery(id+"F0.wireOp",EDGE,"E91"),sQuery(id+"F0.wireOp",EDGE,"E92"),sQuery(id+"F0.wireOp",EDGE,"E93"),sQuery(id+"F0.wireOp",EDGE,"E94"),sQuery(id+"F0.wireOp",EDGE,"E95"),sQuery(id+"F0.wireOp",EDGE,"E96"),sQuery(id+"F0.wireOp",EDGE,"E97"),sQuery(id+"F0.wireOp",EDGE,"E98"),sQuery(id+"F0.wireOp",EDGE,"E99"),sQuery(id+"F0.wireOp",EDGE,"E100"),sQuery(id+"F0.wireOp",EDGE,"E101"),sQuery(id+"F0.wireOp",EDGE,"E102"),sQuery(id+"F0.wireOp",EDGE,"E103"),sQuery(id+"F0.wireOp",EDGE,"E104")])]}),"instanceName":"33"});
            var Q13;
            Q13=makeQuery(id+"F2.opPattern","COPY",BODY,{"derivedFrom":makeQuery(id+"F1.opExtrude","SWEPT_BODY",BODY,{"disambiguationData":[OSD([sQuery(id+"F0.wireOp",EDGE,"E1"),sQuery(id+"F0.wireOp",EDGE,"E2"),sQuery(id+"F0.wireOp",EDGE,"E3"),sQuery(id+"F0.wireOp",EDGE,"E4"),sQuery(id+"F0.wireOp",EDGE,"E5"),sQuery(id+"F0.wireOp",EDGE,"E6"),sQuery(id+"F0.wireOp",EDGE,"E7"),sQuery(id+"F0.wireOp",EDGE,"E8"),sQuery(id+"F0.wireOp",EDGE,"E9"),sQuery(id+"F0.wireOp",EDGE,"E10"),sQuery(id+"F0.wireOp",EDGE,"E11"),sQuery(id+"F0.wireOp",EDGE,"E12"),sQuery(id+"F0.wireOp",EDGE,"E13"),sQuery(id+"F0.wireOp",EDGE,"E14"),sQuery(id+"F0.wireOp",EDGE,"E15"),sQuery(id+"F0.wireOp",EDGE,"E16"),sQuery(id+"F0.wireOp",EDGE,"E17"),sQuery(id+"F0.wireOp",EDGE,"E18"),sQuery(id+"F0.wireOp",EDGE,"E19"),sQuery(id+"F0.wireOp",EDGE,"E20"),sQuery(id+"F0.wireOp",EDGE,"E21"),sQuery(id+"F0.wireOp",EDGE,"E22"),sQuery(id+"F0.wireOp",EDGE,"E23"),sQuery(id+"F0.wireOp",EDGE,"E24"),sQuery(id+"F0.wireOp",EDGE,"E25"),sQuery(id+"F0.wireOp",EDGE,"E26"),sQuery(id+"F0.wireOp",EDGE,"E27"),sQuery(id+"F0.wireOp",EDGE,"E28"),sQuery(id+"F0.wireOp",EDGE,"E29"),sQuery(id+"F0.wireOp",EDGE,"E30"),sQuery(id+"F0.wireOp",EDGE,"E31"),sQuery(id+"F0.wireOp",EDGE,"E32"),sQuery(id+"F0.wireOp",EDGE,"E33"),sQuery(id+"F0.wireOp",EDGE,"E34"),sQuery(id+"F0.wireOp",EDGE,"E35"),sQuery(id+"F0.wireOp",EDGE,"E36"),sQuery(id+"F0.wireOp",EDGE,"E37"),sQuery(id+"F0.wireOp",EDGE,"E38"),sQuery(id+"F0.wireOp",EDGE,"E39"),sQuery(id+"F0.wireOp",EDGE,"E40"),sQuery(id+"F0.wireOp",EDGE,"E41"),sQuery(id+"F0.wireOp",EDGE,"E42"),sQuery(id+"F0.wireOp",EDGE,"E43"),sQuery(id+"F0.wireOp",EDGE,"E44"),sQuery(id+"F0.wireOp",EDGE,"E45"),sQuery(id+"F0.wireOp",EDGE,"E46"),sQuery(id+"F0.wireOp",EDGE,"E47"),sQuery(id+"F0.wireOp",EDGE,"E48"),sQuery(id+"F0.wireOp",EDGE,"E49"),sQuery(id+"F0.wireOp",EDGE,"E50"),sQuery(id+"F0.wireOp",EDGE,"E51"),sQuery(id+"F0.wireOp",EDGE,"E52"),sQuery(id+"F0.wireOp",EDGE,"E53"),sQuery(id+"F0.wireOp",EDGE,"E54"),sQuery(id+"F0.wireOp",EDGE,"E55"),sQuery(id+"F0.wireOp",EDGE,"E56"),sQuery(id+"F0.wireOp",EDGE,"E57"),sQuery(id+"F0.wireOp",EDGE,"E58"),sQuery(id+"F0.wireOp",EDGE,"E59"),sQuery(id+"F0.wireOp",EDGE,"E60"),sQuery(id+"F0.wireOp",EDGE,"E61"),sQuery(id+"F0.wireOp",EDGE,"E62"),sQuery(id+"F0.wireOp",EDGE,"E63"),sQuery(id+"F0.wireOp",EDGE,"E64"),sQuery(id+"F0.wireOp",EDGE,"E65"),sQuery(id+"F0.wireOp",EDGE,"E66"),sQuery(id+"F0.wireOp",EDGE,"E67"),sQuery(id+"F0.wireOp",EDGE,"E68"),sQuery(id+"F0.wireOp",EDGE,"E69"),sQuery(id+"F0.wireOp",EDGE,"E70"),sQuery(id+"F0.wireOp",EDGE,"E71"),sQuery(id+"F0.wireOp",EDGE,"E72"),sQuery(id+"F0.wireOp",EDGE,"E73"),sQuery(id+"F0.wireOp",EDGE,"E74"),sQuery(id+"F0.wireOp",EDGE,"E75"),sQuery(id+"F0.wireOp",EDGE,"E76"),sQuery(id+"F0.wireOp",EDGE,"E77"),sQuery(id+"F0.wireOp",EDGE,"E78"),sQuery(id+"F0.wireOp",EDGE,"E79"),sQuery(id+"F0.wireOp",EDGE,"E80"),sQuery(id+"F0.wireOp",EDGE,"E81"),sQuery(id+"F0.wireOp",EDGE,"E82"),sQuery(id+"F0.wireOp",EDGE,"E83"),sQuery(id+"F0.wireOp",EDGE,"E84"),sQuery(id+"F0.wireOp",EDGE,"E85"),sQuery(id+"F0.wireOp",EDGE,"E86"),sQuery(id+"F0.wireOp",EDGE,"E87"),sQuery(id+"F0.wireOp",EDGE,"E88"),sQuery(id+"F0.wireOp",EDGE,"E89"),sQuery(id+"F0.wireOp",EDGE,"E90"),sQuery(id+"F0.wireOp",EDGE,"E91"),sQuery(id+"F0.wireOp",EDGE,"E92"),sQuery(id+"F0.wireOp",EDGE,"E93"),sQuery(id+"F0.wireOp",EDGE,"E94"),sQuery(id+"F0.wireOp",EDGE,"E95"),sQuery(id+"F0.wireOp",EDGE,"E96"),sQuery(id+"F0.wireOp",EDGE,"E97"),sQuery(id+"F0.wireOp",EDGE,"E98"),sQuery(id+"F0.wireOp",EDGE,"E99"),sQuery(id+"F0.wireOp",EDGE,"E100"),sQuery(id+"F0.wireOp",EDGE,"E101"),sQuery(id+"F0.wireOp",EDGE,"E102"),sQuery(id+"F0.wireOp",EDGE,"E103"),sQuery(id+"F0.wireOp",EDGE,"E104")])]}),"instanceName":"34"});
            booleanBodies(context, id + "F4", {"operationType" : BooleanOperationType.UNION, "tools" : qUnion([Q0, Q1, Q2, Q3, Q4, Q5, Q6, Q7, Q8, Q9, Q10, Q11, Q12, Q13])});
        }
        {
            var Q0;
            Q0=makeQuery(id+"F1.opExtrude","SWEPT_BODY",BODY,{"disambiguationData":[OSD([sQuery(id+"F0.wireOp",EDGE,"E105")])]});
            var Q1;
            Q1=makeQuery(id+"F2.opPattern","COPY",BODY,{"derivedFrom":makeQuery(id+"F1.opExtrude","SWEPT_BODY",BODY,{"disambiguationData":[OSD([sQuery(id+"F0.wireOp",EDGE,"E1"),sQuery(id+"F0.wireOp",EDGE,"E2"),sQuery(id+"F0.wireOp",EDGE,"E3"),sQuery(id+"F0.wireOp",EDGE,"E4"),sQuery(id+"F0.wireOp",EDGE,"E5"),sQuery(id+"F0.wireOp",EDGE,"E6"),sQuery(id+"F0.wireOp",EDGE,"E7"),sQuery(id+"F0.wireOp",EDGE,"E8"),sQuery(id+"F0.wireOp",EDGE,"E9"),sQuery(id+"F0.wireOp",EDGE,"E10"),sQuery(id+"F0.wireOp",EDGE,"E11"),sQuery(id+"F0.wireOp",EDGE,"E12"),sQuery(id+"F0.wireOp",EDGE,"E13"),sQuery(id+"F0.wireOp",EDGE,"E14"),sQuery(id+"F0.wireOp",EDGE,"E15"),sQuery(id+"F0.wireOp",EDGE,"E16"),sQuery(id+"F0.wireOp",EDGE,"E17"),sQuery(id+"F0.wireOp",EDGE,"E18"),sQuery(id+"F0.wireOp",EDGE,"E19"),sQuery(id+"F0.wireOp",EDGE,"E20"),sQuery(id+"F0.wireOp",EDGE,"E21"),sQuery(id+"F0.wireOp",EDGE,"E22"),sQuery(id+"F0.wireOp",EDGE,"E23"),sQuery(id+"F0.wireOp",EDGE,"E24"),sQuery(id+"F0.wireOp",EDGE,"E25"),sQuery(id+"F0.wireOp",EDGE,"E26"),sQuery(id+"F0.wireOp",EDGE,"E27"),sQuery(id+"F0.wireOp",EDGE,"E28"),sQuery(id+"F0.wireOp",EDGE,"E29"),sQuery(id+"F0.wireOp",EDGE,"E30"),sQuery(id+"F0.wireOp",EDGE,"E31"),sQuery(id+"F0.wireOp",EDGE,"E32"),sQuery(id+"F0.wireOp",EDGE,"E33"),sQuery(id+"F0.wireOp",EDGE,"E34"),sQuery(id+"F0.wireOp",EDGE,"E35"),sQuery(id+"F0.wireOp",EDGE,"E36"),sQuery(id+"F0.wireOp",EDGE,"E37"),sQuery(id+"F0.wireOp",EDGE,"E38"),sQuery(id+"F0.wireOp",EDGE,"E39"),sQuery(id+"F0.wireOp",EDGE,"E40"),sQuery(id+"F0.wireOp",EDGE,"E41"),sQuery(id+"F0.wireOp",EDGE,"E42"),sQuery(id+"F0.wireOp",EDGE,"E43"),sQuery(id+"F0.wireOp",EDGE,"E44"),sQuery(id+"F0.wireOp",EDGE,"E45"),sQuery(id+"F0.wireOp",EDGE,"E46"),sQuery(id+"F0.wireOp",EDGE,"E47"),sQuery(id+"F0.wireOp",EDGE,"E48"),sQuery(id+"F0.wireOp",EDGE,"E49"),sQuery(id+"F0.wireOp",EDGE,"E50"),sQuery(id+"F0.wireOp",EDGE,"E51"),sQuery(id+"F0.wireOp",EDGE,"E52"),sQuery(id+"F0.wireOp",EDGE,"E53"),sQuery(id+"F0.wireOp",EDGE,"E54"),sQuery(id+"F0.wireOp",EDGE,"E55"),sQuery(id+"F0.wireOp",EDGE,"E56"),sQuery(id+"F0.wireOp",EDGE,"E57"),sQuery(id+"F0.wireOp",EDGE,"E58"),sQuery(id+"F0.wireOp",EDGE,"E59"),sQuery(id+"F0.wireOp",EDGE,"E60"),sQuery(id+"F0.wireOp",EDGE,"E61"),sQuery(id+"F0.wireOp",EDGE,"E62"),sQuery(id+"F0.wireOp",EDGE,"E63"),sQuery(id+"F0.wireOp",EDGE,"E64"),sQuery(id+"F0.wireOp",EDGE,"E65"),sQuery(id+"F0.wireOp",EDGE,"E66"),sQuery(id+"F0.wireOp",EDGE,"E67"),sQuery(id+"F0.wireOp",EDGE,"E68"),sQuery(id+"F0.wireOp",EDGE,"E69"),sQuery(id+"F0.wireOp",EDGE,"E70"),sQuery(id+"F0.wireOp",EDGE,"E71"),sQuery(id+"F0.wireOp",EDGE,"E72"),sQuery(id+"F0.wireOp",EDGE,"E73"),sQuery(id+"F0.wireOp",EDGE,"E74"),sQuery(id+"F0.wireOp",EDGE,"E75"),sQuery(id+"F0.wireOp",EDGE,"E76"),sQuery(id+"F0.wireOp",EDGE,"E77"),sQuery(id+"F0.wireOp",EDGE,"E78"),sQuery(id+"F0.wireOp",EDGE,"E79"),sQuery(id+"F0.wireOp",EDGE,"E80"),sQuery(id+"F0.wireOp",EDGE,"E81"),sQuery(id+"F0.wireOp",EDGE,"E82"),sQuery(id+"F0.wireOp",EDGE,"E83"),sQuery(id+"F0.wireOp",EDGE,"E84"),sQuery(id+"F0.wireOp",EDGE,"E85"),sQuery(id+"F0.wireOp",EDGE,"E86"),sQuery(id+"F0.wireOp",EDGE,"E87"),sQuery(id+"F0.wireOp",EDGE,"E88"),sQuery(id+"F0.wireOp",EDGE,"E89"),sQuery(id+"F0.wireOp",EDGE,"E90"),sQuery(id+"F0.wireOp",EDGE,"E91"),sQuery(id+"F0.wireOp",EDGE,"E92"),sQuery(id+"F0.wireOp",EDGE,"E93"),sQuery(id+"F0.wireOp",EDGE,"E94"),sQuery(id+"F0.wireOp",EDGE,"E95"),sQuery(id+"F0.wireOp",EDGE,"E96"),sQuery(id+"F0.wireOp",EDGE,"E97"),sQuery(id+"F0.wireOp",EDGE,"E98"),sQuery(id+"F0.wireOp",EDGE,"E99"),sQuery(id+"F0.wireOp",EDGE,"E100"),sQuery(id+"F0.wireOp",EDGE,"E101"),sQuery(id+"F0.wireOp",EDGE,"E102"),sQuery(id+"F0.wireOp",EDGE,"E103"),sQuery(id+"F0.wireOp",EDGE,"E104")])]}),"instanceName":"1"});
            var Q2;
            Q2=makeQuery(id+"F2.opPattern","COPY",BODY,{"derivedFrom":makeQuery(id+"F1.opExtrude","SWEPT_BODY",BODY,{"disambiguationData":[OSD([sQuery(id+"F0.wireOp",EDGE,"E1"),sQuery(id+"F0.wireOp",EDGE,"E2"),sQuery(id+"F0.wireOp",EDGE,"E3"),sQuery(id+"F0.wireOp",EDGE,"E4"),sQuery(id+"F0.wireOp",EDGE,"E5"),sQuery(id+"F0.wireOp",EDGE,"E6"),sQuery(id+"F0.wireOp",EDGE,"E7"),sQuery(id+"F0.wireOp",EDGE,"E8"),sQuery(id+"F0.wireOp",EDGE,"E9"),sQuery(id+"F0.wireOp",EDGE,"E10"),sQuery(id+"F0.wireOp",EDGE,"E11"),sQuery(id+"F0.wireOp",EDGE,"E12"),sQuery(id+"F0.wireOp",EDGE,"E13"),sQuery(id+"F0.wireOp",EDGE,"E14"),sQuery(id+"F0.wireOp",EDGE,"E15"),sQuery(id+"F0.wireOp",EDGE,"E16"),sQuery(id+"F0.wireOp",EDGE,"E17"),sQuery(id+"F0.wireOp",EDGE,"E18"),sQuery(id+"F0.wireOp",EDGE,"E19"),sQuery(id+"F0.wireOp",EDGE,"E20"),sQuery(id+"F0.wireOp",EDGE,"E21"),sQuery(id+"F0.wireOp",EDGE,"E22"),sQuery(id+"F0.wireOp",EDGE,"E23"),sQuery(id+"F0.wireOp",EDGE,"E24"),sQuery(id+"F0.wireOp",EDGE,"E25"),sQuery(id+"F0.wireOp",EDGE,"E26"),sQuery(id+"F0.wireOp",EDGE,"E27"),sQuery(id+"F0.wireOp",EDGE,"E28"),sQuery(id+"F0.wireOp",EDGE,"E29"),sQuery(id+"F0.wireOp",EDGE,"E30"),sQuery(id+"F0.wireOp",EDGE,"E31"),sQuery(id+"F0.wireOp",EDGE,"E32"),sQuery(id+"F0.wireOp",EDGE,"E33"),sQuery(id+"F0.wireOp",EDGE,"E34"),sQuery(id+"F0.wireOp",EDGE,"E35"),sQuery(id+"F0.wireOp",EDGE,"E36"),sQuery(id+"F0.wireOp",EDGE,"E37"),sQuery(id+"F0.wireOp",EDGE,"E38"),sQuery(id+"F0.wireOp",EDGE,"E39"),sQuery(id+"F0.wireOp",EDGE,"E40"),sQuery(id+"F0.wireOp",EDGE,"E41"),sQuery(id+"F0.wireOp",EDGE,"E42"),sQuery(id+"F0.wireOp",EDGE,"E43"),sQuery(id+"F0.wireOp",EDGE,"E44"),sQuery(id+"F0.wireOp",EDGE,"E45"),sQuery(id+"F0.wireOp",EDGE,"E46"),sQuery(id+"F0.wireOp",EDGE,"E47"),sQuery(id+"F0.wireOp",EDGE,"E48"),sQuery(id+"F0.wireOp",EDGE,"E49"),sQuery(id+"F0.wireOp",EDGE,"E50"),sQuery(id+"F0.wireOp",EDGE,"E51"),sQuery(id+"F0.wireOp",EDGE,"E52"),sQuery(id+"F0.wireOp",EDGE,"E53"),sQuery(id+"F0.wireOp",EDGE,"E54"),sQuery(id+"F0.wireOp",EDGE,"E55"),sQuery(id+"F0.wireOp",EDGE,"E56"),sQuery(id+"F0.wireOp",EDGE,"E57"),sQuery(id+"F0.wireOp",EDGE,"E58"),sQuery(id+"F0.wireOp",EDGE,"E59"),sQuery(id+"F0.wireOp",EDGE,"E60"),sQuery(id+"F0.wireOp",EDGE,"E61"),sQuery(id+"F0.wireOp",EDGE,"E62"),sQuery(id+"F0.wireOp",EDGE,"E63"),sQuery(id+"F0.wireOp",EDGE,"E64"),sQuery(id+"F0.wireOp",EDGE,"E65"),sQuery(id+"F0.wireOp",EDGE,"E66"),sQuery(id+"F0.wireOp",EDGE,"E67"),sQuery(id+"F0.wireOp",EDGE,"E68"),sQuery(id+"F0.wireOp",EDGE,"E69"),sQuery(id+"F0.wireOp",EDGE,"E70"),sQuery(id+"F0.wireOp",EDGE,"E71"),sQuery(id+"F0.wireOp",EDGE,"E72"),sQuery(id+"F0.wireOp",EDGE,"E73"),sQuery(id+"F0.wireOp",EDGE,"E74"),sQuery(id+"F0.wireOp",EDGE,"E75"),sQuery(id+"F0.wireOp",EDGE,"E76"),sQuery(id+"F0.wireOp",EDGE,"E77"),sQuery(id+"F0.wireOp",EDGE,"E78"),sQuery(id+"F0.wireOp",EDGE,"E79"),sQuery(id+"F0.wireOp",EDGE,"E80"),sQuery(id+"F0.wireOp",EDGE,"E81"),sQuery(id+"F0.wireOp",EDGE,"E82"),sQuery(id+"F0.wireOp",EDGE,"E83"),sQuery(id+"F0.wireOp",EDGE,"E84"),sQuery(id+"F0.wireOp",EDGE,"E85"),sQuery(id+"F0.wireOp",EDGE,"E86"),sQuery(id+"F0.wireOp",EDGE,"E87"),sQuery(id+"F0.wireOp",EDGE,"E88"),sQuery(id+"F0.wireOp",EDGE,"E89"),sQuery(id+"F0.wireOp",EDGE,"E90"),sQuery(id+"F0.wireOp",EDGE,"E91"),sQuery(id+"F0.wireOp",EDGE,"E92"),sQuery(id+"F0.wireOp",EDGE,"E93"),sQuery(id+"F0.wireOp",EDGE,"E94"),sQuery(id+"F0.wireOp",EDGE,"E95"),sQuery(id+"F0.wireOp",EDGE,"E96"),sQuery(id+"F0.wireOp",EDGE,"E97"),sQuery(id+"F0.wireOp",EDGE,"E98"),sQuery(id+"F0.wireOp",EDGE,"E99"),sQuery(id+"F0.wireOp",EDGE,"E100"),sQuery(id+"F0.wireOp",EDGE,"E101"),sQuery(id+"F0.wireOp",EDGE,"E102"),sQuery(id+"F0.wireOp",EDGE,"E103"),sQuery(id+"F0.wireOp",EDGE,"E104")])]}),"instanceName":"35"});
            var Q3;
            Q3=makeQuery(id+"F2.opPattern","COPY",BODY,{"derivedFrom":makeQuery(id+"F1.opExtrude","SWEPT_BODY",BODY,{"disambiguationData":[OSD([sQuery(id+"F0.wireOp",EDGE,"E1"),sQuery(id+"F0.wireOp",EDGE,"E2"),sQuery(id+"F0.wireOp",EDGE,"E3"),sQuery(id+"F0.wireOp",EDGE,"E4"),sQuery(id+"F0.wireOp",EDGE,"E5"),sQuery(id+"F0.wireOp",EDGE,"E6"),sQuery(id+"F0.wireOp",EDGE,"E7"),sQuery(id+"F0.wireOp",EDGE,"E8"),sQuery(id+"F0.wireOp",EDGE,"E9"),sQuery(id+"F0.wireOp",EDGE,"E10"),sQuery(id+"F0.wireOp",EDGE,"E11"),sQuery(id+"F0.wireOp",EDGE,"E12"),sQuery(id+"F0.wireOp",EDGE,"E13"),sQuery(id+"F0.wireOp",EDGE,"E14"),sQuery(id+"F0.wireOp",EDGE,"E15"),sQuery(id+"F0.wireOp",EDGE,"E16"),sQuery(id+"F0.wireOp",EDGE,"E17"),sQuery(id+"F0.wireOp",EDGE,"E18"),sQuery(id+"F0.wireOp",EDGE,"E19"),sQuery(id+"F0.wireOp",EDGE,"E20"),sQuery(id+"F0.wireOp",EDGE,"E21"),sQuery(id+"F0.wireOp",EDGE,"E22"),sQuery(id+"F0.wireOp",EDGE,"E23"),sQuery(id+"F0.wireOp",EDGE,"E24"),sQuery(id+"F0.wireOp",EDGE,"E25"),sQuery(id+"F0.wireOp",EDGE,"E26"),sQuery(id+"F0.wireOp",EDGE,"E27"),sQuery(id+"F0.wireOp",EDGE,"E28"),sQuery(id+"F0.wireOp",EDGE,"E29"),sQuery(id+"F0.wireOp",EDGE,"E30"),sQuery(id+"F0.wireOp",EDGE,"E31"),sQuery(id+"F0.wireOp",EDGE,"E32"),sQuery(id+"F0.wireOp",EDGE,"E33"),sQuery(id+"F0.wireOp",EDGE,"E34"),sQuery(id+"F0.wireOp",EDGE,"E35"),sQuery(id+"F0.wireOp",EDGE,"E36"),sQuery(id+"F0.wireOp",EDGE,"E37"),sQuery(id+"F0.wireOp",EDGE,"E38"),sQuery(id+"F0.wireOp",EDGE,"E39"),sQuery(id+"F0.wireOp",EDGE,"E40"),sQuery(id+"F0.wireOp",EDGE,"E41"),sQuery(id+"F0.wireOp",EDGE,"E42"),sQuery(id+"F0.wireOp",EDGE,"E43"),sQuery(id+"F0.wireOp",EDGE,"E44"),sQuery(id+"F0.wireOp",EDGE,"E45"),sQuery(id+"F0.wireOp",EDGE,"E46"),sQuery(id+"F0.wireOp",EDGE,"E47"),sQuery(id+"F0.wireOp",EDGE,"E48"),sQuery(id+"F0.wireOp",EDGE,"E49"),sQuery(id+"F0.wireOp",EDGE,"E50"),sQuery(id+"F0.wireOp",EDGE,"E51"),sQuery(id+"F0.wireOp",EDGE,"E52"),sQuery(id+"F0.wireOp",EDGE,"E53"),sQuery(id+"F0.wireOp",EDGE,"E54"),sQuery(id+"F0.wireOp",EDGE,"E55"),sQuery(id+"F0.wireOp",EDGE,"E56"),sQuery(id+"F0.wireOp",EDGE,"E57"),sQuery(id+"F0.wireOp",EDGE,"E58"),sQuery(id+"F0.wireOp",EDGE,"E59"),sQuery(id+"F0.wireOp",EDGE,"E60"),sQuery(id+"F0.wireOp",EDGE,"E61"),sQuery(id+"F0.wireOp",EDGE,"E62"),sQuery(id+"F0.wireOp",EDGE,"E63"),sQuery(id+"F0.wireOp",EDGE,"E64"),sQuery(id+"F0.wireOp",EDGE,"E65"),sQuery(id+"F0.wireOp",EDGE,"E66"),sQuery(id+"F0.wireOp",EDGE,"E67"),sQuery(id+"F0.wireOp",EDGE,"E68"),sQuery(id+"F0.wireOp",EDGE,"E69"),sQuery(id+"F0.wireOp",EDGE,"E70"),sQuery(id+"F0.wireOp",EDGE,"E71"),sQuery(id+"F0.wireOp",EDGE,"E72"),sQuery(id+"F0.wireOp",EDGE,"E73"),sQuery(id+"F0.wireOp",EDGE,"E74"),sQuery(id+"F0.wireOp",EDGE,"E75"),sQuery(id+"F0.wireOp",EDGE,"E76"),sQuery(id+"F0.wireOp",EDGE,"E77"),sQuery(id+"F0.wireOp",EDGE,"E78"),sQuery(id+"F0.wireOp",EDGE,"E79"),sQuery(id+"F0.wireOp",EDGE,"E80"),sQuery(id+"F0.wireOp",EDGE,"E81"),sQuery(id+"F0.wireOp",EDGE,"E82"),sQuery(id+"F0.wireOp",EDGE,"E83"),sQuery(id+"F0.wireOp",EDGE,"E84"),sQuery(id+"F0.wireOp",EDGE,"E85"),sQuery(id+"F0.wireOp",EDGE,"E86"),sQuery(id+"F0.wireOp",EDGE,"E87"),sQuery(id+"F0.wireOp",EDGE,"E88"),sQuery(id+"F0.wireOp",EDGE,"E89"),sQuery(id+"F0.wireOp",EDGE,"E90"),sQuery(id+"F0.wireOp",EDGE,"E91"),sQuery(id+"F0.wireOp",EDGE,"E92"),sQuery(id+"F0.wireOp",EDGE,"E93"),sQuery(id+"F0.wireOp",EDGE,"E94"),sQuery(id+"F0.wireOp",EDGE,"E95"),sQuery(id+"F0.wireOp",EDGE,"E96"),sQuery(id+"F0.wireOp",EDGE,"E97"),sQuery(id+"F0.wireOp",EDGE,"E98"),sQuery(id+"F0.wireOp",EDGE,"E99"),sQuery(id+"F0.wireOp",EDGE,"E100"),sQuery(id+"F0.wireOp",EDGE,"E101"),sQuery(id+"F0.wireOp",EDGE,"E102"),sQuery(id+"F0.wireOp",EDGE,"E103"),sQuery(id+"F0.wireOp",EDGE,"E104")])]}),"instanceName":"36"});
            var Q4;
            Q4=makeQuery(id+"F2.opPattern","COPY",BODY,{"derivedFrom":makeQuery(id+"F1.opExtrude","SWEPT_BODY",BODY,{"disambiguationData":[OSD([sQuery(id+"F0.wireOp",EDGE,"E1"),sQuery(id+"F0.wireOp",EDGE,"E2"),sQuery(id+"F0.wireOp",EDGE,"E3"),sQuery(id+"F0.wireOp",EDGE,"E4"),sQuery(id+"F0.wireOp",EDGE,"E5"),sQuery(id+"F0.wireOp",EDGE,"E6"),sQuery(id+"F0.wireOp",EDGE,"E7"),sQuery(id+"F0.wireOp",EDGE,"E8"),sQuery(id+"F0.wireOp",EDGE,"E9"),sQuery(id+"F0.wireOp",EDGE,"E10"),sQuery(id+"F0.wireOp",EDGE,"E11"),sQuery(id+"F0.wireOp",EDGE,"E12"),sQuery(id+"F0.wireOp",EDGE,"E13"),sQuery(id+"F0.wireOp",EDGE,"E14"),sQuery(id+"F0.wireOp",EDGE,"E15"),sQuery(id+"F0.wireOp",EDGE,"E16"),sQuery(id+"F0.wireOp",EDGE,"E17"),sQuery(id+"F0.wireOp",EDGE,"E18"),sQuery(id+"F0.wireOp",EDGE,"E19"),sQuery(id+"F0.wireOp",EDGE,"E20"),sQuery(id+"F0.wireOp",EDGE,"E21"),sQuery(id+"F0.wireOp",EDGE,"E22"),sQuery(id+"F0.wireOp",EDGE,"E23"),sQuery(id+"F0.wireOp",EDGE,"E24"),sQuery(id+"F0.wireOp",EDGE,"E25"),sQuery(id+"F0.wireOp",EDGE,"E26"),sQuery(id+"F0.wireOp",EDGE,"E27"),sQuery(id+"F0.wireOp",EDGE,"E28"),sQuery(id+"F0.wireOp",EDGE,"E29"),sQuery(id+"F0.wireOp",EDGE,"E30"),sQuery(id+"F0.wireOp",EDGE,"E31"),sQuery(id+"F0.wireOp",EDGE,"E32"),sQuery(id+"F0.wireOp",EDGE,"E33"),sQuery(id+"F0.wireOp",EDGE,"E34"),sQuery(id+"F0.wireOp",EDGE,"E35"),sQuery(id+"F0.wireOp",EDGE,"E36"),sQuery(id+"F0.wireOp",EDGE,"E37"),sQuery(id+"F0.wireOp",EDGE,"E38"),sQuery(id+"F0.wireOp",EDGE,"E39"),sQuery(id+"F0.wireOp",EDGE,"E40"),sQuery(id+"F0.wireOp",EDGE,"E41"),sQuery(id+"F0.wireOp",EDGE,"E42"),sQuery(id+"F0.wireOp",EDGE,"E43"),sQuery(id+"F0.wireOp",EDGE,"E44"),sQuery(id+"F0.wireOp",EDGE,"E45"),sQuery(id+"F0.wireOp",EDGE,"E46"),sQuery(id+"F0.wireOp",EDGE,"E47"),sQuery(id+"F0.wireOp",EDGE,"E48"),sQuery(id+"F0.wireOp",EDGE,"E49"),sQuery(id+"F0.wireOp",EDGE,"E50"),sQuery(id+"F0.wireOp",EDGE,"E51"),sQuery(id+"F0.wireOp",EDGE,"E52"),sQuery(id+"F0.wireOp",EDGE,"E53"),sQuery(id+"F0.wireOp",EDGE,"E54"),sQuery(id+"F0.wireOp",EDGE,"E55"),sQuery(id+"F0.wireOp",EDGE,"E56"),sQuery(id+"F0.wireOp",EDGE,"E57"),sQuery(id+"F0.wireOp",EDGE,"E58"),sQuery(id+"F0.wireOp",EDGE,"E59"),sQuery(id+"F0.wireOp",EDGE,"E60"),sQuery(id+"F0.wireOp",EDGE,"E61"),sQuery(id+"F0.wireOp",EDGE,"E62"),sQuery(id+"F0.wireOp",EDGE,"E63"),sQuery(id+"F0.wireOp",EDGE,"E64"),sQuery(id+"F0.wireOp",EDGE,"E65"),sQuery(id+"F0.wireOp",EDGE,"E66"),sQuery(id+"F0.wireOp",EDGE,"E67"),sQuery(id+"F0.wireOp",EDGE,"E68"),sQuery(id+"F0.wireOp",EDGE,"E69"),sQuery(id+"F0.wireOp",EDGE,"E70"),sQuery(id+"F0.wireOp",EDGE,"E71"),sQuery(id+"F0.wireOp",EDGE,"E72"),sQuery(id+"F0.wireOp",EDGE,"E73"),sQuery(id+"F0.wireOp",EDGE,"E74"),sQuery(id+"F0.wireOp",EDGE,"E75"),sQuery(id+"F0.wireOp",EDGE,"E76"),sQuery(id+"F0.wireOp",EDGE,"E77"),sQuery(id+"F0.wireOp",EDGE,"E78"),sQuery(id+"F0.wireOp",EDGE,"E79"),sQuery(id+"F0.wireOp",EDGE,"E80"),sQuery(id+"F0.wireOp",EDGE,"E81"),sQuery(id+"F0.wireOp",EDGE,"E82"),sQuery(id+"F0.wireOp",EDGE,"E83"),sQuery(id+"F0.wireOp",EDGE,"E84"),sQuery(id+"F0.wireOp",EDGE,"E85"),sQuery(id+"F0.wireOp",EDGE,"E86"),sQuery(id+"F0.wireOp",EDGE,"E87"),sQuery(id+"F0.wireOp",EDGE,"E88"),sQuery(id+"F0.wireOp",EDGE,"E89"),sQuery(id+"F0.wireOp",EDGE,"E90"),sQuery(id+"F0.wireOp",EDGE,"E91"),sQuery(id+"F0.wireOp",EDGE,"E92"),sQuery(id+"F0.wireOp",EDGE,"E93"),sQuery(id+"F0.wireOp",EDGE,"E94"),sQuery(id+"F0.wireOp",EDGE,"E95"),sQuery(id+"F0.wireOp",EDGE,"E96"),sQuery(id+"F0.wireOp",EDGE,"E97"),sQuery(id+"F0.wireOp",EDGE,"E98"),sQuery(id+"F0.wireOp",EDGE,"E99"),sQuery(id+"F0.wireOp",EDGE,"E100"),sQuery(id+"F0.wireOp",EDGE,"E101"),sQuery(id+"F0.wireOp",EDGE,"E102"),sQuery(id+"F0.wireOp",EDGE,"E103"),sQuery(id+"F0.wireOp",EDGE,"E104")])]}),"instanceName":"37"});
            var Q5;
            Q5=makeQuery(id+"F2.opPattern","COPY",BODY,{"derivedFrom":makeQuery(id+"F1.opExtrude","SWEPT_BODY",BODY,{"disambiguationData":[OSD([sQuery(id+"F0.wireOp",EDGE,"E1"),sQuery(id+"F0.wireOp",EDGE,"E2"),sQuery(id+"F0.wireOp",EDGE,"E3"),sQuery(id+"F0.wireOp",EDGE,"E4"),sQuery(id+"F0.wireOp",EDGE,"E5"),sQuery(id+"F0.wireOp",EDGE,"E6"),sQuery(id+"F0.wireOp",EDGE,"E7"),sQuery(id+"F0.wireOp",EDGE,"E8"),sQuery(id+"F0.wireOp",EDGE,"E9"),sQuery(id+"F0.wireOp",EDGE,"E10"),sQuery(id+"F0.wireOp",EDGE,"E11"),sQuery(id+"F0.wireOp",EDGE,"E12"),sQuery(id+"F0.wireOp",EDGE,"E13"),sQuery(id+"F0.wireOp",EDGE,"E14"),sQuery(id+"F0.wireOp",EDGE,"E15"),sQuery(id+"F0.wireOp",EDGE,"E16"),sQuery(id+"F0.wireOp",EDGE,"E17"),sQuery(id+"F0.wireOp",EDGE,"E18"),sQuery(id+"F0.wireOp",EDGE,"E19"),sQuery(id+"F0.wireOp",EDGE,"E20"),sQuery(id+"F0.wireOp",EDGE,"E21"),sQuery(id+"F0.wireOp",EDGE,"E22"),sQuery(id+"F0.wireOp",EDGE,"E23"),sQuery(id+"F0.wireOp",EDGE,"E24"),sQuery(id+"F0.wireOp",EDGE,"E25"),sQuery(id+"F0.wireOp",EDGE,"E26"),sQuery(id+"F0.wireOp",EDGE,"E27"),sQuery(id+"F0.wireOp",EDGE,"E28"),sQuery(id+"F0.wireOp",EDGE,"E29"),sQuery(id+"F0.wireOp",EDGE,"E30"),sQuery(id+"F0.wireOp",EDGE,"E31"),sQuery(id+"F0.wireOp",EDGE,"E32"),sQuery(id+"F0.wireOp",EDGE,"E33"),sQuery(id+"F0.wireOp",EDGE,"E34"),sQuery(id+"F0.wireOp",EDGE,"E35"),sQuery(id+"F0.wireOp",EDGE,"E36"),sQuery(id+"F0.wireOp",EDGE,"E37"),sQuery(id+"F0.wireOp",EDGE,"E38"),sQuery(id+"F0.wireOp",EDGE,"E39"),sQuery(id+"F0.wireOp",EDGE,"E40"),sQuery(id+"F0.wireOp",EDGE,"E41"),sQuery(id+"F0.wireOp",EDGE,"E42"),sQuery(id+"F0.wireOp",EDGE,"E43"),sQuery(id+"F0.wireOp",EDGE,"E44"),sQuery(id+"F0.wireOp",EDGE,"E45"),sQuery(id+"F0.wireOp",EDGE,"E46"),sQuery(id+"F0.wireOp",EDGE,"E47"),sQuery(id+"F0.wireOp",EDGE,"E48"),sQuery(id+"F0.wireOp",EDGE,"E49"),sQuery(id+"F0.wireOp",EDGE,"E50"),sQuery(id+"F0.wireOp",EDGE,"E51"),sQuery(id+"F0.wireOp",EDGE,"E52"),sQuery(id+"F0.wireOp",EDGE,"E53"),sQuery(id+"F0.wireOp",EDGE,"E54"),sQuery(id+"F0.wireOp",EDGE,"E55"),sQuery(id+"F0.wireOp",EDGE,"E56"),sQuery(id+"F0.wireOp",EDGE,"E57"),sQuery(id+"F0.wireOp",EDGE,"E58"),sQuery(id+"F0.wireOp",EDGE,"E59"),sQuery(id+"F0.wireOp",EDGE,"E60"),sQuery(id+"F0.wireOp",EDGE,"E61"),sQuery(id+"F0.wireOp",EDGE,"E62"),sQuery(id+"F0.wireOp",EDGE,"E63"),sQuery(id+"F0.wireOp",EDGE,"E64"),sQuery(id+"F0.wireOp",EDGE,"E65"),sQuery(id+"F0.wireOp",EDGE,"E66"),sQuery(id+"F0.wireOp",EDGE,"E67"),sQuery(id+"F0.wireOp",EDGE,"E68"),sQuery(id+"F0.wireOp",EDGE,"E69"),sQuery(id+"F0.wireOp",EDGE,"E70"),sQuery(id+"F0.wireOp",EDGE,"E71"),sQuery(id+"F0.wireOp",EDGE,"E72"),sQuery(id+"F0.wireOp",EDGE,"E73"),sQuery(id+"F0.wireOp",EDGE,"E74"),sQuery(id+"F0.wireOp",EDGE,"E75"),sQuery(id+"F0.wireOp",EDGE,"E76"),sQuery(id+"F0.wireOp",EDGE,"E77"),sQuery(id+"F0.wireOp",EDGE,"E78"),sQuery(id+"F0.wireOp",EDGE,"E79"),sQuery(id+"F0.wireOp",EDGE,"E80"),sQuery(id+"F0.wireOp",EDGE,"E81"),sQuery(id+"F0.wireOp",EDGE,"E82"),sQuery(id+"F0.wireOp",EDGE,"E83"),sQuery(id+"F0.wireOp",EDGE,"E84"),sQuery(id+"F0.wireOp",EDGE,"E85"),sQuery(id+"F0.wireOp",EDGE,"E86"),sQuery(id+"F0.wireOp",EDGE,"E87"),sQuery(id+"F0.wireOp",EDGE,"E88"),sQuery(id+"F0.wireOp",EDGE,"E89"),sQuery(id+"F0.wireOp",EDGE,"E90"),sQuery(id+"F0.wireOp",EDGE,"E91"),sQuery(id+"F0.wireOp",EDGE,"E92"),sQuery(id+"F0.wireOp",EDGE,"E93"),sQuery(id+"F0.wireOp",EDGE,"E94"),sQuery(id+"F0.wireOp",EDGE,"E95"),sQuery(id+"F0.wireOp",EDGE,"E96"),sQuery(id+"F0.wireOp",EDGE,"E97"),sQuery(id+"F0.wireOp",EDGE,"E98"),sQuery(id+"F0.wireOp",EDGE,"E99"),sQuery(id+"F0.wireOp",EDGE,"E100"),sQuery(id+"F0.wireOp",EDGE,"E101"),sQuery(id+"F0.wireOp",EDGE,"E102"),sQuery(id+"F0.wireOp",EDGE,"E103"),sQuery(id+"F0.wireOp",EDGE,"E104")])]}),"instanceName":"38"});
            var Q6;
            Q6=makeQuery(id+"F2.opPattern","COPY",BODY,{"derivedFrom":makeQuery(id+"F1.opExtrude","SWEPT_BODY",BODY,{"disambiguationData":[OSD([sQuery(id+"F0.wireOp",EDGE,"E1"),sQuery(id+"F0.wireOp",EDGE,"E2"),sQuery(id+"F0.wireOp",EDGE,"E3"),sQuery(id+"F0.wireOp",EDGE,"E4"),sQuery(id+"F0.wireOp",EDGE,"E5"),sQuery(id+"F0.wireOp",EDGE,"E6"),sQuery(id+"F0.wireOp",EDGE,"E7"),sQuery(id+"F0.wireOp",EDGE,"E8"),sQuery(id+"F0.wireOp",EDGE,"E9"),sQuery(id+"F0.wireOp",EDGE,"E10"),sQuery(id+"F0.wireOp",EDGE,"E11"),sQuery(id+"F0.wireOp",EDGE,"E12"),sQuery(id+"F0.wireOp",EDGE,"E13"),sQuery(id+"F0.wireOp",EDGE,"E14"),sQuery(id+"F0.wireOp",EDGE,"E15"),sQuery(id+"F0.wireOp",EDGE,"E16"),sQuery(id+"F0.wireOp",EDGE,"E17"),sQuery(id+"F0.wireOp",EDGE,"E18"),sQuery(id+"F0.wireOp",EDGE,"E19"),sQuery(id+"F0.wireOp",EDGE,"E20"),sQuery(id+"F0.wireOp",EDGE,"E21"),sQuery(id+"F0.wireOp",EDGE,"E22"),sQuery(id+"F0.wireOp",EDGE,"E23"),sQuery(id+"F0.wireOp",EDGE,"E24"),sQuery(id+"F0.wireOp",EDGE,"E25"),sQuery(id+"F0.wireOp",EDGE,"E26"),sQuery(id+"F0.wireOp",EDGE,"E27"),sQuery(id+"F0.wireOp",EDGE,"E28"),sQuery(id+"F0.wireOp",EDGE,"E29"),sQuery(id+"F0.wireOp",EDGE,"E30"),sQuery(id+"F0.wireOp",EDGE,"E31"),sQuery(id+"F0.wireOp",EDGE,"E32"),sQuery(id+"F0.wireOp",EDGE,"E33"),sQuery(id+"F0.wireOp",EDGE,"E34"),sQuery(id+"F0.wireOp",EDGE,"E35"),sQuery(id+"F0.wireOp",EDGE,"E36"),sQuery(id+"F0.wireOp",EDGE,"E37"),sQuery(id+"F0.wireOp",EDGE,"E38"),sQuery(id+"F0.wireOp",EDGE,"E39"),sQuery(id+"F0.wireOp",EDGE,"E40"),sQuery(id+"F0.wireOp",EDGE,"E41"),sQuery(id+"F0.wireOp",EDGE,"E42"),sQuery(id+"F0.wireOp",EDGE,"E43"),sQuery(id+"F0.wireOp",EDGE,"E44"),sQuery(id+"F0.wireOp",EDGE,"E45"),sQuery(id+"F0.wireOp",EDGE,"E46"),sQuery(id+"F0.wireOp",EDGE,"E47"),sQuery(id+"F0.wireOp",EDGE,"E48"),sQuery(id+"F0.wireOp",EDGE,"E49"),sQuery(id+"F0.wireOp",EDGE,"E50"),sQuery(id+"F0.wireOp",EDGE,"E51"),sQuery(id+"F0.wireOp",EDGE,"E52"),sQuery(id+"F0.wireOp",EDGE,"E53"),sQuery(id+"F0.wireOp",EDGE,"E54"),sQuery(id+"F0.wireOp",EDGE,"E55"),sQuery(id+"F0.wireOp",EDGE,"E56"),sQuery(id+"F0.wireOp",EDGE,"E57"),sQuery(id+"F0.wireOp",EDGE,"E58"),sQuery(id+"F0.wireOp",EDGE,"E59"),sQuery(id+"F0.wireOp",EDGE,"E60"),sQuery(id+"F0.wireOp",EDGE,"E61"),sQuery(id+"F0.wireOp",EDGE,"E62"),sQuery(id+"F0.wireOp",EDGE,"E63"),sQuery(id+"F0.wireOp",EDGE,"E64"),sQuery(id+"F0.wireOp",EDGE,"E65"),sQuery(id+"F0.wireOp",EDGE,"E66"),sQuery(id+"F0.wireOp",EDGE,"E67"),sQuery(id+"F0.wireOp",EDGE,"E68"),sQuery(id+"F0.wireOp",EDGE,"E69"),sQuery(id+"F0.wireOp",EDGE,"E70"),sQuery(id+"F0.wireOp",EDGE,"E71"),sQuery(id+"F0.wireOp",EDGE,"E72"),sQuery(id+"F0.wireOp",EDGE,"E73"),sQuery(id+"F0.wireOp",EDGE,"E74"),sQuery(id+"F0.wireOp",EDGE,"E75"),sQuery(id+"F0.wireOp",EDGE,"E76"),sQuery(id+"F0.wireOp",EDGE,"E77"),sQuery(id+"F0.wireOp",EDGE,"E78"),sQuery(id+"F0.wireOp",EDGE,"E79"),sQuery(id+"F0.wireOp",EDGE,"E80"),sQuery(id+"F0.wireOp",EDGE,"E81"),sQuery(id+"F0.wireOp",EDGE,"E82"),sQuery(id+"F0.wireOp",EDGE,"E83"),sQuery(id+"F0.wireOp",EDGE,"E84"),sQuery(id+"F0.wireOp",EDGE,"E85"),sQuery(id+"F0.wireOp",EDGE,"E86"),sQuery(id+"F0.wireOp",EDGE,"E87"),sQuery(id+"F0.wireOp",EDGE,"E88"),sQuery(id+"F0.wireOp",EDGE,"E89"),sQuery(id+"F0.wireOp",EDGE,"E90"),sQuery(id+"F0.wireOp",EDGE,"E91"),sQuery(id+"F0.wireOp",EDGE,"E92"),sQuery(id+"F0.wireOp",EDGE,"E93"),sQuery(id+"F0.wireOp",EDGE,"E94"),sQuery(id+"F0.wireOp",EDGE,"E95"),sQuery(id+"F0.wireOp",EDGE,"E96"),sQuery(id+"F0.wireOp",EDGE,"E97"),sQuery(id+"F0.wireOp",EDGE,"E98"),sQuery(id+"F0.wireOp",EDGE,"E99"),sQuery(id+"F0.wireOp",EDGE,"E100"),sQuery(id+"F0.wireOp",EDGE,"E101"),sQuery(id+"F0.wireOp",EDGE,"E102"),sQuery(id+"F0.wireOp",EDGE,"E103"),sQuery(id+"F0.wireOp",EDGE,"E104")])]}),"instanceName":"39"});
            var Q7;
            Q7=makeQuery(id+"F2.opPattern","COPY",BODY,{"derivedFrom":makeQuery(id+"F1.opExtrude","SWEPT_BODY",BODY,{"disambiguationData":[OSD([sQuery(id+"F0.wireOp",EDGE,"E1"),sQuery(id+"F0.wireOp",EDGE,"E2"),sQuery(id+"F0.wireOp",EDGE,"E3"),sQuery(id+"F0.wireOp",EDGE,"E4"),sQuery(id+"F0.wireOp",EDGE,"E5"),sQuery(id+"F0.wireOp",EDGE,"E6"),sQuery(id+"F0.wireOp",EDGE,"E7"),sQuery(id+"F0.wireOp",EDGE,"E8"),sQuery(id+"F0.wireOp",EDGE,"E9"),sQuery(id+"F0.wireOp",EDGE,"E10"),sQuery(id+"F0.wireOp",EDGE,"E11"),sQuery(id+"F0.wireOp",EDGE,"E12"),sQuery(id+"F0.wireOp",EDGE,"E13"),sQuery(id+"F0.wireOp",EDGE,"E14"),sQuery(id+"F0.wireOp",EDGE,"E15"),sQuery(id+"F0.wireOp",EDGE,"E16"),sQuery(id+"F0.wireOp",EDGE,"E17"),sQuery(id+"F0.wireOp",EDGE,"E18"),sQuery(id+"F0.wireOp",EDGE,"E19"),sQuery(id+"F0.wireOp",EDGE,"E20"),sQuery(id+"F0.wireOp",EDGE,"E21"),sQuery(id+"F0.wireOp",EDGE,"E22"),sQuery(id+"F0.wireOp",EDGE,"E23"),sQuery(id+"F0.wireOp",EDGE,"E24"),sQuery(id+"F0.wireOp",EDGE,"E25"),sQuery(id+"F0.wireOp",EDGE,"E26"),sQuery(id+"F0.wireOp",EDGE,"E27"),sQuery(id+"F0.wireOp",EDGE,"E28"),sQuery(id+"F0.wireOp",EDGE,"E29"),sQuery(id+"F0.wireOp",EDGE,"E30"),sQuery(id+"F0.wireOp",EDGE,"E31"),sQuery(id+"F0.wireOp",EDGE,"E32"),sQuery(id+"F0.wireOp",EDGE,"E33"),sQuery(id+"F0.wireOp",EDGE,"E34"),sQuery(id+"F0.wireOp",EDGE,"E35"),sQuery(id+"F0.wireOp",EDGE,"E36"),sQuery(id+"F0.wireOp",EDGE,"E37"),sQuery(id+"F0.wireOp",EDGE,"E38"),sQuery(id+"F0.wireOp",EDGE,"E39"),sQuery(id+"F0.wireOp",EDGE,"E40"),sQuery(id+"F0.wireOp",EDGE,"E41"),sQuery(id+"F0.wireOp",EDGE,"E42"),sQuery(id+"F0.wireOp",EDGE,"E43"),sQuery(id+"F0.wireOp",EDGE,"E44"),sQuery(id+"F0.wireOp",EDGE,"E45"),sQuery(id+"F0.wireOp",EDGE,"E46"),sQuery(id+"F0.wireOp",EDGE,"E47"),sQuery(id+"F0.wireOp",EDGE,"E48"),sQuery(id+"F0.wireOp",EDGE,"E49"),sQuery(id+"F0.wireOp",EDGE,"E50"),sQuery(id+"F0.wireOp",EDGE,"E51"),sQuery(id+"F0.wireOp",EDGE,"E52"),sQuery(id+"F0.wireOp",EDGE,"E53"),sQuery(id+"F0.wireOp",EDGE,"E54"),sQuery(id+"F0.wireOp",EDGE,"E55"),sQuery(id+"F0.wireOp",EDGE,"E56"),sQuery(id+"F0.wireOp",EDGE,"E57"),sQuery(id+"F0.wireOp",EDGE,"E58"),sQuery(id+"F0.wireOp",EDGE,"E59"),sQuery(id+"F0.wireOp",EDGE,"E60"),sQuery(id+"F0.wireOp",EDGE,"E61"),sQuery(id+"F0.wireOp",EDGE,"E62"),sQuery(id+"F0.wireOp",EDGE,"E63"),sQuery(id+"F0.wireOp",EDGE,"E64"),sQuery(id+"F0.wireOp",EDGE,"E65"),sQuery(id+"F0.wireOp",EDGE,"E66"),sQuery(id+"F0.wireOp",EDGE,"E67"),sQuery(id+"F0.wireOp",EDGE,"E68"),sQuery(id+"F0.wireOp",EDGE,"E69"),sQuery(id+"F0.wireOp",EDGE,"E70"),sQuery(id+"F0.wireOp",EDGE,"E71"),sQuery(id+"F0.wireOp",EDGE,"E72"),sQuery(id+"F0.wireOp",EDGE,"E73"),sQuery(id+"F0.wireOp",EDGE,"E74"),sQuery(id+"F0.wireOp",EDGE,"E75"),sQuery(id+"F0.wireOp",EDGE,"E76"),sQuery(id+"F0.wireOp",EDGE,"E77"),sQuery(id+"F0.wireOp",EDGE,"E78"),sQuery(id+"F0.wireOp",EDGE,"E79"),sQuery(id+"F0.wireOp",EDGE,"E80"),sQuery(id+"F0.wireOp",EDGE,"E81"),sQuery(id+"F0.wireOp",EDGE,"E82"),sQuery(id+"F0.wireOp",EDGE,"E83"),sQuery(id+"F0.wireOp",EDGE,"E84"),sQuery(id+"F0.wireOp",EDGE,"E85"),sQuery(id+"F0.wireOp",EDGE,"E86"),sQuery(id+"F0.wireOp",EDGE,"E87"),sQuery(id+"F0.wireOp",EDGE,"E88"),sQuery(id+"F0.wireOp",EDGE,"E89"),sQuery(id+"F0.wireOp",EDGE,"E90"),sQuery(id+"F0.wireOp",EDGE,"E91"),sQuery(id+"F0.wireOp",EDGE,"E92"),sQuery(id+"F0.wireOp",EDGE,"E93"),sQuery(id+"F0.wireOp",EDGE,"E94"),sQuery(id+"F0.wireOp",EDGE,"E95"),sQuery(id+"F0.wireOp",EDGE,"E96"),sQuery(id+"F0.wireOp",EDGE,"E97"),sQuery(id+"F0.wireOp",EDGE,"E98"),sQuery(id+"F0.wireOp",EDGE,"E99"),sQuery(id+"F0.wireOp",EDGE,"E100"),sQuery(id+"F0.wireOp",EDGE,"E101"),sQuery(id+"F0.wireOp",EDGE,"E102"),sQuery(id+"F0.wireOp",EDGE,"E103"),sQuery(id+"F0.wireOp",EDGE,"E104")])]}),"instanceName":"40"});
            var Q8;
            Q8=makeQuery(id+"F2.opPattern","COPY",BODY,{"derivedFrom":makeQuery(id+"F1.opExtrude","SWEPT_BODY",BODY,{"disambiguationData":[OSD([sQuery(id+"F0.wireOp",EDGE,"E1"),sQuery(id+"F0.wireOp",EDGE,"E2"),sQuery(id+"F0.wireOp",EDGE,"E3"),sQuery(id+"F0.wireOp",EDGE,"E4"),sQuery(id+"F0.wireOp",EDGE,"E5"),sQuery(id+"F0.wireOp",EDGE,"E6"),sQuery(id+"F0.wireOp",EDGE,"E7"),sQuery(id+"F0.wireOp",EDGE,"E8"),sQuery(id+"F0.wireOp",EDGE,"E9"),sQuery(id+"F0.wireOp",EDGE,"E10"),sQuery(id+"F0.wireOp",EDGE,"E11"),sQuery(id+"F0.wireOp",EDGE,"E12"),sQuery(id+"F0.wireOp",EDGE,"E13"),sQuery(id+"F0.wireOp",EDGE,"E14"),sQuery(id+"F0.wireOp",EDGE,"E15"),sQuery(id+"F0.wireOp",EDGE,"E16"),sQuery(id+"F0.wireOp",EDGE,"E17"),sQuery(id+"F0.wireOp",EDGE,"E18"),sQuery(id+"F0.wireOp",EDGE,"E19"),sQuery(id+"F0.wireOp",EDGE,"E20"),sQuery(id+"F0.wireOp",EDGE,"E21"),sQuery(id+"F0.wireOp",EDGE,"E22"),sQuery(id+"F0.wireOp",EDGE,"E23"),sQuery(id+"F0.wireOp",EDGE,"E24"),sQuery(id+"F0.wireOp",EDGE,"E25"),sQuery(id+"F0.wireOp",EDGE,"E26"),sQuery(id+"F0.wireOp",EDGE,"E27"),sQuery(id+"F0.wireOp",EDGE,"E28"),sQuery(id+"F0.wireOp",EDGE,"E29"),sQuery(id+"F0.wireOp",EDGE,"E30"),sQuery(id+"F0.wireOp",EDGE,"E31"),sQuery(id+"F0.wireOp",EDGE,"E32"),sQuery(id+"F0.wireOp",EDGE,"E33"),sQuery(id+"F0.wireOp",EDGE,"E34"),sQuery(id+"F0.wireOp",EDGE,"E35"),sQuery(id+"F0.wireOp",EDGE,"E36"),sQuery(id+"F0.wireOp",EDGE,"E37"),sQuery(id+"F0.wireOp",EDGE,"E38"),sQuery(id+"F0.wireOp",EDGE,"E39"),sQuery(id+"F0.wireOp",EDGE,"E40"),sQuery(id+"F0.wireOp",EDGE,"E41"),sQuery(id+"F0.wireOp",EDGE,"E42"),sQuery(id+"F0.wireOp",EDGE,"E43"),sQuery(id+"F0.wireOp",EDGE,"E44"),sQuery(id+"F0.wireOp",EDGE,"E45"),sQuery(id+"F0.wireOp",EDGE,"E46"),sQuery(id+"F0.wireOp",EDGE,"E47"),sQuery(id+"F0.wireOp",EDGE,"E48"),sQuery(id+"F0.wireOp",EDGE,"E49"),sQuery(id+"F0.wireOp",EDGE,"E50"),sQuery(id+"F0.wireOp",EDGE,"E51"),sQuery(id+"F0.wireOp",EDGE,"E52"),sQuery(id+"F0.wireOp",EDGE,"E53"),sQuery(id+"F0.wireOp",EDGE,"E54"),sQuery(id+"F0.wireOp",EDGE,"E55"),sQuery(id+"F0.wireOp",EDGE,"E56"),sQuery(id+"F0.wireOp",EDGE,"E57"),sQuery(id+"F0.wireOp",EDGE,"E58"),sQuery(id+"F0.wireOp",EDGE,"E59"),sQuery(id+"F0.wireOp",EDGE,"E60"),sQuery(id+"F0.wireOp",EDGE,"E61"),sQuery(id+"F0.wireOp",EDGE,"E62"),sQuery(id+"F0.wireOp",EDGE,"E63"),sQuery(id+"F0.wireOp",EDGE,"E64"),sQuery(id+"F0.wireOp",EDGE,"E65"),sQuery(id+"F0.wireOp",EDGE,"E66"),sQuery(id+"F0.wireOp",EDGE,"E67"),sQuery(id+"F0.wireOp",EDGE,"E68"),sQuery(id+"F0.wireOp",EDGE,"E69"),sQuery(id+"F0.wireOp",EDGE,"E70"),sQuery(id+"F0.wireOp",EDGE,"E71"),sQuery(id+"F0.wireOp",EDGE,"E72"),sQuery(id+"F0.wireOp",EDGE,"E73"),sQuery(id+"F0.wireOp",EDGE,"E74"),sQuery(id+"F0.wireOp",EDGE,"E75"),sQuery(id+"F0.wireOp",EDGE,"E76"),sQuery(id+"F0.wireOp",EDGE,"E77"),sQuery(id+"F0.wireOp",EDGE,"E78"),sQuery(id+"F0.wireOp",EDGE,"E79"),sQuery(id+"F0.wireOp",EDGE,"E80"),sQuery(id+"F0.wireOp",EDGE,"E81"),sQuery(id+"F0.wireOp",EDGE,"E82"),sQuery(id+"F0.wireOp",EDGE,"E83"),sQuery(id+"F0.wireOp",EDGE,"E84"),sQuery(id+"F0.wireOp",EDGE,"E85"),sQuery(id+"F0.wireOp",EDGE,"E86"),sQuery(id+"F0.wireOp",EDGE,"E87"),sQuery(id+"F0.wireOp",EDGE,"E88"),sQuery(id+"F0.wireOp",EDGE,"E89"),sQuery(id+"F0.wireOp",EDGE,"E90"),sQuery(id+"F0.wireOp",EDGE,"E91"),sQuery(id+"F0.wireOp",EDGE,"E92"),sQuery(id+"F0.wireOp",EDGE,"E93"),sQuery(id+"F0.wireOp",EDGE,"E94"),sQuery(id+"F0.wireOp",EDGE,"E95"),sQuery(id+"F0.wireOp",EDGE,"E96"),sQuery(id+"F0.wireOp",EDGE,"E97"),sQuery(id+"F0.wireOp",EDGE,"E98"),sQuery(id+"F0.wireOp",EDGE,"E99"),sQuery(id+"F0.wireOp",EDGE,"E100"),sQuery(id+"F0.wireOp",EDGE,"E101"),sQuery(id+"F0.wireOp",EDGE,"E102"),sQuery(id+"F0.wireOp",EDGE,"E103"),sQuery(id+"F0.wireOp",EDGE,"E104")])]}),"instanceName":"41"});
            var Q9;
            Q9=makeQuery(id+"F2.opPattern","COPY",BODY,{"derivedFrom":makeQuery(id+"F1.opExtrude","SWEPT_BODY",BODY,{"disambiguationData":[OSD([sQuery(id+"F0.wireOp",EDGE,"E1"),sQuery(id+"F0.wireOp",EDGE,"E2"),sQuery(id+"F0.wireOp",EDGE,"E3"),sQuery(id+"F0.wireOp",EDGE,"E4"),sQuery(id+"F0.wireOp",EDGE,"E5"),sQuery(id+"F0.wireOp",EDGE,"E6"),sQuery(id+"F0.wireOp",EDGE,"E7"),sQuery(id+"F0.wireOp",EDGE,"E8"),sQuery(id+"F0.wireOp",EDGE,"E9"),sQuery(id+"F0.wireOp",EDGE,"E10"),sQuery(id+"F0.wireOp",EDGE,"E11"),sQuery(id+"F0.wireOp",EDGE,"E12"),sQuery(id+"F0.wireOp",EDGE,"E13"),sQuery(id+"F0.wireOp",EDGE,"E14"),sQuery(id+"F0.wireOp",EDGE,"E15"),sQuery(id+"F0.wireOp",EDGE,"E16"),sQuery(id+"F0.wireOp",EDGE,"E17"),sQuery(id+"F0.wireOp",EDGE,"E18"),sQuery(id+"F0.wireOp",EDGE,"E19"),sQuery(id+"F0.wireOp",EDGE,"E20"),sQuery(id+"F0.wireOp",EDGE,"E21"),sQuery(id+"F0.wireOp",EDGE,"E22"),sQuery(id+"F0.wireOp",EDGE,"E23"),sQuery(id+"F0.wireOp",EDGE,"E24"),sQuery(id+"F0.wireOp",EDGE,"E25"),sQuery(id+"F0.wireOp",EDGE,"E26"),sQuery(id+"F0.wireOp",EDGE,"E27"),sQuery(id+"F0.wireOp",EDGE,"E28"),sQuery(id+"F0.wireOp",EDGE,"E29"),sQuery(id+"F0.wireOp",EDGE,"E30"),sQuery(id+"F0.wireOp",EDGE,"E31"),sQuery(id+"F0.wireOp",EDGE,"E32"),sQuery(id+"F0.wireOp",EDGE,"E33"),sQuery(id+"F0.wireOp",EDGE,"E34"),sQuery(id+"F0.wireOp",EDGE,"E35"),sQuery(id+"F0.wireOp",EDGE,"E36"),sQuery(id+"F0.wireOp",EDGE,"E37"),sQuery(id+"F0.wireOp",EDGE,"E38"),sQuery(id+"F0.wireOp",EDGE,"E39"),sQuery(id+"F0.wireOp",EDGE,"E40"),sQuery(id+"F0.wireOp",EDGE,"E41"),sQuery(id+"F0.wireOp",EDGE,"E42"),sQuery(id+"F0.wireOp",EDGE,"E43"),sQuery(id+"F0.wireOp",EDGE,"E44"),sQuery(id+"F0.wireOp",EDGE,"E45"),sQuery(id+"F0.wireOp",EDGE,"E46"),sQuery(id+"F0.wireOp",EDGE,"E47"),sQuery(id+"F0.wireOp",EDGE,"E48"),sQuery(id+"F0.wireOp",EDGE,"E49"),sQuery(id+"F0.wireOp",EDGE,"E50"),sQuery(id+"F0.wireOp",EDGE,"E51"),sQuery(id+"F0.wireOp",EDGE,"E52"),sQuery(id+"F0.wireOp",EDGE,"E53"),sQuery(id+"F0.wireOp",EDGE,"E54"),sQuery(id+"F0.wireOp",EDGE,"E55"),sQuery(id+"F0.wireOp",EDGE,"E56"),sQuery(id+"F0.wireOp",EDGE,"E57"),sQuery(id+"F0.wireOp",EDGE,"E58"),sQuery(id+"F0.wireOp",EDGE,"E59"),sQuery(id+"F0.wireOp",EDGE,"E60"),sQuery(id+"F0.wireOp",EDGE,"E61"),sQuery(id+"F0.wireOp",EDGE,"E62"),sQuery(id+"F0.wireOp",EDGE,"E63"),sQuery(id+"F0.wireOp",EDGE,"E64"),sQuery(id+"F0.wireOp",EDGE,"E65"),sQuery(id+"F0.wireOp",EDGE,"E66"),sQuery(id+"F0.wireOp",EDGE,"E67"),sQuery(id+"F0.wireOp",EDGE,"E68"),sQuery(id+"F0.wireOp",EDGE,"E69"),sQuery(id+"F0.wireOp",EDGE,"E70"),sQuery(id+"F0.wireOp",EDGE,"E71"),sQuery(id+"F0.wireOp",EDGE,"E72"),sQuery(id+"F0.wireOp",EDGE,"E73"),sQuery(id+"F0.wireOp",EDGE,"E74"),sQuery(id+"F0.wireOp",EDGE,"E75"),sQuery(id+"F0.wireOp",EDGE,"E76"),sQuery(id+"F0.wireOp",EDGE,"E77"),sQuery(id+"F0.wireOp",EDGE,"E78"),sQuery(id+"F0.wireOp",EDGE,"E79"),sQuery(id+"F0.wireOp",EDGE,"E80"),sQuery(id+"F0.wireOp",EDGE,"E81"),sQuery(id+"F0.wireOp",EDGE,"E82"),sQuery(id+"F0.wireOp",EDGE,"E83"),sQuery(id+"F0.wireOp",EDGE,"E84"),sQuery(id+"F0.wireOp",EDGE,"E85"),sQuery(id+"F0.wireOp",EDGE,"E86"),sQuery(id+"F0.wireOp",EDGE,"E87"),sQuery(id+"F0.wireOp",EDGE,"E88"),sQuery(id+"F0.wireOp",EDGE,"E89"),sQuery(id+"F0.wireOp",EDGE,"E90"),sQuery(id+"F0.wireOp",EDGE,"E91"),sQuery(id+"F0.wireOp",EDGE,"E92"),sQuery(id+"F0.wireOp",EDGE,"E93"),sQuery(id+"F0.wireOp",EDGE,"E94"),sQuery(id+"F0.wireOp",EDGE,"E95"),sQuery(id+"F0.wireOp",EDGE,"E96"),sQuery(id+"F0.wireOp",EDGE,"E97"),sQuery(id+"F0.wireOp",EDGE,"E98"),sQuery(id+"F0.wireOp",EDGE,"E99"),sQuery(id+"F0.wireOp",EDGE,"E100"),sQuery(id+"F0.wireOp",EDGE,"E101"),sQuery(id+"F0.wireOp",EDGE,"E102"),sQuery(id+"F0.wireOp",EDGE,"E103"),sQuery(id+"F0.wireOp",EDGE,"E104")])]}),"instanceName":"42"});
            var Q10;
            Q10=makeQuery(id+"F2.opPattern","COPY",BODY,{"derivedFrom":makeQuery(id+"F1.opExtrude","SWEPT_BODY",BODY,{"disambiguationData":[OSD([sQuery(id+"F0.wireOp",EDGE,"E1"),sQuery(id+"F0.wireOp",EDGE,"E2"),sQuery(id+"F0.wireOp",EDGE,"E3"),sQuery(id+"F0.wireOp",EDGE,"E4"),sQuery(id+"F0.wireOp",EDGE,"E5"),sQuery(id+"F0.wireOp",EDGE,"E6"),sQuery(id+"F0.wireOp",EDGE,"E7"),sQuery(id+"F0.wireOp",EDGE,"E8"),sQuery(id+"F0.wireOp",EDGE,"E9"),sQuery(id+"F0.wireOp",EDGE,"E10"),sQuery(id+"F0.wireOp",EDGE,"E11"),sQuery(id+"F0.wireOp",EDGE,"E12"),sQuery(id+"F0.wireOp",EDGE,"E13"),sQuery(id+"F0.wireOp",EDGE,"E14"),sQuery(id+"F0.wireOp",EDGE,"E15"),sQuery(id+"F0.wireOp",EDGE,"E16"),sQuery(id+"F0.wireOp",EDGE,"E17"),sQuery(id+"F0.wireOp",EDGE,"E18"),sQuery(id+"F0.wireOp",EDGE,"E19"),sQuery(id+"F0.wireOp",EDGE,"E20"),sQuery(id+"F0.wireOp",EDGE,"E21"),sQuery(id+"F0.wireOp",EDGE,"E22"),sQuery(id+"F0.wireOp",EDGE,"E23"),sQuery(id+"F0.wireOp",EDGE,"E24"),sQuery(id+"F0.wireOp",EDGE,"E25"),sQuery(id+"F0.wireOp",EDGE,"E26"),sQuery(id+"F0.wireOp",EDGE,"E27"),sQuery(id+"F0.wireOp",EDGE,"E28"),sQuery(id+"F0.wireOp",EDGE,"E29"),sQuery(id+"F0.wireOp",EDGE,"E30"),sQuery(id+"F0.wireOp",EDGE,"E31"),sQuery(id+"F0.wireOp",EDGE,"E32"),sQuery(id+"F0.wireOp",EDGE,"E33"),sQuery(id+"F0.wireOp",EDGE,"E34"),sQuery(id+"F0.wireOp",EDGE,"E35"),sQuery(id+"F0.wireOp",EDGE,"E36"),sQuery(id+"F0.wireOp",EDGE,"E37"),sQuery(id+"F0.wireOp",EDGE,"E38"),sQuery(id+"F0.wireOp",EDGE,"E39"),sQuery(id+"F0.wireOp",EDGE,"E40"),sQuery(id+"F0.wireOp",EDGE,"E41"),sQuery(id+"F0.wireOp",EDGE,"E42"),sQuery(id+"F0.wireOp",EDGE,"E43"),sQuery(id+"F0.wireOp",EDGE,"E44"),sQuery(id+"F0.wireOp",EDGE,"E45"),sQuery(id+"F0.wireOp",EDGE,"E46"),sQuery(id+"F0.wireOp",EDGE,"E47"),sQuery(id+"F0.wireOp",EDGE,"E48"),sQuery(id+"F0.wireOp",EDGE,"E49"),sQuery(id+"F0.wireOp",EDGE,"E50"),sQuery(id+"F0.wireOp",EDGE,"E51"),sQuery(id+"F0.wireOp",EDGE,"E52"),sQuery(id+"F0.wireOp",EDGE,"E53"),sQuery(id+"F0.wireOp",EDGE,"E54"),sQuery(id+"F0.wireOp",EDGE,"E55"),sQuery(id+"F0.wireOp",EDGE,"E56"),sQuery(id+"F0.wireOp",EDGE,"E57"),sQuery(id+"F0.wireOp",EDGE,"E58"),sQuery(id+"F0.wireOp",EDGE,"E59"),sQuery(id+"F0.wireOp",EDGE,"E60"),sQuery(id+"F0.wireOp",EDGE,"E61"),sQuery(id+"F0.wireOp",EDGE,"E62"),sQuery(id+"F0.wireOp",EDGE,"E63"),sQuery(id+"F0.wireOp",EDGE,"E64"),sQuery(id+"F0.wireOp",EDGE,"E65"),sQuery(id+"F0.wireOp",EDGE,"E66"),sQuery(id+"F0.wireOp",EDGE,"E67"),sQuery(id+"F0.wireOp",EDGE,"E68"),sQuery(id+"F0.wireOp",EDGE,"E69"),sQuery(id+"F0.wireOp",EDGE,"E70"),sQuery(id+"F0.wireOp",EDGE,"E71"),sQuery(id+"F0.wireOp",EDGE,"E72"),sQuery(id+"F0.wireOp",EDGE,"E73"),sQuery(id+"F0.wireOp",EDGE,"E74"),sQuery(id+"F0.wireOp",EDGE,"E75"),sQuery(id+"F0.wireOp",EDGE,"E76"),sQuery(id+"F0.wireOp",EDGE,"E77"),sQuery(id+"F0.wireOp",EDGE,"E78"),sQuery(id+"F0.wireOp",EDGE,"E79"),sQuery(id+"F0.wireOp",EDGE,"E80"),sQuery(id+"F0.wireOp",EDGE,"E81"),sQuery(id+"F0.wireOp",EDGE,"E82"),sQuery(id+"F0.wireOp",EDGE,"E83"),sQuery(id+"F0.wireOp",EDGE,"E84"),sQuery(id+"F0.wireOp",EDGE,"E85"),sQuery(id+"F0.wireOp",EDGE,"E86"),sQuery(id+"F0.wireOp",EDGE,"E87"),sQuery(id+"F0.wireOp",EDGE,"E88"),sQuery(id+"F0.wireOp",EDGE,"E89"),sQuery(id+"F0.wireOp",EDGE,"E90"),sQuery(id+"F0.wireOp",EDGE,"E91"),sQuery(id+"F0.wireOp",EDGE,"E92"),sQuery(id+"F0.wireOp",EDGE,"E93"),sQuery(id+"F0.wireOp",EDGE,"E94"),sQuery(id+"F0.wireOp",EDGE,"E95"),sQuery(id+"F0.wireOp",EDGE,"E96"),sQuery(id+"F0.wireOp",EDGE,"E97"),sQuery(id+"F0.wireOp",EDGE,"E98"),sQuery(id+"F0.wireOp",EDGE,"E99"),sQuery(id+"F0.wireOp",EDGE,"E100"),sQuery(id+"F0.wireOp",EDGE,"E101"),sQuery(id+"F0.wireOp",EDGE,"E102"),sQuery(id+"F0.wireOp",EDGE,"E103"),sQuery(id+"F0.wireOp",EDGE,"E104")])]}),"instanceName":"43"});
            var Q11;
            Q11=makeQuery(id+"F2.opPattern","COPY",BODY,{"derivedFrom":makeQuery(id+"F1.opExtrude","SWEPT_BODY",BODY,{"disambiguationData":[OSD([sQuery(id+"F0.wireOp",EDGE,"E1"),sQuery(id+"F0.wireOp",EDGE,"E2"),sQuery(id+"F0.wireOp",EDGE,"E3"),sQuery(id+"F0.wireOp",EDGE,"E4"),sQuery(id+"F0.wireOp",EDGE,"E5"),sQuery(id+"F0.wireOp",EDGE,"E6"),sQuery(id+"F0.wireOp",EDGE,"E7"),sQuery(id+"F0.wireOp",EDGE,"E8"),sQuery(id+"F0.wireOp",EDGE,"E9"),sQuery(id+"F0.wireOp",EDGE,"E10"),sQuery(id+"F0.wireOp",EDGE,"E11"),sQuery(id+"F0.wireOp",EDGE,"E12"),sQuery(id+"F0.wireOp",EDGE,"E13"),sQuery(id+"F0.wireOp",EDGE,"E14"),sQuery(id+"F0.wireOp",EDGE,"E15"),sQuery(id+"F0.wireOp",EDGE,"E16"),sQuery(id+"F0.wireOp",EDGE,"E17"),sQuery(id+"F0.wireOp",EDGE,"E18"),sQuery(id+"F0.wireOp",EDGE,"E19"),sQuery(id+"F0.wireOp",EDGE,"E20"),sQuery(id+"F0.wireOp",EDGE,"E21"),sQuery(id+"F0.wireOp",EDGE,"E22"),sQuery(id+"F0.wireOp",EDGE,"E23"),sQuery(id+"F0.wireOp",EDGE,"E24"),sQuery(id+"F0.wireOp",EDGE,"E25"),sQuery(id+"F0.wireOp",EDGE,"E26"),sQuery(id+"F0.wireOp",EDGE,"E27"),sQuery(id+"F0.wireOp",EDGE,"E28"),sQuery(id+"F0.wireOp",EDGE,"E29"),sQuery(id+"F0.wireOp",EDGE,"E30"),sQuery(id+"F0.wireOp",EDGE,"E31"),sQuery(id+"F0.wireOp",EDGE,"E32"),sQuery(id+"F0.wireOp",EDGE,"E33"),sQuery(id+"F0.wireOp",EDGE,"E34"),sQuery(id+"F0.wireOp",EDGE,"E35"),sQuery(id+"F0.wireOp",EDGE,"E36"),sQuery(id+"F0.wireOp",EDGE,"E37"),sQuery(id+"F0.wireOp",EDGE,"E38"),sQuery(id+"F0.wireOp",EDGE,"E39"),sQuery(id+"F0.wireOp",EDGE,"E40"),sQuery(id+"F0.wireOp",EDGE,"E41"),sQuery(id+"F0.wireOp",EDGE,"E42"),sQuery(id+"F0.wireOp",EDGE,"E43"),sQuery(id+"F0.wireOp",EDGE,"E44"),sQuery(id+"F0.wireOp",EDGE,"E45"),sQuery(id+"F0.wireOp",EDGE,"E46"),sQuery(id+"F0.wireOp",EDGE,"E47"),sQuery(id+"F0.wireOp",EDGE,"E48"),sQuery(id+"F0.wireOp",EDGE,"E49"),sQuery(id+"F0.wireOp",EDGE,"E50"),sQuery(id+"F0.wireOp",EDGE,"E51"),sQuery(id+"F0.wireOp",EDGE,"E52"),sQuery(id+"F0.wireOp",EDGE,"E53"),sQuery(id+"F0.wireOp",EDGE,"E54"),sQuery(id+"F0.wireOp",EDGE,"E55"),sQuery(id+"F0.wireOp",EDGE,"E56"),sQuery(id+"F0.wireOp",EDGE,"E57"),sQuery(id+"F0.wireOp",EDGE,"E58"),sQuery(id+"F0.wireOp",EDGE,"E59"),sQuery(id+"F0.wireOp",EDGE,"E60"),sQuery(id+"F0.wireOp",EDGE,"E61"),sQuery(id+"F0.wireOp",EDGE,"E62"),sQuery(id+"F0.wireOp",EDGE,"E63"),sQuery(id+"F0.wireOp",EDGE,"E64"),sQuery(id+"F0.wireOp",EDGE,"E65"),sQuery(id+"F0.wireOp",EDGE,"E66"),sQuery(id+"F0.wireOp",EDGE,"E67"),sQuery(id+"F0.wireOp",EDGE,"E68"),sQuery(id+"F0.wireOp",EDGE,"E69"),sQuery(id+"F0.wireOp",EDGE,"E70"),sQuery(id+"F0.wireOp",EDGE,"E71"),sQuery(id+"F0.wireOp",EDGE,"E72"),sQuery(id+"F0.wireOp",EDGE,"E73"),sQuery(id+"F0.wireOp",EDGE,"E74"),sQuery(id+"F0.wireOp",EDGE,"E75"),sQuery(id+"F0.wireOp",EDGE,"E76"),sQuery(id+"F0.wireOp",EDGE,"E77"),sQuery(id+"F0.wireOp",EDGE,"E78"),sQuery(id+"F0.wireOp",EDGE,"E79"),sQuery(id+"F0.wireOp",EDGE,"E80"),sQuery(id+"F0.wireOp",EDGE,"E81"),sQuery(id+"F0.wireOp",EDGE,"E82"),sQuery(id+"F0.wireOp",EDGE,"E83"),sQuery(id+"F0.wireOp",EDGE,"E84"),sQuery(id+"F0.wireOp",EDGE,"E85"),sQuery(id+"F0.wireOp",EDGE,"E86"),sQuery(id+"F0.wireOp",EDGE,"E87"),sQuery(id+"F0.wireOp",EDGE,"E88"),sQuery(id+"F0.wireOp",EDGE,"E89"),sQuery(id+"F0.wireOp",EDGE,"E90"),sQuery(id+"F0.wireOp",EDGE,"E91"),sQuery(id+"F0.wireOp",EDGE,"E92"),sQuery(id+"F0.wireOp",EDGE,"E93"),sQuery(id+"F0.wireOp",EDGE,"E94"),sQuery(id+"F0.wireOp",EDGE,"E95"),sQuery(id+"F0.wireOp",EDGE,"E96"),sQuery(id+"F0.wireOp",EDGE,"E97"),sQuery(id+"F0.wireOp",EDGE,"E98"),sQuery(id+"F0.wireOp",EDGE,"E99"),sQuery(id+"F0.wireOp",EDGE,"E100"),sQuery(id+"F0.wireOp",EDGE,"E101"),sQuery(id+"F0.wireOp",EDGE,"E102"),sQuery(id+"F0.wireOp",EDGE,"E103"),sQuery(id+"F0.wireOp",EDGE,"E104")])]}),"instanceName":"44"});
            var Q12;
            Q12=makeQuery(id+"F2.opPattern","COPY",BODY,{"derivedFrom":makeQuery(id+"F1.opExtrude","SWEPT_BODY",BODY,{"disambiguationData":[OSD([sQuery(id+"F0.wireOp",EDGE,"E1"),sQuery(id+"F0.wireOp",EDGE,"E2"),sQuery(id+"F0.wireOp",EDGE,"E3"),sQuery(id+"F0.wireOp",EDGE,"E4"),sQuery(id+"F0.wireOp",EDGE,"E5"),sQuery(id+"F0.wireOp",EDGE,"E6"),sQuery(id+"F0.wireOp",EDGE,"E7"),sQuery(id+"F0.wireOp",EDGE,"E8"),sQuery(id+"F0.wireOp",EDGE,"E9"),sQuery(id+"F0.wireOp",EDGE,"E10"),sQuery(id+"F0.wireOp",EDGE,"E11"),sQuery(id+"F0.wireOp",EDGE,"E12"),sQuery(id+"F0.wireOp",EDGE,"E13"),sQuery(id+"F0.wireOp",EDGE,"E14"),sQuery(id+"F0.wireOp",EDGE,"E15"),sQuery(id+"F0.wireOp",EDGE,"E16"),sQuery(id+"F0.wireOp",EDGE,"E17"),sQuery(id+"F0.wireOp",EDGE,"E18"),sQuery(id+"F0.wireOp",EDGE,"E19"),sQuery(id+"F0.wireOp",EDGE,"E20"),sQuery(id+"F0.wireOp",EDGE,"E21"),sQuery(id+"F0.wireOp",EDGE,"E22"),sQuery(id+"F0.wireOp",EDGE,"E23"),sQuery(id+"F0.wireOp",EDGE,"E24"),sQuery(id+"F0.wireOp",EDGE,"E25"),sQuery(id+"F0.wireOp",EDGE,"E26"),sQuery(id+"F0.wireOp",EDGE,"E27"),sQuery(id+"F0.wireOp",EDGE,"E28"),sQuery(id+"F0.wireOp",EDGE,"E29"),sQuery(id+"F0.wireOp",EDGE,"E30"),sQuery(id+"F0.wireOp",EDGE,"E31"),sQuery(id+"F0.wireOp",EDGE,"E32"),sQuery(id+"F0.wireOp",EDGE,"E33"),sQuery(id+"F0.wireOp",EDGE,"E34"),sQuery(id+"F0.wireOp",EDGE,"E35"),sQuery(id+"F0.wireOp",EDGE,"E36"),sQuery(id+"F0.wireOp",EDGE,"E37"),sQuery(id+"F0.wireOp",EDGE,"E38"),sQuery(id+"F0.wireOp",EDGE,"E39"),sQuery(id+"F0.wireOp",EDGE,"E40"),sQuery(id+"F0.wireOp",EDGE,"E41"),sQuery(id+"F0.wireOp",EDGE,"E42"),sQuery(id+"F0.wireOp",EDGE,"E43"),sQuery(id+"F0.wireOp",EDGE,"E44"),sQuery(id+"F0.wireOp",EDGE,"E45"),sQuery(id+"F0.wireOp",EDGE,"E46"),sQuery(id+"F0.wireOp",EDGE,"E47"),sQuery(id+"F0.wireOp",EDGE,"E48"),sQuery(id+"F0.wireOp",EDGE,"E49"),sQuery(id+"F0.wireOp",EDGE,"E50"),sQuery(id+"F0.wireOp",EDGE,"E51"),sQuery(id+"F0.wireOp",EDGE,"E52"),sQuery(id+"F0.wireOp",EDGE,"E53"),sQuery(id+"F0.wireOp",EDGE,"E54"),sQuery(id+"F0.wireOp",EDGE,"E55"),sQuery(id+"F0.wireOp",EDGE,"E56"),sQuery(id+"F0.wireOp",EDGE,"E57"),sQuery(id+"F0.wireOp",EDGE,"E58"),sQuery(id+"F0.wireOp",EDGE,"E59"),sQuery(id+"F0.wireOp",EDGE,"E60"),sQuery(id+"F0.wireOp",EDGE,"E61"),sQuery(id+"F0.wireOp",EDGE,"E62"),sQuery(id+"F0.wireOp",EDGE,"E63"),sQuery(id+"F0.wireOp",EDGE,"E64"),sQuery(id+"F0.wireOp",EDGE,"E65"),sQuery(id+"F0.wireOp",EDGE,"E66"),sQuery(id+"F0.wireOp",EDGE,"E67"),sQuery(id+"F0.wireOp",EDGE,"E68"),sQuery(id+"F0.wireOp",EDGE,"E69"),sQuery(id+"F0.wireOp",EDGE,"E70"),sQuery(id+"F0.wireOp",EDGE,"E71"),sQuery(id+"F0.wireOp",EDGE,"E72"),sQuery(id+"F0.wireOp",EDGE,"E73"),sQuery(id+"F0.wireOp",EDGE,"E74"),sQuery(id+"F0.wireOp",EDGE,"E75"),sQuery(id+"F0.wireOp",EDGE,"E76"),sQuery(id+"F0.wireOp",EDGE,"E77"),sQuery(id+"F0.wireOp",EDGE,"E78"),sQuery(id+"F0.wireOp",EDGE,"E79"),sQuery(id+"F0.wireOp",EDGE,"E80"),sQuery(id+"F0.wireOp",EDGE,"E81"),sQuery(id+"F0.wireOp",EDGE,"E82"),sQuery(id+"F0.wireOp",EDGE,"E83"),sQuery(id+"F0.wireOp",EDGE,"E84"),sQuery(id+"F0.wireOp",EDGE,"E85"),sQuery(id+"F0.wireOp",EDGE,"E86"),sQuery(id+"F0.wireOp",EDGE,"E87"),sQuery(id+"F0.wireOp",EDGE,"E88"),sQuery(id+"F0.wireOp",EDGE,"E89"),sQuery(id+"F0.wireOp",EDGE,"E90"),sQuery(id+"F0.wireOp",EDGE,"E91"),sQuery(id+"F0.wireOp",EDGE,"E92"),sQuery(id+"F0.wireOp",EDGE,"E93"),sQuery(id+"F0.wireOp",EDGE,"E94"),sQuery(id+"F0.wireOp",EDGE,"E95"),sQuery(id+"F0.wireOp",EDGE,"E96"),sQuery(id+"F0.wireOp",EDGE,"E97"),sQuery(id+"F0.wireOp",EDGE,"E98"),sQuery(id+"F0.wireOp",EDGE,"E99"),sQuery(id+"F0.wireOp",EDGE,"E100"),sQuery(id+"F0.wireOp",EDGE,"E101"),sQuery(id+"F0.wireOp",EDGE,"E102"),sQuery(id+"F0.wireOp",EDGE,"E103"),sQuery(id+"F0.wireOp",EDGE,"E104")])]}),"instanceName":"45"});
            var Q13;
            Q13=makeQuery(id+"F2.opPattern","COPY",BODY,{"derivedFrom":makeQuery(id+"F1.opExtrude","SWEPT_BODY",BODY,{"disambiguationData":[OSD([sQuery(id+"F0.wireOp",EDGE,"E1"),sQuery(id+"F0.wireOp",EDGE,"E2"),sQuery(id+"F0.wireOp",EDGE,"E3"),sQuery(id+"F0.wireOp",EDGE,"E4"),sQuery(id+"F0.wireOp",EDGE,"E5"),sQuery(id+"F0.wireOp",EDGE,"E6"),sQuery(id+"F0.wireOp",EDGE,"E7"),sQuery(id+"F0.wireOp",EDGE,"E8"),sQuery(id+"F0.wireOp",EDGE,"E9"),sQuery(id+"F0.wireOp",EDGE,"E10"),sQuery(id+"F0.wireOp",EDGE,"E11"),sQuery(id+"F0.wireOp",EDGE,"E12"),sQuery(id+"F0.wireOp",EDGE,"E13"),sQuery(id+"F0.wireOp",EDGE,"E14"),sQuery(id+"F0.wireOp",EDGE,"E15"),sQuery(id+"F0.wireOp",EDGE,"E16"),sQuery(id+"F0.wireOp",EDGE,"E17"),sQuery(id+"F0.wireOp",EDGE,"E18"),sQuery(id+"F0.wireOp",EDGE,"E19"),sQuery(id+"F0.wireOp",EDGE,"E20"),sQuery(id+"F0.wireOp",EDGE,"E21"),sQuery(id+"F0.wireOp",EDGE,"E22"),sQuery(id+"F0.wireOp",EDGE,"E23"),sQuery(id+"F0.wireOp",EDGE,"E24"),sQuery(id+"F0.wireOp",EDGE,"E25"),sQuery(id+"F0.wireOp",EDGE,"E26"),sQuery(id+"F0.wireOp",EDGE,"E27"),sQuery(id+"F0.wireOp",EDGE,"E28"),sQuery(id+"F0.wireOp",EDGE,"E29"),sQuery(id+"F0.wireOp",EDGE,"E30"),sQuery(id+"F0.wireOp",EDGE,"E31"),sQuery(id+"F0.wireOp",EDGE,"E32"),sQuery(id+"F0.wireOp",EDGE,"E33"),sQuery(id+"F0.wireOp",EDGE,"E34"),sQuery(id+"F0.wireOp",EDGE,"E35"),sQuery(id+"F0.wireOp",EDGE,"E36"),sQuery(id+"F0.wireOp",EDGE,"E37"),sQuery(id+"F0.wireOp",EDGE,"E38"),sQuery(id+"F0.wireOp",EDGE,"E39"),sQuery(id+"F0.wireOp",EDGE,"E40"),sQuery(id+"F0.wireOp",EDGE,"E41"),sQuery(id+"F0.wireOp",EDGE,"E42"),sQuery(id+"F0.wireOp",EDGE,"E43"),sQuery(id+"F0.wireOp",EDGE,"E44"),sQuery(id+"F0.wireOp",EDGE,"E45"),sQuery(id+"F0.wireOp",EDGE,"E46"),sQuery(id+"F0.wireOp",EDGE,"E47"),sQuery(id+"F0.wireOp",EDGE,"E48"),sQuery(id+"F0.wireOp",EDGE,"E49"),sQuery(id+"F0.wireOp",EDGE,"E50"),sQuery(id+"F0.wireOp",EDGE,"E51"),sQuery(id+"F0.wireOp",EDGE,"E52"),sQuery(id+"F0.wireOp",EDGE,"E53"),sQuery(id+"F0.wireOp",EDGE,"E54"),sQuery(id+"F0.wireOp",EDGE,"E55"),sQuery(id+"F0.wireOp",EDGE,"E56"),sQuery(id+"F0.wireOp",EDGE,"E57"),sQuery(id+"F0.wireOp",EDGE,"E58"),sQuery(id+"F0.wireOp",EDGE,"E59"),sQuery(id+"F0.wireOp",EDGE,"E60"),sQuery(id+"F0.wireOp",EDGE,"E61"),sQuery(id+"F0.wireOp",EDGE,"E62"),sQuery(id+"F0.wireOp",EDGE,"E63"),sQuery(id+"F0.wireOp",EDGE,"E64"),sQuery(id+"F0.wireOp",EDGE,"E65"),sQuery(id+"F0.wireOp",EDGE,"E66"),sQuery(id+"F0.wireOp",EDGE,"E67"),sQuery(id+"F0.wireOp",EDGE,"E68"),sQuery(id+"F0.wireOp",EDGE,"E69"),sQuery(id+"F0.wireOp",EDGE,"E70"),sQuery(id+"F0.wireOp",EDGE,"E71"),sQuery(id+"F0.wireOp",EDGE,"E72"),sQuery(id+"F0.wireOp",EDGE,"E73"),sQuery(id+"F0.wireOp",EDGE,"E74"),sQuery(id+"F0.wireOp",EDGE,"E75"),sQuery(id+"F0.wireOp",EDGE,"E76"),sQuery(id+"F0.wireOp",EDGE,"E77"),sQuery(id+"F0.wireOp",EDGE,"E78"),sQuery(id+"F0.wireOp",EDGE,"E79"),sQuery(id+"F0.wireOp",EDGE,"E80"),sQuery(id+"F0.wireOp",EDGE,"E81"),sQuery(id+"F0.wireOp",EDGE,"E82"),sQuery(id+"F0.wireOp",EDGE,"E83"),sQuery(id+"F0.wireOp",EDGE,"E84"),sQuery(id+"F0.wireOp",EDGE,"E85"),sQuery(id+"F0.wireOp",EDGE,"E86"),sQuery(id+"F0.wireOp",EDGE,"E87"),sQuery(id+"F0.wireOp",EDGE,"E88"),sQuery(id+"F0.wireOp",EDGE,"E89"),sQuery(id+"F0.wireOp",EDGE,"E90"),sQuery(id+"F0.wireOp",EDGE,"E91"),sQuery(id+"F0.wireOp",EDGE,"E92"),sQuery(id+"F0.wireOp",EDGE,"E93"),sQuery(id+"F0.wireOp",EDGE,"E94"),sQuery(id+"F0.wireOp",EDGE,"E95"),sQuery(id+"F0.wireOp",EDGE,"E96"),sQuery(id+"F0.wireOp",EDGE,"E97"),sQuery(id+"F0.wireOp",EDGE,"E98"),sQuery(id+"F0.wireOp",EDGE,"E99"),sQuery(id+"F0.wireOp",EDGE,"E100"),sQuery(id+"F0.wireOp",EDGE,"E101"),sQuery(id+"F0.wireOp",EDGE,"E102"),sQuery(id+"F0.wireOp",EDGE,"E103"),sQuery(id+"F0.wireOp",EDGE,"E104")])]}),"instanceName":"46"});
            var Q14;
            Q14=makeQuery(id+"F2.opPattern","COPY",BODY,{"derivedFrom":makeQuery(id+"F1.opExtrude","SWEPT_BODY",BODY,{"disambiguationData":[OSD([sQuery(id+"F0.wireOp",EDGE,"E1"),sQuery(id+"F0.wireOp",EDGE,"E2"),sQuery(id+"F0.wireOp",EDGE,"E3"),sQuery(id+"F0.wireOp",EDGE,"E4"),sQuery(id+"F0.wireOp",EDGE,"E5"),sQuery(id+"F0.wireOp",EDGE,"E6"),sQuery(id+"F0.wireOp",EDGE,"E7"),sQuery(id+"F0.wireOp",EDGE,"E8"),sQuery(id+"F0.wireOp",EDGE,"E9"),sQuery(id+"F0.wireOp",EDGE,"E10"),sQuery(id+"F0.wireOp",EDGE,"E11"),sQuery(id+"F0.wireOp",EDGE,"E12"),sQuery(id+"F0.wireOp",EDGE,"E13"),sQuery(id+"F0.wireOp",EDGE,"E14"),sQuery(id+"F0.wireOp",EDGE,"E15"),sQuery(id+"F0.wireOp",EDGE,"E16"),sQuery(id+"F0.wireOp",EDGE,"E17"),sQuery(id+"F0.wireOp",EDGE,"E18"),sQuery(id+"F0.wireOp",EDGE,"E19"),sQuery(id+"F0.wireOp",EDGE,"E20"),sQuery(id+"F0.wireOp",EDGE,"E21"),sQuery(id+"F0.wireOp",EDGE,"E22"),sQuery(id+"F0.wireOp",EDGE,"E23"),sQuery(id+"F0.wireOp",EDGE,"E24"),sQuery(id+"F0.wireOp",EDGE,"E25"),sQuery(id+"F0.wireOp",EDGE,"E26"),sQuery(id+"F0.wireOp",EDGE,"E27"),sQuery(id+"F0.wireOp",EDGE,"E28"),sQuery(id+"F0.wireOp",EDGE,"E29"),sQuery(id+"F0.wireOp",EDGE,"E30"),sQuery(id+"F0.wireOp",EDGE,"E31"),sQuery(id+"F0.wireOp",EDGE,"E32"),sQuery(id+"F0.wireOp",EDGE,"E33"),sQuery(id+"F0.wireOp",EDGE,"E34"),sQuery(id+"F0.wireOp",EDGE,"E35"),sQuery(id+"F0.wireOp",EDGE,"E36"),sQuery(id+"F0.wireOp",EDGE,"E37"),sQuery(id+"F0.wireOp",EDGE,"E38"),sQuery(id+"F0.wireOp",EDGE,"E39"),sQuery(id+"F0.wireOp",EDGE,"E40"),sQuery(id+"F0.wireOp",EDGE,"E41"),sQuery(id+"F0.wireOp",EDGE,"E42"),sQuery(id+"F0.wireOp",EDGE,"E43"),sQuery(id+"F0.wireOp",EDGE,"E44"),sQuery(id+"F0.wireOp",EDGE,"E45"),sQuery(id+"F0.wireOp",EDGE,"E46"),sQuery(id+"F0.wireOp",EDGE,"E47"),sQuery(id+"F0.wireOp",EDGE,"E48"),sQuery(id+"F0.wireOp",EDGE,"E49"),sQuery(id+"F0.wireOp",EDGE,"E50"),sQuery(id+"F0.wireOp",EDGE,"E51"),sQuery(id+"F0.wireOp",EDGE,"E52"),sQuery(id+"F0.wireOp",EDGE,"E53"),sQuery(id+"F0.wireOp",EDGE,"E54"),sQuery(id+"F0.wireOp",EDGE,"E55"),sQuery(id+"F0.wireOp",EDGE,"E56"),sQuery(id+"F0.wireOp",EDGE,"E57"),sQuery(id+"F0.wireOp",EDGE,"E58"),sQuery(id+"F0.wireOp",EDGE,"E59"),sQuery(id+"F0.wireOp",EDGE,"E60"),sQuery(id+"F0.wireOp",EDGE,"E61"),sQuery(id+"F0.wireOp",EDGE,"E62"),sQuery(id+"F0.wireOp",EDGE,"E63"),sQuery(id+"F0.wireOp",EDGE,"E64"),sQuery(id+"F0.wireOp",EDGE,"E65"),sQuery(id+"F0.wireOp",EDGE,"E66"),sQuery(id+"F0.wireOp",EDGE,"E67"),sQuery(id+"F0.wireOp",EDGE,"E68"),sQuery(id+"F0.wireOp",EDGE,"E69"),sQuery(id+"F0.wireOp",EDGE,"E70"),sQuery(id+"F0.wireOp",EDGE,"E71"),sQuery(id+"F0.wireOp",EDGE,"E72"),sQuery(id+"F0.wireOp",EDGE,"E73"),sQuery(id+"F0.wireOp",EDGE,"E74"),sQuery(id+"F0.wireOp",EDGE,"E75"),sQuery(id+"F0.wireOp",EDGE,"E76"),sQuery(id+"F0.wireOp",EDGE,"E77"),sQuery(id+"F0.wireOp",EDGE,"E78"),sQuery(id+"F0.wireOp",EDGE,"E79"),sQuery(id+"F0.wireOp",EDGE,"E80"),sQuery(id+"F0.wireOp",EDGE,"E81"),sQuery(id+"F0.wireOp",EDGE,"E82"),sQuery(id+"F0.wireOp",EDGE,"E83"),sQuery(id+"F0.wireOp",EDGE,"E84"),sQuery(id+"F0.wireOp",EDGE,"E85"),sQuery(id+"F0.wireOp",EDGE,"E86"),sQuery(id+"F0.wireOp",EDGE,"E87"),sQuery(id+"F0.wireOp",EDGE,"E88"),sQuery(id+"F0.wireOp",EDGE,"E89"),sQuery(id+"F0.wireOp",EDGE,"E90"),sQuery(id+"F0.wireOp",EDGE,"E91"),sQuery(id+"F0.wireOp",EDGE,"E92"),sQuery(id+"F0.wireOp",EDGE,"E93"),sQuery(id+"F0.wireOp",EDGE,"E94"),sQuery(id+"F0.wireOp",EDGE,"E95"),sQuery(id+"F0.wireOp",EDGE,"E96"),sQuery(id+"F0.wireOp",EDGE,"E97"),sQuery(id+"F0.wireOp",EDGE,"E98"),sQuery(id+"F0.wireOp",EDGE,"E99"),sQuery(id+"F0.wireOp",EDGE,"E100"),sQuery(id+"F0.wireOp",EDGE,"E101"),sQuery(id+"F0.wireOp",EDGE,"E102"),sQuery(id+"F0.wireOp",EDGE,"E103"),sQuery(id+"F0.wireOp",EDGE,"E104")])]}),"instanceName":"47"});
            var Q15;
            Q15=makeQuery(id+"F2.opPattern","COPY",BODY,{"derivedFrom":makeQuery(id+"F1.opExtrude","SWEPT_BODY",BODY,{"disambiguationData":[OSD([sQuery(id+"F0.wireOp",EDGE,"E1"),sQuery(id+"F0.wireOp",EDGE,"E2"),sQuery(id+"F0.wireOp",EDGE,"E3"),sQuery(id+"F0.wireOp",EDGE,"E4"),sQuery(id+"F0.wireOp",EDGE,"E5"),sQuery(id+"F0.wireOp",EDGE,"E6"),sQuery(id+"F0.wireOp",EDGE,"E7"),sQuery(id+"F0.wireOp",EDGE,"E8"),sQuery(id+"F0.wireOp",EDGE,"E9"),sQuery(id+"F0.wireOp",EDGE,"E10"),sQuery(id+"F0.wireOp",EDGE,"E11"),sQuery(id+"F0.wireOp",EDGE,"E12"),sQuery(id+"F0.wireOp",EDGE,"E13"),sQuery(id+"F0.wireOp",EDGE,"E14"),sQuery(id+"F0.wireOp",EDGE,"E15"),sQuery(id+"F0.wireOp",EDGE,"E16"),sQuery(id+"F0.wireOp",EDGE,"E17"),sQuery(id+"F0.wireOp",EDGE,"E18"),sQuery(id+"F0.wireOp",EDGE,"E19"),sQuery(id+"F0.wireOp",EDGE,"E20"),sQuery(id+"F0.wireOp",EDGE,"E21"),sQuery(id+"F0.wireOp",EDGE,"E22"),sQuery(id+"F0.wireOp",EDGE,"E23"),sQuery(id+"F0.wireOp",EDGE,"E24"),sQuery(id+"F0.wireOp",EDGE,"E25"),sQuery(id+"F0.wireOp",EDGE,"E26"),sQuery(id+"F0.wireOp",EDGE,"E27"),sQuery(id+"F0.wireOp",EDGE,"E28"),sQuery(id+"F0.wireOp",EDGE,"E29"),sQuery(id+"F0.wireOp",EDGE,"E30"),sQuery(id+"F0.wireOp",EDGE,"E31"),sQuery(id+"F0.wireOp",EDGE,"E32"),sQuery(id+"F0.wireOp",EDGE,"E33"),sQuery(id+"F0.wireOp",EDGE,"E34"),sQuery(id+"F0.wireOp",EDGE,"E35"),sQuery(id+"F0.wireOp",EDGE,"E36"),sQuery(id+"F0.wireOp",EDGE,"E37"),sQuery(id+"F0.wireOp",EDGE,"E38"),sQuery(id+"F0.wireOp",EDGE,"E39"),sQuery(id+"F0.wireOp",EDGE,"E40"),sQuery(id+"F0.wireOp",EDGE,"E41"),sQuery(id+"F0.wireOp",EDGE,"E42"),sQuery(id+"F0.wireOp",EDGE,"E43"),sQuery(id+"F0.wireOp",EDGE,"E44"),sQuery(id+"F0.wireOp",EDGE,"E45"),sQuery(id+"F0.wireOp",EDGE,"E46"),sQuery(id+"F0.wireOp",EDGE,"E47"),sQuery(id+"F0.wireOp",EDGE,"E48"),sQuery(id+"F0.wireOp",EDGE,"E49"),sQuery(id+"F0.wireOp",EDGE,"E50"),sQuery(id+"F0.wireOp",EDGE,"E51"),sQuery(id+"F0.wireOp",EDGE,"E52"),sQuery(id+"F0.wireOp",EDGE,"E53"),sQuery(id+"F0.wireOp",EDGE,"E54"),sQuery(id+"F0.wireOp",EDGE,"E55"),sQuery(id+"F0.wireOp",EDGE,"E56"),sQuery(id+"F0.wireOp",EDGE,"E57"),sQuery(id+"F0.wireOp",EDGE,"E58"),sQuery(id+"F0.wireOp",EDGE,"E59"),sQuery(id+"F0.wireOp",EDGE,"E60"),sQuery(id+"F0.wireOp",EDGE,"E61"),sQuery(id+"F0.wireOp",EDGE,"E62"),sQuery(id+"F0.wireOp",EDGE,"E63"),sQuery(id+"F0.wireOp",EDGE,"E64"),sQuery(id+"F0.wireOp",EDGE,"E65"),sQuery(id+"F0.wireOp",EDGE,"E66"),sQuery(id+"F0.wireOp",EDGE,"E67"),sQuery(id+"F0.wireOp",EDGE,"E68"),sQuery(id+"F0.wireOp",EDGE,"E69"),sQuery(id+"F0.wireOp",EDGE,"E70"),sQuery(id+"F0.wireOp",EDGE,"E71"),sQuery(id+"F0.wireOp",EDGE,"E72"),sQuery(id+"F0.wireOp",EDGE,"E73"),sQuery(id+"F0.wireOp",EDGE,"E74"),sQuery(id+"F0.wireOp",EDGE,"E75"),sQuery(id+"F0.wireOp",EDGE,"E76"),sQuery(id+"F0.wireOp",EDGE,"E77"),sQuery(id+"F0.wireOp",EDGE,"E78"),sQuery(id+"F0.wireOp",EDGE,"E79"),sQuery(id+"F0.wireOp",EDGE,"E80"),sQuery(id+"F0.wireOp",EDGE,"E81"),sQuery(id+"F0.wireOp",EDGE,"E82"),sQuery(id+"F0.wireOp",EDGE,"E83"),sQuery(id+"F0.wireOp",EDGE,"E84"),sQuery(id+"F0.wireOp",EDGE,"E85"),sQuery(id+"F0.wireOp",EDGE,"E86"),sQuery(id+"F0.wireOp",EDGE,"E87"),sQuery(id+"F0.wireOp",EDGE,"E88"),sQuery(id+"F0.wireOp",EDGE,"E89"),sQuery(id+"F0.wireOp",EDGE,"E90"),sQuery(id+"F0.wireOp",EDGE,"E91"),sQuery(id+"F0.wireOp",EDGE,"E92"),sQuery(id+"F0.wireOp",EDGE,"E93"),sQuery(id+"F0.wireOp",EDGE,"E94"),sQuery(id+"F0.wireOp",EDGE,"E95"),sQuery(id+"F0.wireOp",EDGE,"E96"),sQuery(id+"F0.wireOp",EDGE,"E97"),sQuery(id+"F0.wireOp",EDGE,"E98"),sQuery(id+"F0.wireOp",EDGE,"E99"),sQuery(id+"F0.wireOp",EDGE,"E100"),sQuery(id+"F0.wireOp",EDGE,"E101"),sQuery(id+"F0.wireOp",EDGE,"E102"),sQuery(id+"F0.wireOp",EDGE,"E103"),sQuery(id+"F0.wireOp",EDGE,"E104")])]}),"instanceName":"48"});
            var Q16;
            Q16=makeQuery(id+"F2.opPattern","COPY",BODY,{"derivedFrom":makeQuery(id+"F1.opExtrude","SWEPT_BODY",BODY,{"disambiguationData":[OSD([sQuery(id+"F0.wireOp",EDGE,"E1"),sQuery(id+"F0.wireOp",EDGE,"E2"),sQuery(id+"F0.wireOp",EDGE,"E3"),sQuery(id+"F0.wireOp",EDGE,"E4"),sQuery(id+"F0.wireOp",EDGE,"E5"),sQuery(id+"F0.wireOp",EDGE,"E6"),sQuery(id+"F0.wireOp",EDGE,"E7"),sQuery(id+"F0.wireOp",EDGE,"E8"),sQuery(id+"F0.wireOp",EDGE,"E9"),sQuery(id+"F0.wireOp",EDGE,"E10"),sQuery(id+"F0.wireOp",EDGE,"E11"),sQuery(id+"F0.wireOp",EDGE,"E12"),sQuery(id+"F0.wireOp",EDGE,"E13"),sQuery(id+"F0.wireOp",EDGE,"E14"),sQuery(id+"F0.wireOp",EDGE,"E15"),sQuery(id+"F0.wireOp",EDGE,"E16"),sQuery(id+"F0.wireOp",EDGE,"E17"),sQuery(id+"F0.wireOp",EDGE,"E18"),sQuery(id+"F0.wireOp",EDGE,"E19"),sQuery(id+"F0.wireOp",EDGE,"E20"),sQuery(id+"F0.wireOp",EDGE,"E21"),sQuery(id+"F0.wireOp",EDGE,"E22"),sQuery(id+"F0.wireOp",EDGE,"E23"),sQuery(id+"F0.wireOp",EDGE,"E24"),sQuery(id+"F0.wireOp",EDGE,"E25"),sQuery(id+"F0.wireOp",EDGE,"E26"),sQuery(id+"F0.wireOp",EDGE,"E27"),sQuery(id+"F0.wireOp",EDGE,"E28"),sQuery(id+"F0.wireOp",EDGE,"E29"),sQuery(id+"F0.wireOp",EDGE,"E30"),sQuery(id+"F0.wireOp",EDGE,"E31"),sQuery(id+"F0.wireOp",EDGE,"E32"),sQuery(id+"F0.wireOp",EDGE,"E33"),sQuery(id+"F0.wireOp",EDGE,"E34"),sQuery(id+"F0.wireOp",EDGE,"E35"),sQuery(id+"F0.wireOp",EDGE,"E36"),sQuery(id+"F0.wireOp",EDGE,"E37"),sQuery(id+"F0.wireOp",EDGE,"E38"),sQuery(id+"F0.wireOp",EDGE,"E39"),sQuery(id+"F0.wireOp",EDGE,"E40"),sQuery(id+"F0.wireOp",EDGE,"E41"),sQuery(id+"F0.wireOp",EDGE,"E42"),sQuery(id+"F0.wireOp",EDGE,"E43"),sQuery(id+"F0.wireOp",EDGE,"E44"),sQuery(id+"F0.wireOp",EDGE,"E45"),sQuery(id+"F0.wireOp",EDGE,"E46"),sQuery(id+"F0.wireOp",EDGE,"E47"),sQuery(id+"F0.wireOp",EDGE,"E48"),sQuery(id+"F0.wireOp",EDGE,"E49"),sQuery(id+"F0.wireOp",EDGE,"E50"),sQuery(id+"F0.wireOp",EDGE,"E51"),sQuery(id+"F0.wireOp",EDGE,"E52"),sQuery(id+"F0.wireOp",EDGE,"E53"),sQuery(id+"F0.wireOp",EDGE,"E54"),sQuery(id+"F0.wireOp",EDGE,"E55"),sQuery(id+"F0.wireOp",EDGE,"E56"),sQuery(id+"F0.wireOp",EDGE,"E57"),sQuery(id+"F0.wireOp",EDGE,"E58"),sQuery(id+"F0.wireOp",EDGE,"E59"),sQuery(id+"F0.wireOp",EDGE,"E60"),sQuery(id+"F0.wireOp",EDGE,"E61"),sQuery(id+"F0.wireOp",EDGE,"E62"),sQuery(id+"F0.wireOp",EDGE,"E63"),sQuery(id+"F0.wireOp",EDGE,"E64"),sQuery(id+"F0.wireOp",EDGE,"E65"),sQuery(id+"F0.wireOp",EDGE,"E66"),sQuery(id+"F0.wireOp",EDGE,"E67"),sQuery(id+"F0.wireOp",EDGE,"E68"),sQuery(id+"F0.wireOp",EDGE,"E69"),sQuery(id+"F0.wireOp",EDGE,"E70"),sQuery(id+"F0.wireOp",EDGE,"E71"),sQuery(id+"F0.wireOp",EDGE,"E72"),sQuery(id+"F0.wireOp",EDGE,"E73"),sQuery(id+"F0.wireOp",EDGE,"E74"),sQuery(id+"F0.wireOp",EDGE,"E75"),sQuery(id+"F0.wireOp",EDGE,"E76"),sQuery(id+"F0.wireOp",EDGE,"E77"),sQuery(id+"F0.wireOp",EDGE,"E78"),sQuery(id+"F0.wireOp",EDGE,"E79"),sQuery(id+"F0.wireOp",EDGE,"E80"),sQuery(id+"F0.wireOp",EDGE,"E81"),sQuery(id+"F0.wireOp",EDGE,"E82"),sQuery(id+"F0.wireOp",EDGE,"E83"),sQuery(id+"F0.wireOp",EDGE,"E84"),sQuery(id+"F0.wireOp",EDGE,"E85"),sQuery(id+"F0.wireOp",EDGE,"E86"),sQuery(id+"F0.wireOp",EDGE,"E87"),sQuery(id+"F0.wireOp",EDGE,"E88"),sQuery(id+"F0.wireOp",EDGE,"E89"),sQuery(id+"F0.wireOp",EDGE,"E90"),sQuery(id+"F0.wireOp",EDGE,"E91"),sQuery(id+"F0.wireOp",EDGE,"E92"),sQuery(id+"F0.wireOp",EDGE,"E93"),sQuery(id+"F0.wireOp",EDGE,"E94"),sQuery(id+"F0.wireOp",EDGE,"E95"),sQuery(id+"F0.wireOp",EDGE,"E96"),sQuery(id+"F0.wireOp",EDGE,"E97"),sQuery(id+"F0.wireOp",EDGE,"E98"),sQuery(id+"F0.wireOp",EDGE,"E99"),sQuery(id+"F0.wireOp",EDGE,"E100"),sQuery(id+"F0.wireOp",EDGE,"E101"),sQuery(id+"F0.wireOp",EDGE,"E102"),sQuery(id+"F0.wireOp",EDGE,"E103"),sQuery(id+"F0.wireOp",EDGE,"E104")])]}),"instanceName":"49"});
            var Q17;
            Q17=makeQuery(id+"F2.opPattern","COPY",BODY,{"derivedFrom":makeQuery(id+"F1.opExtrude","SWEPT_BODY",BODY,{"disambiguationData":[OSD([sQuery(id+"F0.wireOp",EDGE,"E1"),sQuery(id+"F0.wireOp",EDGE,"E2"),sQuery(id+"F0.wireOp",EDGE,"E3"),sQuery(id+"F0.wireOp",EDGE,"E4"),sQuery(id+"F0.wireOp",EDGE,"E5"),sQuery(id+"F0.wireOp",EDGE,"E6"),sQuery(id+"F0.wireOp",EDGE,"E7"),sQuery(id+"F0.wireOp",EDGE,"E8"),sQuery(id+"F0.wireOp",EDGE,"E9"),sQuery(id+"F0.wireOp",EDGE,"E10"),sQuery(id+"F0.wireOp",EDGE,"E11"),sQuery(id+"F0.wireOp",EDGE,"E12"),sQuery(id+"F0.wireOp",EDGE,"E13"),sQuery(id+"F0.wireOp",EDGE,"E14"),sQuery(id+"F0.wireOp",EDGE,"E15"),sQuery(id+"F0.wireOp",EDGE,"E16"),sQuery(id+"F0.wireOp",EDGE,"E17"),sQuery(id+"F0.wireOp",EDGE,"E18"),sQuery(id+"F0.wireOp",EDGE,"E19"),sQuery(id+"F0.wireOp",EDGE,"E20"),sQuery(id+"F0.wireOp",EDGE,"E21"),sQuery(id+"F0.wireOp",EDGE,"E22"),sQuery(id+"F0.wireOp",EDGE,"E23"),sQuery(id+"F0.wireOp",EDGE,"E24"),sQuery(id+"F0.wireOp",EDGE,"E25"),sQuery(id+"F0.wireOp",EDGE,"E26"),sQuery(id+"F0.wireOp",EDGE,"E27"),sQuery(id+"F0.wireOp",EDGE,"E28"),sQuery(id+"F0.wireOp",EDGE,"E29"),sQuery(id+"F0.wireOp",EDGE,"E30"),sQuery(id+"F0.wireOp",EDGE,"E31"),sQuery(id+"F0.wireOp",EDGE,"E32"),sQuery(id+"F0.wireOp",EDGE,"E33"),sQuery(id+"F0.wireOp",EDGE,"E34"),sQuery(id+"F0.wireOp",EDGE,"E35"),sQuery(id+"F0.wireOp",EDGE,"E36"),sQuery(id+"F0.wireOp",EDGE,"E37"),sQuery(id+"F0.wireOp",EDGE,"E38"),sQuery(id+"F0.wireOp",EDGE,"E39"),sQuery(id+"F0.wireOp",EDGE,"E40"),sQuery(id+"F0.wireOp",EDGE,"E41"),sQuery(id+"F0.wireOp",EDGE,"E42"),sQuery(id+"F0.wireOp",EDGE,"E43"),sQuery(id+"F0.wireOp",EDGE,"E44"),sQuery(id+"F0.wireOp",EDGE,"E45"),sQuery(id+"F0.wireOp",EDGE,"E46"),sQuery(id+"F0.wireOp",EDGE,"E47"),sQuery(id+"F0.wireOp",EDGE,"E48"),sQuery(id+"F0.wireOp",EDGE,"E49"),sQuery(id+"F0.wireOp",EDGE,"E50"),sQuery(id+"F0.wireOp",EDGE,"E51"),sQuery(id+"F0.wireOp",EDGE,"E52"),sQuery(id+"F0.wireOp",EDGE,"E53"),sQuery(id+"F0.wireOp",EDGE,"E54"),sQuery(id+"F0.wireOp",EDGE,"E55"),sQuery(id+"F0.wireOp",EDGE,"E56"),sQuery(id+"F0.wireOp",EDGE,"E57"),sQuery(id+"F0.wireOp",EDGE,"E58"),sQuery(id+"F0.wireOp",EDGE,"E59"),sQuery(id+"F0.wireOp",EDGE,"E60"),sQuery(id+"F0.wireOp",EDGE,"E61"),sQuery(id+"F0.wireOp",EDGE,"E62"),sQuery(id+"F0.wireOp",EDGE,"E63"),sQuery(id+"F0.wireOp",EDGE,"E64"),sQuery(id+"F0.wireOp",EDGE,"E65"),sQuery(id+"F0.wireOp",EDGE,"E66"),sQuery(id+"F0.wireOp",EDGE,"E67"),sQuery(id+"F0.wireOp",EDGE,"E68"),sQuery(id+"F0.wireOp",EDGE,"E69"),sQuery(id+"F0.wireOp",EDGE,"E70"),sQuery(id+"F0.wireOp",EDGE,"E71"),sQuery(id+"F0.wireOp",EDGE,"E72"),sQuery(id+"F0.wireOp",EDGE,"E73"),sQuery(id+"F0.wireOp",EDGE,"E74"),sQuery(id+"F0.wireOp",EDGE,"E75"),sQuery(id+"F0.wireOp",EDGE,"E76"),sQuery(id+"F0.wireOp",EDGE,"E77"),sQuery(id+"F0.wireOp",EDGE,"E78"),sQuery(id+"F0.wireOp",EDGE,"E79"),sQuery(id+"F0.wireOp",EDGE,"E80"),sQuery(id+"F0.wireOp",EDGE,"E81"),sQuery(id+"F0.wireOp",EDGE,"E82"),sQuery(id+"F0.wireOp",EDGE,"E83"),sQuery(id+"F0.wireOp",EDGE,"E84"),sQuery(id+"F0.wireOp",EDGE,"E85"),sQuery(id+"F0.wireOp",EDGE,"E86"),sQuery(id+"F0.wireOp",EDGE,"E87"),sQuery(id+"F0.wireOp",EDGE,"E88"),sQuery(id+"F0.wireOp",EDGE,"E89"),sQuery(id+"F0.wireOp",EDGE,"E90"),sQuery(id+"F0.wireOp",EDGE,"E91"),sQuery(id+"F0.wireOp",EDGE,"E92"),sQuery(id+"F0.wireOp",EDGE,"E93"),sQuery(id+"F0.wireOp",EDGE,"E94"),sQuery(id+"F0.wireOp",EDGE,"E95"),sQuery(id+"F0.wireOp",EDGE,"E96"),sQuery(id+"F0.wireOp",EDGE,"E97"),sQuery(id+"F0.wireOp",EDGE,"E98"),sQuery(id+"F0.wireOp",EDGE,"E99"),sQuery(id+"F0.wireOp",EDGE,"E100"),sQuery(id+"F0.wireOp",EDGE,"E101"),sQuery(id+"F0.wireOp",EDGE,"E102"),sQuery(id+"F0.wireOp",EDGE,"E103"),sQuery(id+"F0.wireOp",EDGE,"E104")])]}),"instanceName":"50"});
            var Q18;
            Q18=makeQuery(id+"F2.opPattern","COPY",BODY,{"derivedFrom":makeQuery(id+"F1.opExtrude","SWEPT_BODY",BODY,{"disambiguationData":[OSD([sQuery(id+"F0.wireOp",EDGE,"E1"),sQuery(id+"F0.wireOp",EDGE,"E2"),sQuery(id+"F0.wireOp",EDGE,"E3"),sQuery(id+"F0.wireOp",EDGE,"E4"),sQuery(id+"F0.wireOp",EDGE,"E5"),sQuery(id+"F0.wireOp",EDGE,"E6"),sQuery(id+"F0.wireOp",EDGE,"E7"),sQuery(id+"F0.wireOp",EDGE,"E8"),sQuery(id+"F0.wireOp",EDGE,"E9"),sQuery(id+"F0.wireOp",EDGE,"E10"),sQuery(id+"F0.wireOp",EDGE,"E11"),sQuery(id+"F0.wireOp",EDGE,"E12"),sQuery(id+"F0.wireOp",EDGE,"E13"),sQuery(id+"F0.wireOp",EDGE,"E14"),sQuery(id+"F0.wireOp",EDGE,"E15"),sQuery(id+"F0.wireOp",EDGE,"E16"),sQuery(id+"F0.wireOp",EDGE,"E17"),sQuery(id+"F0.wireOp",EDGE,"E18"),sQuery(id+"F0.wireOp",EDGE,"E19"),sQuery(id+"F0.wireOp",EDGE,"E20"),sQuery(id+"F0.wireOp",EDGE,"E21"),sQuery(id+"F0.wireOp",EDGE,"E22"),sQuery(id+"F0.wireOp",EDGE,"E23"),sQuery(id+"F0.wireOp",EDGE,"E24"),sQuery(id+"F0.wireOp",EDGE,"E25"),sQuery(id+"F0.wireOp",EDGE,"E26"),sQuery(id+"F0.wireOp",EDGE,"E27"),sQuery(id+"F0.wireOp",EDGE,"E28"),sQuery(id+"F0.wireOp",EDGE,"E29"),sQuery(id+"F0.wireOp",EDGE,"E30"),sQuery(id+"F0.wireOp",EDGE,"E31"),sQuery(id+"F0.wireOp",EDGE,"E32"),sQuery(id+"F0.wireOp",EDGE,"E33"),sQuery(id+"F0.wireOp",EDGE,"E34"),sQuery(id+"F0.wireOp",EDGE,"E35"),sQuery(id+"F0.wireOp",EDGE,"E36"),sQuery(id+"F0.wireOp",EDGE,"E37"),sQuery(id+"F0.wireOp",EDGE,"E38"),sQuery(id+"F0.wireOp",EDGE,"E39"),sQuery(id+"F0.wireOp",EDGE,"E40"),sQuery(id+"F0.wireOp",EDGE,"E41"),sQuery(id+"F0.wireOp",EDGE,"E42"),sQuery(id+"F0.wireOp",EDGE,"E43"),sQuery(id+"F0.wireOp",EDGE,"E44"),sQuery(id+"F0.wireOp",EDGE,"E45"),sQuery(id+"F0.wireOp",EDGE,"E46"),sQuery(id+"F0.wireOp",EDGE,"E47"),sQuery(id+"F0.wireOp",EDGE,"E48"),sQuery(id+"F0.wireOp",EDGE,"E49"),sQuery(id+"F0.wireOp",EDGE,"E50"),sQuery(id+"F0.wireOp",EDGE,"E51"),sQuery(id+"F0.wireOp",EDGE,"E52"),sQuery(id+"F0.wireOp",EDGE,"E53"),sQuery(id+"F0.wireOp",EDGE,"E54"),sQuery(id+"F0.wireOp",EDGE,"E55"),sQuery(id+"F0.wireOp",EDGE,"E56"),sQuery(id+"F0.wireOp",EDGE,"E57"),sQuery(id+"F0.wireOp",EDGE,"E58"),sQuery(id+"F0.wireOp",EDGE,"E59"),sQuery(id+"F0.wireOp",EDGE,"E60"),sQuery(id+"F0.wireOp",EDGE,"E61"),sQuery(id+"F0.wireOp",EDGE,"E62"),sQuery(id+"F0.wireOp",EDGE,"E63"),sQuery(id+"F0.wireOp",EDGE,"E64"),sQuery(id+"F0.wireOp",EDGE,"E65"),sQuery(id+"F0.wireOp",EDGE,"E66"),sQuery(id+"F0.wireOp",EDGE,"E67"),sQuery(id+"F0.wireOp",EDGE,"E68"),sQuery(id+"F0.wireOp",EDGE,"E69"),sQuery(id+"F0.wireOp",EDGE,"E70"),sQuery(id+"F0.wireOp",EDGE,"E71"),sQuery(id+"F0.wireOp",EDGE,"E72"),sQuery(id+"F0.wireOp",EDGE,"E73"),sQuery(id+"F0.wireOp",EDGE,"E74"),sQuery(id+"F0.wireOp",EDGE,"E75"),sQuery(id+"F0.wireOp",EDGE,"E76"),sQuery(id+"F0.wireOp",EDGE,"E77"),sQuery(id+"F0.wireOp",EDGE,"E78"),sQuery(id+"F0.wireOp",EDGE,"E79"),sQuery(id+"F0.wireOp",EDGE,"E80"),sQuery(id+"F0.wireOp",EDGE,"E81"),sQuery(id+"F0.wireOp",EDGE,"E82"),sQuery(id+"F0.wireOp",EDGE,"E83"),sQuery(id+"F0.wireOp",EDGE,"E84"),sQuery(id+"F0.wireOp",EDGE,"E85"),sQuery(id+"F0.wireOp",EDGE,"E86"),sQuery(id+"F0.wireOp",EDGE,"E87"),sQuery(id+"F0.wireOp",EDGE,"E88"),sQuery(id+"F0.wireOp",EDGE,"E89"),sQuery(id+"F0.wireOp",EDGE,"E90"),sQuery(id+"F0.wireOp",EDGE,"E91"),sQuery(id+"F0.wireOp",EDGE,"E92"),sQuery(id+"F0.wireOp",EDGE,"E93"),sQuery(id+"F0.wireOp",EDGE,"E94"),sQuery(id+"F0.wireOp",EDGE,"E95"),sQuery(id+"F0.wireOp",EDGE,"E96"),sQuery(id+"F0.wireOp",EDGE,"E97"),sQuery(id+"F0.wireOp",EDGE,"E98"),sQuery(id+"F0.wireOp",EDGE,"E99"),sQuery(id+"F0.wireOp",EDGE,"E100"),sQuery(id+"F0.wireOp",EDGE,"E101"),sQuery(id+"F0.wireOp",EDGE,"E102"),sQuery(id+"F0.wireOp",EDGE,"E103"),sQuery(id+"F0.wireOp",EDGE,"E104")])]}),"instanceName":"51"});
            var Q19;
            Q19=makeQuery(id+"F2.opPattern","COPY",BODY,{"derivedFrom":makeQuery(id+"F1.opExtrude","SWEPT_BODY",BODY,{"disambiguationData":[OSD([sQuery(id+"F0.wireOp",EDGE,"E1"),sQuery(id+"F0.wireOp",EDGE,"E2"),sQuery(id+"F0.wireOp",EDGE,"E3"),sQuery(id+"F0.wireOp",EDGE,"E4"),sQuery(id+"F0.wireOp",EDGE,"E5"),sQuery(id+"F0.wireOp",EDGE,"E6"),sQuery(id+"F0.wireOp",EDGE,"E7"),sQuery(id+"F0.wireOp",EDGE,"E8"),sQuery(id+"F0.wireOp",EDGE,"E9"),sQuery(id+"F0.wireOp",EDGE,"E10"),sQuery(id+"F0.wireOp",EDGE,"E11"),sQuery(id+"F0.wireOp",EDGE,"E12"),sQuery(id+"F0.wireOp",EDGE,"E13"),sQuery(id+"F0.wireOp",EDGE,"E14"),sQuery(id+"F0.wireOp",EDGE,"E15"),sQuery(id+"F0.wireOp",EDGE,"E16"),sQuery(id+"F0.wireOp",EDGE,"E17"),sQuery(id+"F0.wireOp",EDGE,"E18"),sQuery(id+"F0.wireOp",EDGE,"E19"),sQuery(id+"F0.wireOp",EDGE,"E20"),sQuery(id+"F0.wireOp",EDGE,"E21"),sQuery(id+"F0.wireOp",EDGE,"E22"),sQuery(id+"F0.wireOp",EDGE,"E23"),sQuery(id+"F0.wireOp",EDGE,"E24"),sQuery(id+"F0.wireOp",EDGE,"E25"),sQuery(id+"F0.wireOp",EDGE,"E26"),sQuery(id+"F0.wireOp",EDGE,"E27"),sQuery(id+"F0.wireOp",EDGE,"E28"),sQuery(id+"F0.wireOp",EDGE,"E29"),sQuery(id+"F0.wireOp",EDGE,"E30"),sQuery(id+"F0.wireOp",EDGE,"E31"),sQuery(id+"F0.wireOp",EDGE,"E32"),sQuery(id+"F0.wireOp",EDGE,"E33"),sQuery(id+"F0.wireOp",EDGE,"E34"),sQuery(id+"F0.wireOp",EDGE,"E35"),sQuery(id+"F0.wireOp",EDGE,"E36"),sQuery(id+"F0.wireOp",EDGE,"E37"),sQuery(id+"F0.wireOp",EDGE,"E38"),sQuery(id+"F0.wireOp",EDGE,"E39"),sQuery(id+"F0.wireOp",EDGE,"E40"),sQuery(id+"F0.wireOp",EDGE,"E41"),sQuery(id+"F0.wireOp",EDGE,"E42"),sQuery(id+"F0.wireOp",EDGE,"E43"),sQuery(id+"F0.wireOp",EDGE,"E44"),sQuery(id+"F0.wireOp",EDGE,"E45"),sQuery(id+"F0.wireOp",EDGE,"E46"),sQuery(id+"F0.wireOp",EDGE,"E47"),sQuery(id+"F0.wireOp",EDGE,"E48"),sQuery(id+"F0.wireOp",EDGE,"E49"),sQuery(id+"F0.wireOp",EDGE,"E50"),sQuery(id+"F0.wireOp",EDGE,"E51"),sQuery(id+"F0.wireOp",EDGE,"E52"),sQuery(id+"F0.wireOp",EDGE,"E53"),sQuery(id+"F0.wireOp",EDGE,"E54"),sQuery(id+"F0.wireOp",EDGE,"E55"),sQuery(id+"F0.wireOp",EDGE,"E56"),sQuery(id+"F0.wireOp",EDGE,"E57"),sQuery(id+"F0.wireOp",EDGE,"E58"),sQuery(id+"F0.wireOp",EDGE,"E59"),sQuery(id+"F0.wireOp",EDGE,"E60"),sQuery(id+"F0.wireOp",EDGE,"E61"),sQuery(id+"F0.wireOp",EDGE,"E62"),sQuery(id+"F0.wireOp",EDGE,"E63"),sQuery(id+"F0.wireOp",EDGE,"E64"),sQuery(id+"F0.wireOp",EDGE,"E65"),sQuery(id+"F0.wireOp",EDGE,"E66"),sQuery(id+"F0.wireOp",EDGE,"E67"),sQuery(id+"F0.wireOp",EDGE,"E68"),sQuery(id+"F0.wireOp",EDGE,"E69"),sQuery(id+"F0.wireOp",EDGE,"E70"),sQuery(id+"F0.wireOp",EDGE,"E71"),sQuery(id+"F0.wireOp",EDGE,"E72"),sQuery(id+"F0.wireOp",EDGE,"E73"),sQuery(id+"F0.wireOp",EDGE,"E74"),sQuery(id+"F0.wireOp",EDGE,"E75"),sQuery(id+"F0.wireOp",EDGE,"E76"),sQuery(id+"F0.wireOp",EDGE,"E77"),sQuery(id+"F0.wireOp",EDGE,"E78"),sQuery(id+"F0.wireOp",EDGE,"E79"),sQuery(id+"F0.wireOp",EDGE,"E80"),sQuery(id+"F0.wireOp",EDGE,"E81"),sQuery(id+"F0.wireOp",EDGE,"E82"),sQuery(id+"F0.wireOp",EDGE,"E83"),sQuery(id+"F0.wireOp",EDGE,"E84"),sQuery(id+"F0.wireOp",EDGE,"E85"),sQuery(id+"F0.wireOp",EDGE,"E86"),sQuery(id+"F0.wireOp",EDGE,"E87"),sQuery(id+"F0.wireOp",EDGE,"E88"),sQuery(id+"F0.wireOp",EDGE,"E89"),sQuery(id+"F0.wireOp",EDGE,"E90"),sQuery(id+"F0.wireOp",EDGE,"E91"),sQuery(id+"F0.wireOp",EDGE,"E92"),sQuery(id+"F0.wireOp",EDGE,"E93"),sQuery(id+"F0.wireOp",EDGE,"E94"),sQuery(id+"F0.wireOp",EDGE,"E95"),sQuery(id+"F0.wireOp",EDGE,"E96"),sQuery(id+"F0.wireOp",EDGE,"E97"),sQuery(id+"F0.wireOp",EDGE,"E98"),sQuery(id+"F0.wireOp",EDGE,"E99"),sQuery(id+"F0.wireOp",EDGE,"E100"),sQuery(id+"F0.wireOp",EDGE,"E101"),sQuery(id+"F0.wireOp",EDGE,"E102"),sQuery(id+"F0.wireOp",EDGE,"E103"),sQuery(id+"F0.wireOp",EDGE,"E104")])]}),"instanceName":"52"});
            var Q20;
            Q20=makeQuery(id+"F2.opPattern","COPY",BODY,{"derivedFrom":makeQuery(id+"F1.opExtrude","SWEPT_BODY",BODY,{"disambiguationData":[OSD([sQuery(id+"F0.wireOp",EDGE,"E1"),sQuery(id+"F0.wireOp",EDGE,"E2"),sQuery(id+"F0.wireOp",EDGE,"E3"),sQuery(id+"F0.wireOp",EDGE,"E4"),sQuery(id+"F0.wireOp",EDGE,"E5"),sQuery(id+"F0.wireOp",EDGE,"E6"),sQuery(id+"F0.wireOp",EDGE,"E7"),sQuery(id+"F0.wireOp",EDGE,"E8"),sQuery(id+"F0.wireOp",EDGE,"E9"),sQuery(id+"F0.wireOp",EDGE,"E10"),sQuery(id+"F0.wireOp",EDGE,"E11"),sQuery(id+"F0.wireOp",EDGE,"E12"),sQuery(id+"F0.wireOp",EDGE,"E13"),sQuery(id+"F0.wireOp",EDGE,"E14"),sQuery(id+"F0.wireOp",EDGE,"E15"),sQuery(id+"F0.wireOp",EDGE,"E16"),sQuery(id+"F0.wireOp",EDGE,"E17"),sQuery(id+"F0.wireOp",EDGE,"E18"),sQuery(id+"F0.wireOp",EDGE,"E19"),sQuery(id+"F0.wireOp",EDGE,"E20"),sQuery(id+"F0.wireOp",EDGE,"E21"),sQuery(id+"F0.wireOp",EDGE,"E22"),sQuery(id+"F0.wireOp",EDGE,"E23"),sQuery(id+"F0.wireOp",EDGE,"E24"),sQuery(id+"F0.wireOp",EDGE,"E25"),sQuery(id+"F0.wireOp",EDGE,"E26"),sQuery(id+"F0.wireOp",EDGE,"E27"),sQuery(id+"F0.wireOp",EDGE,"E28"),sQuery(id+"F0.wireOp",EDGE,"E29"),sQuery(id+"F0.wireOp",EDGE,"E30"),sQuery(id+"F0.wireOp",EDGE,"E31"),sQuery(id+"F0.wireOp",EDGE,"E32"),sQuery(id+"F0.wireOp",EDGE,"E33"),sQuery(id+"F0.wireOp",EDGE,"E34"),sQuery(id+"F0.wireOp",EDGE,"E35"),sQuery(id+"F0.wireOp",EDGE,"E36"),sQuery(id+"F0.wireOp",EDGE,"E37"),sQuery(id+"F0.wireOp",EDGE,"E38"),sQuery(id+"F0.wireOp",EDGE,"E39"),sQuery(id+"F0.wireOp",EDGE,"E40"),sQuery(id+"F0.wireOp",EDGE,"E41"),sQuery(id+"F0.wireOp",EDGE,"E42"),sQuery(id+"F0.wireOp",EDGE,"E43"),sQuery(id+"F0.wireOp",EDGE,"E44"),sQuery(id+"F0.wireOp",EDGE,"E45"),sQuery(id+"F0.wireOp",EDGE,"E46"),sQuery(id+"F0.wireOp",EDGE,"E47"),sQuery(id+"F0.wireOp",EDGE,"E48"),sQuery(id+"F0.wireOp",EDGE,"E49"),sQuery(id+"F0.wireOp",EDGE,"E50"),sQuery(id+"F0.wireOp",EDGE,"E51"),sQuery(id+"F0.wireOp",EDGE,"E52"),sQuery(id+"F0.wireOp",EDGE,"E53"),sQuery(id+"F0.wireOp",EDGE,"E54"),sQuery(id+"F0.wireOp",EDGE,"E55"),sQuery(id+"F0.wireOp",EDGE,"E56"),sQuery(id+"F0.wireOp",EDGE,"E57"),sQuery(id+"F0.wireOp",EDGE,"E58"),sQuery(id+"F0.wireOp",EDGE,"E59"),sQuery(id+"F0.wireOp",EDGE,"E60"),sQuery(id+"F0.wireOp",EDGE,"E61"),sQuery(id+"F0.wireOp",EDGE,"E62"),sQuery(id+"F0.wireOp",EDGE,"E63"),sQuery(id+"F0.wireOp",EDGE,"E64"),sQuery(id+"F0.wireOp",EDGE,"E65"),sQuery(id+"F0.wireOp",EDGE,"E66"),sQuery(id+"F0.wireOp",EDGE,"E67"),sQuery(id+"F0.wireOp",EDGE,"E68"),sQuery(id+"F0.wireOp",EDGE,"E69"),sQuery(id+"F0.wireOp",EDGE,"E70"),sQuery(id+"F0.wireOp",EDGE,"E71"),sQuery(id+"F0.wireOp",EDGE,"E72"),sQuery(id+"F0.wireOp",EDGE,"E73"),sQuery(id+"F0.wireOp",EDGE,"E74"),sQuery(id+"F0.wireOp",EDGE,"E75"),sQuery(id+"F0.wireOp",EDGE,"E76"),sQuery(id+"F0.wireOp",EDGE,"E77"),sQuery(id+"F0.wireOp",EDGE,"E78"),sQuery(id+"F0.wireOp",EDGE,"E79"),sQuery(id+"F0.wireOp",EDGE,"E80"),sQuery(id+"F0.wireOp",EDGE,"E81"),sQuery(id+"F0.wireOp",EDGE,"E82"),sQuery(id+"F0.wireOp",EDGE,"E83"),sQuery(id+"F0.wireOp",EDGE,"E84"),sQuery(id+"F0.wireOp",EDGE,"E85"),sQuery(id+"F0.wireOp",EDGE,"E86"),sQuery(id+"F0.wireOp",EDGE,"E87"),sQuery(id+"F0.wireOp",EDGE,"E88"),sQuery(id+"F0.wireOp",EDGE,"E89"),sQuery(id+"F0.wireOp",EDGE,"E90"),sQuery(id+"F0.wireOp",EDGE,"E91"),sQuery(id+"F0.wireOp",EDGE,"E92"),sQuery(id+"F0.wireOp",EDGE,"E93"),sQuery(id+"F0.wireOp",EDGE,"E94"),sQuery(id+"F0.wireOp",EDGE,"E95"),sQuery(id+"F0.wireOp",EDGE,"E96"),sQuery(id+"F0.wireOp",EDGE,"E97"),sQuery(id+"F0.wireOp",EDGE,"E98"),sQuery(id+"F0.wireOp",EDGE,"E99"),sQuery(id+"F0.wireOp",EDGE,"E100"),sQuery(id+"F0.wireOp",EDGE,"E101"),sQuery(id+"F0.wireOp",EDGE,"E102"),sQuery(id+"F0.wireOp",EDGE,"E103"),sQuery(id+"F0.wireOp",EDGE,"E104")])]}),"instanceName":"53"});
            var Q21;
            Q21=makeQuery(id+"F2.opPattern","COPY",BODY,{"derivedFrom":makeQuery(id+"F1.opExtrude","SWEPT_BODY",BODY,{"disambiguationData":[OSD([sQuery(id+"F0.wireOp",EDGE,"E1"),sQuery(id+"F0.wireOp",EDGE,"E2"),sQuery(id+"F0.wireOp",EDGE,"E3"),sQuery(id+"F0.wireOp",EDGE,"E4"),sQuery(id+"F0.wireOp",EDGE,"E5"),sQuery(id+"F0.wireOp",EDGE,"E6"),sQuery(id+"F0.wireOp",EDGE,"E7"),sQuery(id+"F0.wireOp",EDGE,"E8"),sQuery(id+"F0.wireOp",EDGE,"E9"),sQuery(id+"F0.wireOp",EDGE,"E10"),sQuery(id+"F0.wireOp",EDGE,"E11"),sQuery(id+"F0.wireOp",EDGE,"E12"),sQuery(id+"F0.wireOp",EDGE,"E13"),sQuery(id+"F0.wireOp",EDGE,"E14"),sQuery(id+"F0.wireOp",EDGE,"E15"),sQuery(id+"F0.wireOp",EDGE,"E16"),sQuery(id+"F0.wireOp",EDGE,"E17"),sQuery(id+"F0.wireOp",EDGE,"E18"),sQuery(id+"F0.wireOp",EDGE,"E19"),sQuery(id+"F0.wireOp",EDGE,"E20"),sQuery(id+"F0.wireOp",EDGE,"E21"),sQuery(id+"F0.wireOp",EDGE,"E22"),sQuery(id+"F0.wireOp",EDGE,"E23"),sQuery(id+"F0.wireOp",EDGE,"E24"),sQuery(id+"F0.wireOp",EDGE,"E25"),sQuery(id+"F0.wireOp",EDGE,"E26"),sQuery(id+"F0.wireOp",EDGE,"E27"),sQuery(id+"F0.wireOp",EDGE,"E28"),sQuery(id+"F0.wireOp",EDGE,"E29"),sQuery(id+"F0.wireOp",EDGE,"E30"),sQuery(id+"F0.wireOp",EDGE,"E31"),sQuery(id+"F0.wireOp",EDGE,"E32"),sQuery(id+"F0.wireOp",EDGE,"E33"),sQuery(id+"F0.wireOp",EDGE,"E34"),sQuery(id+"F0.wireOp",EDGE,"E35"),sQuery(id+"F0.wireOp",EDGE,"E36"),sQuery(id+"F0.wireOp",EDGE,"E37"),sQuery(id+"F0.wireOp",EDGE,"E38"),sQuery(id+"F0.wireOp",EDGE,"E39"),sQuery(id+"F0.wireOp",EDGE,"E40"),sQuery(id+"F0.wireOp",EDGE,"E41"),sQuery(id+"F0.wireOp",EDGE,"E42"),sQuery(id+"F0.wireOp",EDGE,"E43"),sQuery(id+"F0.wireOp",EDGE,"E44"),sQuery(id+"F0.wireOp",EDGE,"E45"),sQuery(id+"F0.wireOp",EDGE,"E46"),sQuery(id+"F0.wireOp",EDGE,"E47"),sQuery(id+"F0.wireOp",EDGE,"E48"),sQuery(id+"F0.wireOp",EDGE,"E49"),sQuery(id+"F0.wireOp",EDGE,"E50"),sQuery(id+"F0.wireOp",EDGE,"E51"),sQuery(id+"F0.wireOp",EDGE,"E52"),sQuery(id+"F0.wireOp",EDGE,"E53"),sQuery(id+"F0.wireOp",EDGE,"E54"),sQuery(id+"F0.wireOp",EDGE,"E55"),sQuery(id+"F0.wireOp",EDGE,"E56"),sQuery(id+"F0.wireOp",EDGE,"E57"),sQuery(id+"F0.wireOp",EDGE,"E58"),sQuery(id+"F0.wireOp",EDGE,"E59"),sQuery(id+"F0.wireOp",EDGE,"E60"),sQuery(id+"F0.wireOp",EDGE,"E61"),sQuery(id+"F0.wireOp",EDGE,"E62"),sQuery(id+"F0.wireOp",EDGE,"E63"),sQuery(id+"F0.wireOp",EDGE,"E64"),sQuery(id+"F0.wireOp",EDGE,"E65"),sQuery(id+"F0.wireOp",EDGE,"E66"),sQuery(id+"F0.wireOp",EDGE,"E67"),sQuery(id+"F0.wireOp",EDGE,"E68"),sQuery(id+"F0.wireOp",EDGE,"E69"),sQuery(id+"F0.wireOp",EDGE,"E70"),sQuery(id+"F0.wireOp",EDGE,"E71"),sQuery(id+"F0.wireOp",EDGE,"E72"),sQuery(id+"F0.wireOp",EDGE,"E73"),sQuery(id+"F0.wireOp",EDGE,"E74"),sQuery(id+"F0.wireOp",EDGE,"E75"),sQuery(id+"F0.wireOp",EDGE,"E76"),sQuery(id+"F0.wireOp",EDGE,"E77"),sQuery(id+"F0.wireOp",EDGE,"E78"),sQuery(id+"F0.wireOp",EDGE,"E79"),sQuery(id+"F0.wireOp",EDGE,"E80"),sQuery(id+"F0.wireOp",EDGE,"E81"),sQuery(id+"F0.wireOp",EDGE,"E82"),sQuery(id+"F0.wireOp",EDGE,"E83"),sQuery(id+"F0.wireOp",EDGE,"E84"),sQuery(id+"F0.wireOp",EDGE,"E85"),sQuery(id+"F0.wireOp",EDGE,"E86"),sQuery(id+"F0.wireOp",EDGE,"E87"),sQuery(id+"F0.wireOp",EDGE,"E88"),sQuery(id+"F0.wireOp",EDGE,"E89"),sQuery(id+"F0.wireOp",EDGE,"E90"),sQuery(id+"F0.wireOp",EDGE,"E91"),sQuery(id+"F0.wireOp",EDGE,"E92"),sQuery(id+"F0.wireOp",EDGE,"E93"),sQuery(id+"F0.wireOp",EDGE,"E94"),sQuery(id+"F0.wireOp",EDGE,"E95"),sQuery(id+"F0.wireOp",EDGE,"E96"),sQuery(id+"F0.wireOp",EDGE,"E97"),sQuery(id+"F0.wireOp",EDGE,"E98"),sQuery(id+"F0.wireOp",EDGE,"E99"),sQuery(id+"F0.wireOp",EDGE,"E100"),sQuery(id+"F0.wireOp",EDGE,"E101"),sQuery(id+"F0.wireOp",EDGE,"E102"),sQuery(id+"F0.wireOp",EDGE,"E103"),sQuery(id+"F0.wireOp",EDGE,"E104")])]}),"instanceName":"54"});
            var Q22;
            Q22=makeQuery(id+"F2.opPattern","COPY",BODY,{"derivedFrom":makeQuery(id+"F1.opExtrude","SWEPT_BODY",BODY,{"disambiguationData":[OSD([sQuery(id+"F0.wireOp",EDGE,"E1"),sQuery(id+"F0.wireOp",EDGE,"E2"),sQuery(id+"F0.wireOp",EDGE,"E3"),sQuery(id+"F0.wireOp",EDGE,"E4"),sQuery(id+"F0.wireOp",EDGE,"E5"),sQuery(id+"F0.wireOp",EDGE,"E6"),sQuery(id+"F0.wireOp",EDGE,"E7"),sQuery(id+"F0.wireOp",EDGE,"E8"),sQuery(id+"F0.wireOp",EDGE,"E9"),sQuery(id+"F0.wireOp",EDGE,"E10"),sQuery(id+"F0.wireOp",EDGE,"E11"),sQuery(id+"F0.wireOp",EDGE,"E12"),sQuery(id+"F0.wireOp",EDGE,"E13"),sQuery(id+"F0.wireOp",EDGE,"E14"),sQuery(id+"F0.wireOp",EDGE,"E15"),sQuery(id+"F0.wireOp",EDGE,"E16"),sQuery(id+"F0.wireOp",EDGE,"E17"),sQuery(id+"F0.wireOp",EDGE,"E18"),sQuery(id+"F0.wireOp",EDGE,"E19"),sQuery(id+"F0.wireOp",EDGE,"E20"),sQuery(id+"F0.wireOp",EDGE,"E21"),sQuery(id+"F0.wireOp",EDGE,"E22"),sQuery(id+"F0.wireOp",EDGE,"E23"),sQuery(id+"F0.wireOp",EDGE,"E24"),sQuery(id+"F0.wireOp",EDGE,"E25"),sQuery(id+"F0.wireOp",EDGE,"E26"),sQuery(id+"F0.wireOp",EDGE,"E27"),sQuery(id+"F0.wireOp",EDGE,"E28"),sQuery(id+"F0.wireOp",EDGE,"E29"),sQuery(id+"F0.wireOp",EDGE,"E30"),sQuery(id+"F0.wireOp",EDGE,"E31"),sQuery(id+"F0.wireOp",EDGE,"E32"),sQuery(id+"F0.wireOp",EDGE,"E33"),sQuery(id+"F0.wireOp",EDGE,"E34"),sQuery(id+"F0.wireOp",EDGE,"E35"),sQuery(id+"F0.wireOp",EDGE,"E36"),sQuery(id+"F0.wireOp",EDGE,"E37"),sQuery(id+"F0.wireOp",EDGE,"E38"),sQuery(id+"F0.wireOp",EDGE,"E39"),sQuery(id+"F0.wireOp",EDGE,"E40"),sQuery(id+"F0.wireOp",EDGE,"E41"),sQuery(id+"F0.wireOp",EDGE,"E42"),sQuery(id+"F0.wireOp",EDGE,"E43"),sQuery(id+"F0.wireOp",EDGE,"E44"),sQuery(id+"F0.wireOp",EDGE,"E45"),sQuery(id+"F0.wireOp",EDGE,"E46"),sQuery(id+"F0.wireOp",EDGE,"E47"),sQuery(id+"F0.wireOp",EDGE,"E48"),sQuery(id+"F0.wireOp",EDGE,"E49"),sQuery(id+"F0.wireOp",EDGE,"E50"),sQuery(id+"F0.wireOp",EDGE,"E51"),sQuery(id+"F0.wireOp",EDGE,"E52"),sQuery(id+"F0.wireOp",EDGE,"E53"),sQuery(id+"F0.wireOp",EDGE,"E54"),sQuery(id+"F0.wireOp",EDGE,"E55"),sQuery(id+"F0.wireOp",EDGE,"E56"),sQuery(id+"F0.wireOp",EDGE,"E57"),sQuery(id+"F0.wireOp",EDGE,"E58"),sQuery(id+"F0.wireOp",EDGE,"E59"),sQuery(id+"F0.wireOp",EDGE,"E60"),sQuery(id+"F0.wireOp",EDGE,"E61"),sQuery(id+"F0.wireOp",EDGE,"E62"),sQuery(id+"F0.wireOp",EDGE,"E63"),sQuery(id+"F0.wireOp",EDGE,"E64"),sQuery(id+"F0.wireOp",EDGE,"E65"),sQuery(id+"F0.wireOp",EDGE,"E66"),sQuery(id+"F0.wireOp",EDGE,"E67"),sQuery(id+"F0.wireOp",EDGE,"E68"),sQuery(id+"F0.wireOp",EDGE,"E69"),sQuery(id+"F0.wireOp",EDGE,"E70"),sQuery(id+"F0.wireOp",EDGE,"E71"),sQuery(id+"F0.wireOp",EDGE,"E72"),sQuery(id+"F0.wireOp",EDGE,"E73"),sQuery(id+"F0.wireOp",EDGE,"E74"),sQuery(id+"F0.wireOp",EDGE,"E75"),sQuery(id+"F0.wireOp",EDGE,"E76"),sQuery(id+"F0.wireOp",EDGE,"E77"),sQuery(id+"F0.wireOp",EDGE,"E78"),sQuery(id+"F0.wireOp",EDGE,"E79"),sQuery(id+"F0.wireOp",EDGE,"E80"),sQuery(id+"F0.wireOp",EDGE,"E81"),sQuery(id+"F0.wireOp",EDGE,"E82"),sQuery(id+"F0.wireOp",EDGE,"E83"),sQuery(id+"F0.wireOp",EDGE,"E84"),sQuery(id+"F0.wireOp",EDGE,"E85"),sQuery(id+"F0.wireOp",EDGE,"E86"),sQuery(id+"F0.wireOp",EDGE,"E87"),sQuery(id+"F0.wireOp",EDGE,"E88"),sQuery(id+"F0.wireOp",EDGE,"E89"),sQuery(id+"F0.wireOp",EDGE,"E90"),sQuery(id+"F0.wireOp",EDGE,"E91"),sQuery(id+"F0.wireOp",EDGE,"E92"),sQuery(id+"F0.wireOp",EDGE,"E93"),sQuery(id+"F0.wireOp",EDGE,"E94"),sQuery(id+"F0.wireOp",EDGE,"E95"),sQuery(id+"F0.wireOp",EDGE,"E96"),sQuery(id+"F0.wireOp",EDGE,"E97"),sQuery(id+"F0.wireOp",EDGE,"E98"),sQuery(id+"F0.wireOp",EDGE,"E99"),sQuery(id+"F0.wireOp",EDGE,"E100"),sQuery(id+"F0.wireOp",EDGE,"E101"),sQuery(id+"F0.wireOp",EDGE,"E102"),sQuery(id+"F0.wireOp",EDGE,"E103"),sQuery(id+"F0.wireOp",EDGE,"E104")])]}),"instanceName":"55"});
            booleanBodies(context, id + "F5", {"operationType" : BooleanOperationType.UNION, "tools" : qUnion([Q0, Q1, Q2, Q3, Q4, Q5, Q6, Q7, Q8, Q9, Q10, Q11, Q12, Q13, Q14, Q15, Q16, Q17, Q18, Q19, Q20, Q21, Q22])});
        }
        {
            var Q0;
            Q0=qCreatedBy(makeId("Top.planeOp"),FACE);
            var sketch = newSketch(context, id + "F6", { "sketchPlane" : qUnion([Q0])});
            skCircle(sketch, "E106", {"center": v(0, 0) * mm, "radius": 3.69 * mm});
            skSolve(sketch);
        }
        {
            var Q0;
            Q0=makeQuery(id+"F6.imprint","IMPRINT",FACE,{"disambiguationData":[TD([[makeQuery(id+"F6.imprint","IMPRINT",EDGE,{"derivedFrom":sQuery(id+"F6.wireOp",EDGE,"E106")}),1.0]])]});
            extrude(context, id + "F7", {"entities" : qUnion([Q0]), "operationType" : NewBodyOperationType.REMOVE, "depth" : 25 * mm});
        }
        {
            var Q0;
            Q0=qCreatedBy(makeId("Top.planeOp"),FACE);
            var sketch = newSketch(context, id + "F8", { "sketchPlane" : qUnion([Q0])});
            skLineSegment(sketch, "E107.0", {"start": v(-52.74, -1.17) * mm, "end": v(-52.7, 2.25) * mm});
            skLineSegment(sketch, "E108", {"start": v(-52.73, 0) * mm, "end": v(-52.73, -37.85) * mm});
            skLineSegment(sketch, "E109", {"start": v(-52.73, -37.85) * mm, "end": v(-57.94, -37.85) * mm});
            skLineSegment(sketch, "E110", {"start": v(-57.94, -37.85) * mm, "end": v(-56.98, 30.53) * mm});
            skLineSegment(sketch, "E111", {"start": v(-56.98, 30.53) * mm, "end": v(-52.74, 30.48) * mm});
            skLineSegment(sketch, "E112", {"start": v(-52.74, 30.48) * mm, "end": v(-52.74, -1.17) * mm});
            skLineSegment(sketch, "E113.0", {"start": v(-44.67, 28.06) * mm, "end": v(-42.76, 30.89) * mm});
            skPoint(sketch, "E114.0", {"position": v(-46.4, 25.1) * mm});
            skLineSegment(sketch, "E115.0", {"start": v(-47.92, 22.05) * mm, "end": v(-46.4, 25.1) * mm});
            skLineSegment(sketch, "E116.0", {"start": v(-49.25, 18.9) * mm, "end": v(-47.92, 22.05) * mm});
            skLineSegment(sketch, "E117.0", {"start": v(-50.37, 15.67) * mm, "end": v(-49.25, 18.9) * mm});
            skLineSegment(sketch, "E118.0", {"start": v(-51.28, 12.38) * mm, "end": v(-50.37, 15.67) * mm});
            skLineSegment(sketch, "E119.0", {"start": v(-51.97, 9.04) * mm, "end": v(-51.28, 12.38) * mm});
            skLineSegment(sketch, "E120.0", {"start": v(-52.45, 5.65) * mm, "end": v(-51.97, 9.04) * mm});
            skLineSegment(sketch, "E121.0", {"start": v(-52.7, 2.25) * mm, "end": v(-52.45, 5.65) * mm});
            skLineSegment(sketch, "E122.0", {"start": v(-36.77, -37.82) * mm, "end": v(-39.14, -35.36) * mm});
            skLineSegment(sketch, "E123.0", {"start": v(-39.14, -35.36) * mm, "end": v(-41.35, -32.75) * mm});
            skLineSegment(sketch, "E124.0", {"start": v(-41.35, -32.75) * mm, "end": v(-43.38, -30) * mm});
            skLineSegment(sketch, "E125.0", {"start": v(-43.38, -30) * mm, "end": v(-45.23, -27.14) * mm});
            skLineSegment(sketch, "E126.0", {"start": v(-45.23, -27.14) * mm, "end": v(-46.9, -24.15) * mm});
            skLineSegment(sketch, "E127.0", {"start": v(-46.9, -24.15) * mm, "end": v(-48.36, -21.07) * mm});
            skLineSegment(sketch, "E128.0", {"start": v(-48.36, -21.07) * mm, "end": v(-49.62, -17.9) * mm});
            skLineSegment(sketch, "E129.0", {"start": v(-49.62, -17.9) * mm, "end": v(-50.68, -14.64) * mm});
            skLineSegment(sketch, "E130.0", {"start": v(-50.68, -14.64) * mm, "end": v(-51.52, -11.33) * mm});
            skLineSegment(sketch, "E131.0", {"start": v(-51.52, -11.33) * mm, "end": v(-52.14, -7.97) * mm});
            skLineSegment(sketch, "E132.0", {"start": v(-52.14, -7.97) * mm, "end": v(-52.55, -4.58) * mm});
            skLineSegment(sketch, "E133.0", {"start": v(-52.55, -4.58) * mm, "end": v(-52.74, -1.17) * mm});
            skLineSegment(sketch, "E134", {"start": v(-52.73, -37.85) * mm, "end": v(-36.77, -37.82) * mm});
            skLineSegment(sketch, "E135", {"start": v(-52.74, 30.48) * mm, "end": v(-42.76, 30.89) * mm});
            skLineSegment(sketch, "E136.0", {"start": v(-46.4, 25.1) * mm, "end": v(-44.67, 28.06) * mm});
            skSolve(sketch);
        }
        {
            var Q0;
            {var subQ4=sQuery(id+"F8.wireOp",EDGE,"E109");Q0=makeQuery(id+"F8.imprint","IMPRINT",FACE,{"disambiguationData":[TD([[makeQuery(id+"F8.imprint","IMPRINT",EDGE,{"derivedFrom":subQ4}),-1.0]])]});}
            var Q1;
            {var subQ1=sQuery(id+"F8.wireOp",EDGE,"E112");Q1=makeQuery(id+"F8.imprint","IMPRINT",FACE,{"disambiguationData":[TD([[makeQuery(id+"F8.imprint","IMPRINT",EDGE,{"derivedFrom":subQ1}),1.0]])]});}
            var Q2;
            Q2=makeQuery(id+"F8.imprint","IMPRINT",FACE,{"disambiguationData":[TD([[makeQuery(id+"F8.imprint","IMPRINT",EDGE,{"derivedFrom":sQuery(id+"F8.wireOp",EDGE,"E122.0")}),1.0]])]});
            extrude(context, id + "F9", {"entities" : qUnion([Q0, Q1, Q2]), "operationType" : NewBodyOperationType.ADD, "depth" : 5 * mm});
        }
        {
            var Q0;
            Q0=makeQuery(id+"F9.opExtrude","SWEPT_FACE",FACE,{"disambiguationData":[OSD([sQuery(id+"F8.wireOp",EDGE,"E134")])]});
            var sketch = newSketch(context, id + "F10", { "sketchPlane" : qUnion([Q0])});
            skLineSegment(sketch, "E137.0.0", {"start": v(-58, 0) * mm, "end": v(-52.79, 0) * mm});
            skLineSegment(sketch, "E137.0.1", {"start": v(-52.79, 0) * mm, "end": v(-52.79, 5) * mm});
            skLineSegment(sketch, "E137.0.2", {"start": v(-52.79, 5) * mm, "end": v(-58, 5) * mm});
            skLineSegment(sketch, "E137.0.3", {"start": v(-58, 5) * mm, "end": v(-58, 0) * mm});
            skLineSegment(sketch, "E138.0.0", {"start": v(-52.79, 0) * mm, "end": v(-36.83, 0) * mm});
            skLineSegment(sketch, "E138.0.1", {"start": v(-36.83, 0) * mm, "end": v(-36.83, 5) * mm});
            skLineSegment(sketch, "E138.0.2", {"start": v(-36.83, 5) * mm, "end": v(-52.79, 5) * mm});
            skLineSegment(sketch, "E138.0.3", {"start": v(-52.79, 5) * mm, "end": v(-52.79, 0) * mm});
            skLineSegment(sketch, "E139", {"start": v(-58, 2.5) * mm, "end": v(-52.79, 2.5) * mm, "construction": true});
            skCircle(sketch, "E140", {"center": v(-55.4, 2.5) * mm, "radius": 1.5 * mm});
            skSolve(sketch);
        }
        {
            var Q0;
            {var subQ0=sQuery(id+"F0.wireOp",EDGE,"E0");var subQ1=sQuery(id+"F0.wireOp",EDGE,"E104");Q0=makeQuery(id+"F9.boolean.opBoolean","MERGE",EDGE,{"derivedFrom":[makeQuery(id+"F5.opBoolean","MERGE",EDGE,{"derivedFrom":[makeQuery(id+"F2.opPattern","COPY",EDGE,{"derivedFrom":makeQuery(id+"F1.opExtrude","SWEPT_EDGE",EDGE,{"disambiguationData":[OSD([subQ0,sQuery(id+"F0.wireOp",EDGE,"E102"),subQ1])]}),"instanceName":"36"}),makeQuery(id+"F2.opPattern","COPY",EDGE,{"derivedFrom":makeQuery(id+"F1.opExtrude","SWEPT_EDGE",EDGE,{"disambiguationData":[OSD([subQ0,sQuery(id+"F0.wireOp",EDGE,"E103"),subQ1])]}),"instanceName":"37"})]}),makeQuery(id+"F9.opExtrude","SWEPT_EDGE",EDGE,{"disambiguationData":[OSD([sQuery(id+"F8.wireOp",EDGE,"E122.0"),sQuery(id+"F8.wireOp",EDGE,"E134")])]})]});}
            var Q1;
            {var subQ0=sQuery(id+"F0.wireOp",EDGE,"E0");var subQ1=sQuery(id+"F0.wireOp",EDGE,"E104");Q1=makeQuery(id+"F9.boolean.opBoolean","MERGE",EDGE,{"derivedFrom":[makeQuery(id+"F3.opBoolean","MERGE",EDGE,{"derivedFrom":[makeQuery(id+"F2.opPattern","COPY",EDGE,{"derivedFrom":makeQuery(id+"F1.opExtrude","SWEPT_EDGE",EDGE,{"disambiguationData":[OSD([subQ0,sQuery(id+"F0.wireOp",EDGE,"E102"),subQ1])]}),"instanceName":"14"}),makeQuery(id+"F2.opPattern","COPY",EDGE,{"derivedFrom":makeQuery(id+"F1.opExtrude","SWEPT_EDGE",EDGE,{"disambiguationData":[OSD([subQ0,sQuery(id+"F0.wireOp",EDGE,"E103"),subQ1])]}),"instanceName":"15"})]}),makeQuery(id+"F9.opExtrude","SWEPT_EDGE",EDGE,{"disambiguationData":[OSD([sQuery(id+"F8.wireOp",EDGE,"E113.0"),sQuery(id+"F8.wireOp",EDGE,"E135")])]})]});}
            fillet(context, id + "F11", {"entities" : qUnion([Q0, Q1]), "radius" : 5 * mm, "tangentPropagation" : true, "allowEdgeOverflow" : false});
        }
        {
            var Q0;
            Q0=makeQuery(id+"F10.imprint","IMPRINT",FACE,{"disambiguationData":[TD([[makeQuery(id+"F10.imprint","IMPRINT",EDGE,{"derivedFrom":sQuery(id+"F10.wireOp",EDGE,"E140")}),1.0]])]});
            extrude(context, id + "F12", {"entities" : qUnion([Q0]), "operationType" : NewBodyOperationType.REMOVE, "oppositeDirection" : true, "depth" : 15 * mm});
        }
        {
            var Q0;
            Q0=makeQuery(id+"F9.opExtrude","SWEPT_FACE",FACE,{"disambiguationData":[OSD([sQuery(id+"F8.wireOp",EDGE,"E111")])]});
            var sketch = newSketch(context, id + "F13", { "sketchPlane" : qUnion([Q0])});
            skEllipse(sketch, "E141.0", {"center": v(54.8, 2.5) * mm, "majorRadius": 1.5 * mm, "minorRadius": 1.5 * mm, "majorAxis": v(0, 1)});
            skSolve(sketch);
        }
        {
            var Q0;
            Q0=makeQuery(id+"F13.imprint","IMPRINT",FACE,{"disambiguationData":[TD([[makeQuery(id+"F13.imprint","IMPRINT",EDGE,{"derivedFrom":sQuery(id+"F13.wireOp",EDGE,"E141.0")}),1.0]])]});
            extrude(context, id + "F14", {"entities" : qUnion([Q0]), "operationType" : NewBodyOperationType.REMOVE, "oppositeDirection" : true, "depth" : 25 * mm});
        }
    });
